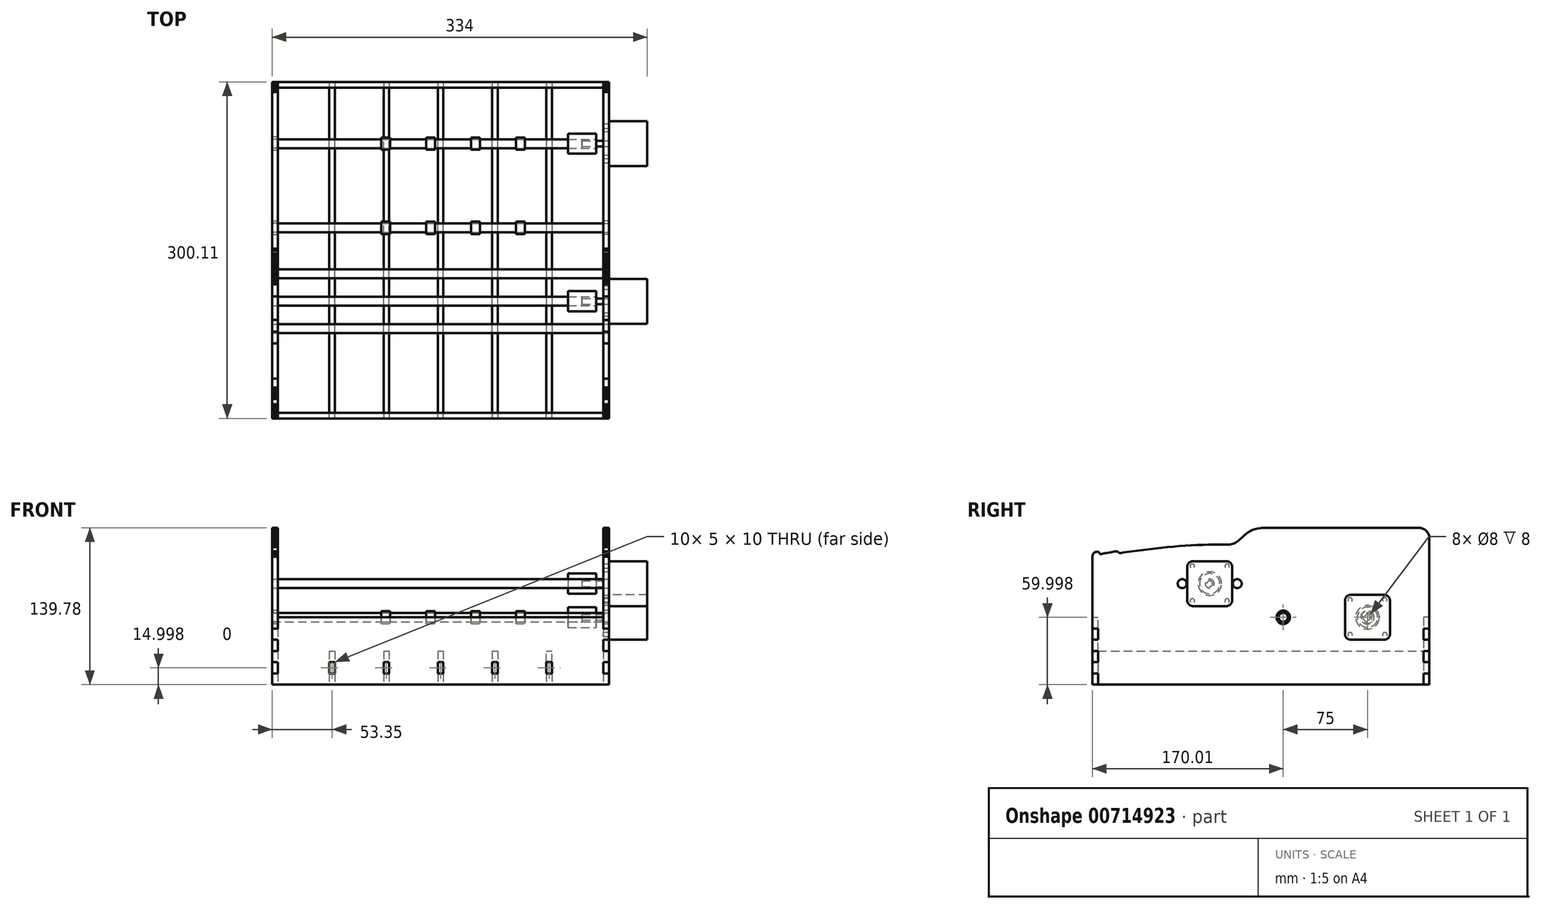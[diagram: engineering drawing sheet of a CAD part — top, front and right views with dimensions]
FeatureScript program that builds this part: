
annotation { "Feature Type Name" : "Feature", "Feature Type Description" : "" }
export const myFeature = defineFeature(function(context is Context, id is Id, definition is map)
    precondition{}
    {
        {
            assignVariable(context, id + "F0", {"name" : "panel_thickness", "anyValue" : 5});
        }
        {
            var Q0;
            Q0=qCreatedBy(makeId("Right.planeOp"),FACE);
            var sketch = newSketch(context, id + "F1", { "sketchPlane" : qUnion([Q0])});
            skLineSegment(sketch, "E0", {"start": v(-150.05, 30.1) * mm, "end": v(-150.05, 40.34) * mm});
            skLineSegment(sketch, "E1", {"start": v(-150.05, 40.34) * mm, "end": v(-150.05, 42.88) * mm});
            skLineSegment(sketch, "E2", {"start": v(-150.05, 42.88) * mm, "end": v(-150.05, 42.97) * mm});
            skLineSegment(sketch, "E3", {"start": v(-150.05, 42.97) * mm, "end": v(-150.05, 43.01) * mm});
            skLineSegment(sketch, "E4", {"start": v(-150.05, 43.01) * mm, "end": v(-150.05, 43.05) * mm});
            skLineSegment(sketch, "E5", {"start": v(-150.05, 43.05) * mm, "end": v(-150.05, 43.14) * mm});
            skLineSegment(sketch, "E6", {"start": v(-150.05, 43.14) * mm, "end": v(-150.05, 43.3) * mm});
            skLineSegment(sketch, "E7", {"start": v(-150.05, 43.3) * mm, "end": v(-150.05, 44.03) * mm});
            skLineSegment(sketch, "E8", {"start": v(-150.05, 44.03) * mm, "end": v(-150, 44.7) * mm});
            skLineSegment(sketch, "E9", {"start": v(-150, 44.7) * mm, "end": v(-149.88, 45.34) * mm});
            skLineSegment(sketch, "E10", {"start": v(-149.88, 45.34) * mm, "end": v(-149.71, 45.97) * mm});
            skLineSegment(sketch, "E11", {"start": v(-149.71, 45.97) * mm, "end": v(-149.46, 46.52) * mm});
            skLineSegment(sketch, "E12", {"start": v(-149.46, 46.52) * mm, "end": v(-149.08, 47.07) * mm});
            skLineSegment(sketch, "E13", {"start": v(-149.08, 47.07) * mm, "end": v(-148.61, 47.5) * mm});
            skLineSegment(sketch, "E14", {"start": v(-148.61, 47.5) * mm, "end": v(-148.06, 47.88) * mm});
            skLineSegment(sketch, "E15", {"start": v(-148.06, 47.88) * mm, "end": v(-147.43, 48.18) * mm});
            skLineSegment(sketch, "E16", {"start": v(-147.43, 48.18) * mm, "end": v(-146.75, 48.39) * mm});
            skLineSegment(sketch, "E17", {"start": v(-146.75, 48.39) * mm, "end": v(-146.03, 48.51) * mm});
            skLineSegment(sketch, "E18", {"start": v(-146.03, 48.51) * mm, "end": v(-145.35, 48.51) * mm});
            skLineSegment(sketch, "E19", {"start": v(-145.35, 48.51) * mm, "end": v(-145.01, 48.47) * mm});
            skLineSegment(sketch, "E20", {"start": v(-145.01, 48.47) * mm, "end": v(-144.67, 48.39) * mm});
            skLineSegment(sketch, "E21", {"start": v(-144.67, 48.39) * mm, "end": v(-144.42, 48.22) * mm});
            skLineSegment(sketch, "E22", {"start": v(-144.42, 48.22) * mm, "end": v(-144.17, 47.96) * mm});
            skLineSegment(sketch, "E23", {"start": v(-144.17, 47.96) * mm, "end": v(-143.83, 47.37) * mm});
            skLineSegment(sketch, "E24", {"start": v(-143.83, 47.37) * mm, "end": v(-143.45, 46.82) * mm});
            skLineSegment(sketch, "E25", {"start": v(-143.45, 46.82) * mm, "end": v(-143.23, 46.6) * mm});
            skLineSegment(sketch, "E26", {"start": v(-143.23, 46.6) * mm, "end": v(-142.98, 46.48) * mm});
            skLineSegment(sketch, "E27", {"start": v(-142.98, 46.48) * mm, "end": v(-142.64, 46.48) * mm});
            skLineSegment(sketch, "E28", {"start": v(-142.64, 46.48) * mm, "end": v(-142.3, 46.48) * mm});
            skLineSegment(sketch, "E29", {"start": v(-142.3, 46.48) * mm, "end": v(-141.58, 46.65) * mm});
            skLineSegment(sketch, "E30", {"start": v(-141.58, 46.65) * mm, "end": v(-140.19, 46.9) * mm});
            skLineSegment(sketch, "E31", {"start": v(-140.19, 46.9) * mm, "end": v(-138.87, 47.16) * mm});
            skLineSegment(sketch, "E32", {"start": v(-138.87, 47.16) * mm, "end": v(-137.56, 47.37) * mm});
            skLineSegment(sketch, "E33", {"start": v(-137.56, 47.37) * mm, "end": v(-135.06, 47.84) * mm});
            skLineSegment(sketch, "E34", {"start": v(-135.06, 47.84) * mm, "end": v(-132.57, 48.3) * mm});
            skLineSegment(sketch, "E35", {"start": v(-132.57, 48.3) * mm, "end": v(-131.3, 48.56) * mm});
            skLineSegment(sketch, "E36", {"start": v(-131.3, 48.56) * mm, "end": v(-129.94, 48.81) * mm});
            skLineSegment(sketch, "E37", {"start": v(-129.94, 48.81) * mm, "end": v(-129.22, 48.9) * mm});
            skLineSegment(sketch, "E38", {"start": v(-129.22, 48.9) * mm, "end": v(-128.59, 48.94) * mm});
            skLineSegment(sketch, "E39", {"start": v(-128.59, 48.94) * mm, "end": v(-128.25, 48.94) * mm});
            skLineSegment(sketch, "E40", {"start": v(-128.25, 48.94) * mm, "end": v(-127.95, 48.85) * mm});
            skLineSegment(sketch, "E41", {"start": v(-127.95, 48.85) * mm, "end": v(-127.66, 48.73) * mm});
            skLineSegment(sketch, "E42", {"start": v(-127.66, 48.73) * mm, "end": v(-127.36, 48.56) * mm});
            skLineSegment(sketch, "E43", {"start": v(-127.36, 48.56) * mm, "end": v(-126.3, 47.75) * mm});
            skLineSegment(sketch, "E44", {"start": v(-126.3, 47.75) * mm, "end": v(-126, 47.58) * mm});
            skLineSegment(sketch, "E45", {"start": v(-126, 47.58) * mm, "end": v(-125.7, 47.46) * mm});
            skLineSegment(sketch, "E46", {"start": v(-125.7, 47.46) * mm, "end": v(-125.41, 47.41) * mm});
            skLineSegment(sketch, "E47", {"start": v(-125.41, 47.41) * mm, "end": v(-125.07, 47.41) * mm});
            skLineSegment(sketch, "E48", {"start": v(-125.07, 47.41) * mm, "end": v(-123.72, 47.62) * mm});
            skLineSegment(sketch, "E49", {"start": v(-123.72, 47.62) * mm, "end": v(-122.36, 47.8) * mm});
            skLineSegment(sketch, "E50", {"start": v(-122.36, 47.8) * mm, "end": v(-119.74, 48.18) * mm});
            skLineSegment(sketch, "E51", {"start": v(-119.74, 48.18) * mm, "end": v(-114.66, 48.9) * mm});
            skLineSegment(sketch, "E52", {"start": v(-114.66, 48.9) * mm, "end": v(-109.5, 49.57) * mm});
            skLineSegment(sketch, "E53", {"start": v(-109.5, 49.57) * mm, "end": v(-104.29, 50.25) * mm});
            skLineSegment(sketch, "E54", {"start": v(-104.29, 50.25) * mm, "end": v(-93.83, 51.52) * mm});
            skLineSegment(sketch, "E55", {"start": v(-93.83, 51.52) * mm, "end": v(-88.54, 52.11) * mm});
            skLineSegment(sketch, "E56", {"start": v(-88.54, 52.11) * mm, "end": v(-83.25, 52.66) * mm});
            skLineSegment(sketch, "E57", {"start": v(-83.25, 52.66) * mm, "end": v(-77.96, 53.13) * mm});
            skLineSegment(sketch, "E58", {"start": v(-77.96, 53.13) * mm, "end": v(-72.67, 53.6) * mm});
            skLineSegment(sketch, "E59", {"start": v(-72.67, 53.6) * mm, "end": v(-67.42, 53.93) * mm});
            skLineSegment(sketch, "E60", {"start": v(-67.42, 53.93) * mm, "end": v(-62.2, 54.27) * mm});
            skLineSegment(sketch, "E61", {"start": v(-62.2, 54.27) * mm, "end": v(-56.96, 54.48) * mm});
            skLineSegment(sketch, "E62", {"start": v(-56.96, 54.48) * mm, "end": v(-51.75, 54.65) * mm});
            skLineSegment(sketch, "E63", {"start": v(-51.75, 54.65) * mm, "end": v(-46.5, 54.78) * mm});
            skLineSegment(sketch, "E64", {"start": v(-46.5, 54.78) * mm, "end": v(-41.21, 54.86) * mm});
            skLineSegment(sketch, "E65", {"start": v(-41.21, 54.86) * mm, "end": v(-35.88, 54.86) * mm});
            skLineSegment(sketch, "E66", {"start": v(-35.88, 54.86) * mm, "end": v(-30.46, 54.9) * mm});
            skLineSegment(sketch, "E67", {"start": v(-30.46, 54.9) * mm, "end": v(-29.1, 54.95) * mm});
            skLineSegment(sketch, "E68", {"start": v(-29.1, 54.95) * mm, "end": v(-27.8, 55.08) * mm});
            skLineSegment(sketch, "E69", {"start": v(-27.8, 55.08) * mm, "end": v(-26.52, 55.29) * mm});
            skLineSegment(sketch, "E70", {"start": v(-26.52, 55.29) * mm, "end": v(-25.25, 55.58) * mm});
            skLineSegment(sketch, "E71", {"start": v(-25.25, 55.58) * mm, "end": v(-24.07, 56) * mm});
            skLineSegment(sketch, "E72", {"start": v(-24.07, 56) * mm, "end": v(-22.88, 56.56) * mm});
            skLineSegment(sketch, "E73", {"start": v(-22.88, 56.56) * mm, "end": v(-21.78, 57.2) * mm});
            skLineSegment(sketch, "E74", {"start": v(-21.78, 57.2) * mm, "end": v(-20.72, 57.91) * mm});
            skLineSegment(sketch, "E75", {"start": v(-20.72, 57.91) * mm, "end": v(-19.66, 58.72) * mm});
            skLineSegment(sketch, "E76", {"start": v(-19.66, 58.72) * mm, "end": v(-18.65, 59.6) * mm});
            skLineSegment(sketch, "E77", {"start": v(-18.65, 59.6) * mm, "end": v(-16.62, 61.43) * mm});
            skLineSegment(sketch, "E78", {"start": v(-16.62, 61.43) * mm, "end": v(-14.63, 63.25) * mm});
            skLineSegment(sketch, "E79", {"start": v(-14.63, 63.25) * mm, "end": v(-13.61, 64.13) * mm});
            skLineSegment(sketch, "E80", {"start": v(-13.61, 64.13) * mm, "end": v(-12.55, 64.98) * mm});
            skLineSegment(sketch, "E81", {"start": v(-12.55, 64.98) * mm, "end": v(-11.5, 65.74) * mm});
            skLineSegment(sketch, "E82", {"start": v(-11.5, 65.74) * mm, "end": v(-10.4, 66.46) * mm});
            skLineSegment(sketch, "E83", {"start": v(-10.4, 66.46) * mm, "end": v(-9.25, 67.1) * mm});
            skLineSegment(sketch, "E84", {"start": v(-9.25, 67.1) * mm, "end": v(-8.1, 67.7) * mm});
            skLineSegment(sketch, "E85", {"start": v(-8.1, 67.7) * mm, "end": v(-6.88, 68.16) * mm});
            skLineSegment(sketch, "E86", {"start": v(-6.88, 68.16) * mm, "end": v(-5.65, 68.54) * mm});
            skLineSegment(sketch, "E87", {"start": v(-5.65, 68.54) * mm, "end": v(-4.38, 68.88) * mm});
            skLineSegment(sketch, "E88", {"start": v(-4.38, 68.88) * mm, "end": v(-3.07, 69.17) * mm});
            skLineSegment(sketch, "E89", {"start": v(-3.07, 69.17) * mm, "end": v(-0.44, 69.64) * mm});
            skLineSegment(sketch, "E90", {"start": v(-0.44, 69.64) * mm, "end": v(0.91, 69.85) * mm});
            skLineSegment(sketch, "E91", {"start": v(0.91, 69.85) * mm, "end": v(1.2, 69.9) * mm});
            skLineSegment(sketch, "E92", {"start": v(1.2, 69.9) * mm, "end": v(1.25, 69.9) * mm});
            skLineSegment(sketch, "E93", {"start": v(1.25, 69.9) * mm, "end": v(1.3, 69.9) * mm});
            skLineSegment(sketch, "E94", {"start": v(1.3, 69.9) * mm, "end": v(1.38, 69.9) * mm});
            skLineSegment(sketch, "E95", {"start": v(1.38, 69.9) * mm, "end": v(1.59, 69.9) * mm});
            skLineSegment(sketch, "E96", {"start": v(1.59, 69.9) * mm, "end": v(2.05, 69.9) * mm});
            skLineSegment(sketch, "E97", {"start": v(2.05, 69.9) * mm, "end": v(3.75, 69.9) * mm});
            skLineSegment(sketch, "E98", {"start": v(3.75, 69.9) * mm, "end": v(7.22, 69.9) * mm});
            skLineSegment(sketch, "E99", {"start": v(7.22, 69.9) * mm, "end": v(14.12, 69.9) * mm});
            skLineSegment(sketch, "E100", {"start": v(14.12, 69.9) * mm, "end": v(27.96, 69.9) * mm});
            skLineSegment(sketch, "E101", {"start": v(27.96, 69.9) * mm, "end": v(83.25, 69.9) * mm});
            skLineSegment(sketch, "E102", {"start": v(83.25, 69.9) * mm, "end": v(138.58, 69.9) * mm});
            skLineSegment(sketch, "E103", {"start": v(138.58, 69.9) * mm, "end": v(140.27, 69.9) * mm});
            skLineSegment(sketch, "E104", {"start": v(140.27, 69.9) * mm, "end": v(140.4, 69.9) * mm});
            skLineSegment(sketch, "E105", {"start": v(140.4, 69.9) * mm, "end": v(140.61, 69.9) * mm});
            skLineSegment(sketch, "E106", {"start": v(140.61, 69.9) * mm, "end": v(141.08, 69.9) * mm});
            skLineSegment(sketch, "E107", {"start": v(141.08, 69.9) * mm, "end": v(142, 69.8) * mm});
            skLineSegment(sketch, "E108", {"start": v(142, 69.8) * mm, "end": v(142.94, 69.6) * mm});
            skLineSegment(sketch, "E109", {"start": v(142.94, 69.6) * mm, "end": v(143.87, 69.3) * mm});
            skLineSegment(sketch, "E110", {"start": v(143.87, 69.3) * mm, "end": v(144.76, 68.96) * mm});
            skLineSegment(sketch, "E111", {"start": v(144.76, 68.96) * mm, "end": v(145.56, 68.5) * mm});
            skLineSegment(sketch, "E112", {"start": v(145.56, 68.5) * mm, "end": v(146.37, 67.94) * mm});
            skLineSegment(sketch, "E113", {"start": v(146.37, 67.94) * mm, "end": v(147.09, 67.3) * mm});
            skLineSegment(sketch, "E114", {"start": v(147.09, 67.3) * mm, "end": v(147.72, 66.67) * mm});
            skLineSegment(sketch, "E115", {"start": v(147.72, 66.67) * mm, "end": v(148.27, 65.96) * mm});
            skLineSegment(sketch, "E116", {"start": v(148.27, 65.96) * mm, "end": v(148.78, 65.15) * mm});
            skLineSegment(sketch, "E117", {"start": v(148.78, 65.15) * mm, "end": v(149.2, 64.3) * mm});
            skLineSegment(sketch, "E118", {"start": v(149.2, 64.3) * mm, "end": v(149.58, 63.42) * mm});
            skLineSegment(sketch, "E119", {"start": v(149.58, 63.42) * mm, "end": v(149.84, 62.48) * mm});
            skLineSegment(sketch, "E120", {"start": v(149.84, 62.48) * mm, "end": v(150, 61.55) * mm});
            skLineSegment(sketch, "E121", {"start": v(150, 61.55) * mm, "end": v(150.05, 60.62) * mm});
            skLineSegment(sketch, "E122", {"start": v(150.05, 60.62) * mm, "end": v(150, 59.69) * mm});
            skLineSegment(sketch, "E123", {"start": v(150, 59.69) * mm, "end": v(149.97, 59.22) * mm});
            skLineSegment(sketch, "E124", {"start": v(149.97, 59.22) * mm, "end": v(149.97, 58.97) * mm});
            skLineSegment(sketch, "E125", {"start": v(149.97, 58.97) * mm, "end": v(149.92, 58.89) * mm});
            skLineSegment(sketch, "E126", {"start": v(149.92, 58.89) * mm, "end": v(149.92, 58.8) * mm});
            skLineSegment(sketch, "E127", {"start": v(149.92, 58.8) * mm, "end": v(149.92, 58.63) * mm});
            skLineSegment(sketch, "E128", {"start": v(149.92, 58.63) * mm, "end": v(149.92, 52.96) * mm});
            skLineSegment(sketch, "E129", {"start": v(149.92, 52.96) * mm, "end": v(149.92, 30.1) * mm});
            skLineSegment(sketch, "E130", {"start": v(144.93, -59.9) * mm, "end": v(144.93, -69.9) * mm});
            skLineSegment(sketch, "E131", {"start": v(144.93, -69.9) * mm, "end": v(-145.06, -69.9) * mm});
            skLineSegment(sketch, "E132", {"start": v(-145.06, -59.9) * mm, "end": v(-145.06, -69.9) * mm});
            skLineSegment(sketch, "E133", {"start": v(149.92, -59.9) * mm, "end": v(144.93, -59.9) * mm});
            skLineSegment(sketch, "E134", {"start": v(-150.05, -59.9) * mm, "end": v(-145.06, -59.9) * mm});
            skLineSegment(sketch, "E135", {"start": v(149.92, -49.91) * mm, "end": v(149.92, -59.9) * mm});
            skLineSegment(sketch, "E136", {"start": v(-150.05, -59.9) * mm, "end": v(-150.05, -49.91) * mm});
            skLineSegment(sketch, "E137", {"start": v(144.93, -49.91) * mm, "end": v(149.92, -49.91) * mm});
            skLineSegment(sketch, "E138", {"start": v(-145.06, -49.91) * mm, "end": v(-150.05, -49.91) * mm});
            skLineSegment(sketch, "E139", {"start": v(144.93, -39.88) * mm, "end": v(144.93, -49.91) * mm});
            skLineSegment(sketch, "E140", {"start": v(-145.06, -39.88) * mm, "end": v(-145.06, -49.91) * mm});
            skLineSegment(sketch, "E141", {"start": v(149.92, -39.88) * mm, "end": v(144.93, -39.88) * mm});
            skLineSegment(sketch, "E142", {"start": v(-150.05, -39.88) * mm, "end": v(-145.06, -39.88) * mm});
            skLineSegment(sketch, "E143", {"start": v(149.92, -29.89) * mm, "end": v(149.92, -39.88) * mm});
            skLineSegment(sketch, "E144", {"start": v(-150.05, -39.88) * mm, "end": v(-150.05, -29.89) * mm});
            skLineSegment(sketch, "E145", {"start": v(144.93, -29.89) * mm, "end": v(149.92, -29.89) * mm});
            skLineSegment(sketch, "E146", {"start": v(-145.06, -29.89) * mm, "end": v(-150.05, -29.89) * mm});
            skLineSegment(sketch, "E147", {"start": v(144.93, -19.9) * mm, "end": v(144.93, -29.89) * mm});
            skLineSegment(sketch, "E148", {"start": v(-145.06, -19.9) * mm, "end": v(-145.06, -29.89) * mm});
            skLineSegment(sketch, "E149", {"start": v(149.92, -19.9) * mm, "end": v(144.93, -19.9) * mm});
            skLineSegment(sketch, "E150", {"start": v(-150.05, -19.9) * mm, "end": v(-145.06, -19.9) * mm});
            skLineSegment(sketch, "E151", {"start": v(149.92, 30.1) * mm, "end": v(149.92, -19.9) * mm});
            skLineSegment(sketch, "E152", {"start": v(-150.05, -19.9) * mm, "end": v(-150.05, 30.1) * mm});
            skCircle(sketch, "E153", {"center": v(-45.55, 20.1) * mm, "radius": 10.5 * mm});
            skLineSegment(sketch, "E154", {"start": v(-70.05, 20.1) * mm, "end": v(-45.55, 20.1) * mm, "construction": true});
            skCircle(sketch, "E155", {"center": v(-70.05, 20.1) * mm, "radius": 4 * mm});
            skLineSegment(sketch, "E156", {"start": v(-45.55, 20.1) * mm, "end": v(-21.05, 20.1) * mm, "construction": true});
            skCircle(sketch, "E157", {"center": v(-21.05, 20.1) * mm, "radius": 4 * mm});
            skLineSegment(sketch, "E158", {"start": v(-45.55, 20.1) * mm, "end": v(-30.06, 35.6) * mm, "construction": true});
            skCircle(sketch, "E159", {"center": v(-30.06, 35.6) * mm, "radius": 2 * mm});
            skLineSegment(sketch, "E160", {"start": v(-45.55, 20.1) * mm, "end": v(-30.06, 4.62) * mm, "construction": true});
            skLineSegment(sketch, "E161", {"start": v(-45.55, 20.1) * mm, "end": v(-61.04, 4.62) * mm, "construction": true});
            skLineSegment(sketch, "E162", {"start": v(-45.55, 20.1) * mm, "end": v(-61.04, 35.6) * mm, "construction": true});
            skCircle(sketch, "E163", {"center": v(-61.04, 35.6) * mm, "radius": 2 * mm});
            skCircle(sketch, "E164", {"center": v(-61.04, 4.62) * mm, "radius": 2 * mm});
            skCircle(sketch, "E165", {"center": v(-30.06, 4.62) * mm, "radius": 2 * mm});
            skLineSegment(sketch, "E166", {"start": v(-45.55, 20.1) * mm, "end": v(-45.55, -69.9) * mm, "construction": true});
            skLineSegment(sketch, "E167", {"start": v(19.95, -9.9) * mm, "end": v(19.95, -69.9) * mm, "construction": true});
            skCircle(sketch, "E168", {"center": v(19.95, -9.9) * mm, "radius": 6 * mm});
            skLineSegment(sketch, "E169", {"start": v(94.95, -9.9) * mm, "end": v(94.95, -69.9) * mm, "construction": true});
            skCircle(sketch, "E170", {"center": v(94.95, -9.9) * mm, "radius": 10.5 * mm});
            skLineSegment(sketch, "E171", {"start": v(94.95, -9.9) * mm, "end": v(110.44, 5.6) * mm, "construction": true});
            skLineSegment(sketch, "E172", {"start": v(94.95, -9.9) * mm, "end": v(110.44, -25.38) * mm, "construction": true});
            skLineSegment(sketch, "E173", {"start": v(94.95, -9.9) * mm, "end": v(79.46, -25.38) * mm, "construction": true});
            skLineSegment(sketch, "E174", {"start": v(94.95, -9.9) * mm, "end": v(79.46, 5.6) * mm, "construction": true});
            skCircle(sketch, "E175", {"center": v(110.44, 5.6) * mm, "radius": 2 * mm});
            skCircle(sketch, "E176", {"center": v(110.44, -25.38) * mm, "radius": 2 * mm});
            skCircle(sketch, "E177", {"center": v(79.46, -25.38) * mm, "radius": 2 * mm});
            skCircle(sketch, "E178", {"center": v(79.46, 5.6) * mm, "radius": 2 * mm});
            skSolve(sketch);
        }
        {
            var Q0;
            Q0=makeQuery(id+"F1.imprint","IMPRINT",FACE,{"disambiguationData":[TD([[makeQuery(id+"F1.imprint","IMPRINT",EDGE,{"derivedFrom":sQuery(id+"F1.wireOp",EDGE,"E0")}),-1.0]])]});
            extrude(context, id + "F2", {"entities" : qUnion([Q0]), "depth" : (getVariable(context, 'panel_thickness')) * mm, "offsetDistance" : 25 * mm});
        }
        {
            var Q0;
            Q0=makeQuery(id+"F2.opExtrude","SWEPT_FACE",FACE,{"disambiguationData":[OSD([sQuery(id+"F1.wireOp",EDGE,"E148")])]});
            var sketch = newSketch(context, id + "F3", { "sketchPlane" : qUnion([Q0])});
            skPoint(sketch, "E179.0", {"position": v(0, -69.9) * mm});
            skPoint(sketch, "E179.1", {"position": v(5, -69.9) * mm});
            skPoint(sketch, "E179.2", {"position": v(5, -59.9) * mm});
            skPoint(sketch, "E179.3", {"position": v(0, -59.9) * mm});
            skPoint(sketch, "E179.4", {"position": v(0, -49.91) * mm});
            skPoint(sketch, "E179.5", {"position": v(5, -49.91) * mm});
            skPoint(sketch, "E179.6", {"position": v(0, -29.89) * mm});
            skPoint(sketch, "E179.7", {"position": v(5, -29.89) * mm});
            skPoint(sketch, "E179.8", {"position": v(0, -39.88) * mm});
            skPoint(sketch, "E179.9", {"position": v(5, -39.88) * mm});
            skPoint(sketch, "E179.10", {"position": v(0, -19.9) * mm});
            skPoint(sketch, "E179.11", {"position": v(5, -19.9) * mm});
            skLineSegment(sketch, "E180", {"start": v(0, -69.9) * mm, "end": v(5, -69.9) * mm});
            skLineSegment(sketch, "E181", {"start": v(5, -69.9) * mm, "end": v(5, -59.9) * mm});
            skLineSegment(sketch, "E182", {"start": v(5, -59.9) * mm, "end": v(0, -59.9) * mm});
            skLineSegment(sketch, "E183", {"start": v(0, -59.9) * mm, "end": v(0, -49.91) * mm});
            skLineSegment(sketch, "E184", {"start": v(0, -49.91) * mm, "end": v(5, -49.91) * mm});
            skLineSegment(sketch, "E185", {"start": v(5, -49.91) * mm, "end": v(5, -39.88) * mm});
            skLineSegment(sketch, "E186", {"start": v(5, -39.88) * mm, "end": v(0, -39.88) * mm});
            skLineSegment(sketch, "E187", {"start": v(0, -39.88) * mm, "end": v(0, -29.89) * mm});
            skLineSegment(sketch, "E188", {"start": v(0, -29.89) * mm, "end": v(5, -29.89) * mm});
            skLineSegment(sketch, "E189", {"start": v(5, -29.89) * mm, "end": v(5, -19.9) * mm});
            skLineSegment(sketch, "E190", {"start": v(5, -19.9) * mm, "end": v(0, -19.9) * mm});
            skLineSegment(sketch, "E191", {"start": v(0, -19.9) * mm, "end": v(0, -9.9) * mm});
            skLineSegment(sketch, "E192", {"start": v(0, -9.9) * mm, "end": v(-290, -9.9) * mm});
            skLineSegment(sketch, "E193", {"start": v(-145, -9.9) * mm, "end": v(-145, -69.9) * mm, "construction": true});
            skLineSegment(sketch, "E194", {"start": v(0, -69.9) * mm, "end": v(-145, -69.9) * mm});
            skLineSegment(sketch, "E195", {"start": v(-145, -59.9) * mm, "end": v(-142.5, -59.9) * mm});
            skLineSegment(sketch, "E196", {"start": v(-142.5, -59.9) * mm, "end": v(-142.5, -49.9) * mm});
            skLineSegment(sketch, "E197", {"start": v(-142.5, -49.9) * mm, "end": v(-145, -49.9) * mm});
            skLineSegment(sketch, "E198.bottom", {"start": v(-99.17, -49.9) * mm, "end": v(-94.17, -49.9) * mm});
            skLineSegment(sketch, "E198.top", {"start": v(-99.17, -59.9) * mm, "end": v(-94.17, -59.9) * mm});
            skLineSegment(sketch, "E198.left", {"start": v(-99.17, -49.9) * mm, "end": v(-99.17, -59.9) * mm});
            skLineSegment(sketch, "E198.right", {"start": v(-94.17, -49.9) * mm, "end": v(-94.17, -59.9) * mm});
            skLineSegment(sketch, "E199.bottom", {"start": v(-50.85, -49.9) * mm, "end": v(-45.85, -49.9) * mm});
            skLineSegment(sketch, "E199.top", {"start": v(-50.85, -59.9) * mm, "end": v(-45.85, -59.9) * mm});
            skLineSegment(sketch, "E199.left", {"start": v(-50.85, -49.9) * mm, "end": v(-50.85, -59.9) * mm});
            skLineSegment(sketch, "E199.right", {"start": v(-45.85, -49.9) * mm, "end": v(-45.85, -59.9) * mm});
            skLineSegment(sketch, "E200", {"start": v(-142.5, -59.9) * mm, "end": v(-99.17, -59.9) * mm, "construction": true});
            skLineSegment(sketch, "E201", {"start": v(-94.17, -59.9) * mm, "end": v(-50.85, -59.9) * mm, "construction": true});
            skLineSegment(sketch, "E202", {"start": v(-45.85, -59.9) * mm, "end": v(0, -59.9) * mm, "construction": true});
            skLineSegment(sketch, "E203.MirrorCS", {"start": v(-290, -19.9) * mm, "end": v(-290, -9.9) * mm});
            skLineSegment(sketch, "E204.MirrorCS", {"start": v(-295, -19.9) * mm, "end": v(-290, -19.9) * mm});
            skLineSegment(sketch, "E205.MirrorCS", {"start": v(-295, -29.89) * mm, "end": v(-295, -19.9) * mm});
            skLineSegment(sketch, "E206.MirrorCS", {"start": v(-290, -29.89) * mm, "end": v(-295, -29.89) * mm});
            skLineSegment(sketch, "E207.MirrorCS", {"start": v(-290, -39.88) * mm, "end": v(-290, -29.89) * mm});
            skLineSegment(sketch, "E208.MirrorCS", {"start": v(-295, -39.88) * mm, "end": v(-290, -39.88) * mm});
            skLineSegment(sketch, "E209.MirrorCS", {"start": v(-295, -49.91) * mm, "end": v(-295, -39.88) * mm});
            skLineSegment(sketch, "E210.MirrorCS", {"start": v(-290, -49.91) * mm, "end": v(-295, -49.91) * mm});
            skLineSegment(sketch, "E211.MirrorCS", {"start": v(-290, -59.9) * mm, "end": v(-290, -49.91) * mm});
            skLineSegment(sketch, "E212.MirrorCS", {"start": v(-295, -59.9) * mm, "end": v(-290, -59.9) * mm});
            skLineSegment(sketch, "E213.MirrorCS", {"start": v(-295, -69.9) * mm, "end": v(-295, -59.9) * mm});
            skLineSegment(sketch, "E214.MirrorCS", {"start": v(-290, -69.9) * mm, "end": v(-295, -69.9) * mm});
            skLineSegment(sketch, "E215.MirrorCS", {"start": v(-290, -69.9) * mm, "end": v(-145, -69.9) * mm});
            skLineSegment(sketch, "E216.MirrorCS", {"start": v(-244.15, -49.9) * mm, "end": v(-244.15, -59.9) * mm});
            skLineSegment(sketch, "E217.MirrorCS", {"start": v(-239.15, -49.9) * mm, "end": v(-244.15, -49.9) * mm});
            skLineSegment(sketch, "E218.MirrorCS", {"start": v(-239.15, -49.9) * mm, "end": v(-239.15, -59.9) * mm});
            skLineSegment(sketch, "E219.MirrorCS", {"start": v(-239.15, -59.9) * mm, "end": v(-244.15, -59.9) * mm});
            skLineSegment(sketch, "E220.MirrorCS", {"start": v(-195.82, -49.9) * mm, "end": v(-195.82, -59.9) * mm});
            skLineSegment(sketch, "E221.MirrorCS", {"start": v(-190.82, -49.9) * mm, "end": v(-195.82, -49.9) * mm});
            skLineSegment(sketch, "E222.MirrorCS", {"start": v(-190.82, -49.9) * mm, "end": v(-190.82, -59.9) * mm});
            skLineSegment(sketch, "E223.MirrorCS", {"start": v(-190.82, -59.9) * mm, "end": v(-195.82, -59.9) * mm});
            skLineSegment(sketch, "E224.MirrorCS", {"start": v(-145, -59.9) * mm, "end": v(-147.5, -59.9) * mm});
            skLineSegment(sketch, "E225.MirrorCS", {"start": v(-147.5, -59.9) * mm, "end": v(-147.5, -49.9) * mm});
            skLineSegment(sketch, "E226.MirrorCS", {"start": v(-147.5, -49.9) * mm, "end": v(-145, -49.9) * mm});
            skSolve(sketch);
        }
        {
            var Q0;
            Q0=makeQuery(id+"F3.imprint","IMPRINT",FACE,{"disambiguationData":[TD([[makeQuery(id+"F3.imprint","IMPRINT",EDGE,{"derivedFrom":sQuery(id+"F3.wireOp",EDGE,"E180")}),1.0]])]});
            var Q1;
            Q1=makeQuery(id+"F3.imprint","IMPRINT",FACE,{"disambiguationData":[TD([[makeQuery(id+"F3.imprint","IMPRINT",EDGE,{"derivedFrom":sQuery(id+"F3.wireOp",EDGE,"E188")}),-1.0]])]});
            extrude(context, id + "F4", {"entities" : qUnion([Q0, Q1]), "depth" : (getVariable(context, 'panel_thickness')) * mm, "offsetDistance" : 25 * mm});
        }
        {
            var Q0;
            Q0=makeQuery(id+"F2.opExtrude","SWEPT_FACE",FACE,{"disambiguationData":[OSD([sQuery(id+"F1.wireOp",EDGE,"E147")])]});
            var sketch = newSketch(context, id + "F5", { "sketchPlane" : qUnion([Q0])});
            skLineSegment(sketch, "E227.0.0", {"start": v(0, -29.89) * mm, "end": v(0, -39.88) * mm});
            skLineSegment(sketch, "E227.0.1", {"start": v(0, -39.88) * mm, "end": v(-5, -39.88) * mm});
            skLineSegment(sketch, "E227.0.2", {"start": v(-5, -39.88) * mm, "end": v(-5, -49.91) * mm});
            skLineSegment(sketch, "E227.0.3", {"start": v(-5, -49.91) * mm, "end": v(0, -49.91) * mm});
            skLineSegment(sketch, "E227.0.4", {"start": v(0, -49.91) * mm, "end": v(0, -59.9) * mm});
            skLineSegment(sketch, "E227.0.5", {"start": v(0, -59.9) * mm, "end": v(-5, -59.9) * mm});
            skLineSegment(sketch, "E227.0.6", {"start": v(-5, -59.9) * mm, "end": v(-5, -69.9) * mm});
            skLineSegment(sketch, "E227.0.7", {"start": v(-5, -69.9) * mm, "end": v(295, -69.9) * mm});
            skLineSegment(sketch, "E227.0.8", {"start": v(295, -69.9) * mm, "end": v(295, -59.9) * mm});
            skLineSegment(sketch, "E227.0.9", {"start": v(295, -59.9) * mm, "end": v(290, -59.9) * mm});
            skLineSegment(sketch, "E227.0.10", {"start": v(290, -59.9) * mm, "end": v(290, -49.91) * mm});
            skLineSegment(sketch, "E227.0.11", {"start": v(290, -49.91) * mm, "end": v(295, -49.91) * mm});
            skLineSegment(sketch, "E227.0.12", {"start": v(295, -49.91) * mm, "end": v(295, -39.88) * mm});
            skLineSegment(sketch, "E227.0.13", {"start": v(295, -39.88) * mm, "end": v(290, -39.88) * mm});
            skLineSegment(sketch, "E227.0.14", {"start": v(290, -39.88) * mm, "end": v(290, -29.89) * mm});
            skLineSegment(sketch, "E227.0.15", {"start": v(290, -29.89) * mm, "end": v(295, -29.89) * mm});
            skLineSegment(sketch, "E227.0.16", {"start": v(295, -29.89) * mm, "end": v(295, -19.9) * mm});
            skLineSegment(sketch, "E227.0.17", {"start": v(295, -19.9) * mm, "end": v(290, -19.9) * mm});
            skLineSegment(sketch, "E227.0.18", {"start": v(290, -19.9) * mm, "end": v(290, -9.9) * mm});
            skLineSegment(sketch, "E227.0.19", {"start": v(290, -9.9) * mm, "end": v(0, -9.9) * mm});
            skLineSegment(sketch, "E227.0.20", {"start": v(0, -9.9) * mm, "end": v(0, -19.9) * mm});
            skLineSegment(sketch, "E227.0.21", {"start": v(0, -19.9) * mm, "end": v(-5, -19.9) * mm});
            skLineSegment(sketch, "E227.0.22", {"start": v(-5, -19.9) * mm, "end": v(-5, -29.89) * mm});
            skLineSegment(sketch, "E227.0.23", {"start": v(-5, -29.89) * mm, "end": v(0, -29.89) * mm});
            skLineSegment(sketch, "E228.0", {"start": v(45.85, -49.9) * mm, "end": v(45.85, -59.9) * mm});
            skLineSegment(sketch, "E228.1", {"start": v(50.85, -49.9) * mm, "end": v(45.85, -49.9) * mm});
            skLineSegment(sketch, "E228.2", {"start": v(50.85, -49.9) * mm, "end": v(50.85, -59.9) * mm});
            skLineSegment(sketch, "E228.3", {"start": v(50.85, -59.9) * mm, "end": v(45.85, -59.9) * mm});
            skLineSegment(sketch, "E228.4", {"start": v(99.17, -59.9) * mm, "end": v(94.17, -59.9) * mm});
            skLineSegment(sketch, "E228.5", {"start": v(94.17, -49.9) * mm, "end": v(94.17, -59.9) * mm});
            skLineSegment(sketch, "E228.6", {"start": v(99.17, -49.9) * mm, "end": v(94.17, -49.9) * mm});
            skLineSegment(sketch, "E228.7", {"start": v(99.17, -49.9) * mm, "end": v(99.17, -59.9) * mm});
            skLineSegment(sketch, "E228.8", {"start": v(147.5, -59.9) * mm, "end": v(142.5, -59.9) * mm});
            skLineSegment(sketch, "E228.9", {"start": v(142.5, -59.9) * mm, "end": v(142.5, -49.9) * mm});
            skLineSegment(sketch, "E228.10", {"start": v(147.5, -49.9) * mm, "end": v(142.5, -49.9) * mm});
            skLineSegment(sketch, "E228.11", {"start": v(147.5, -59.9) * mm, "end": v(147.5, -49.9) * mm});
            skLineSegment(sketch, "E228.12", {"start": v(190.82, -49.9) * mm, "end": v(195.82, -49.9) * mm});
            skLineSegment(sketch, "E228.13", {"start": v(190.82, -49.9) * mm, "end": v(190.82, -59.9) * mm});
            skLineSegment(sketch, "E228.14", {"start": v(195.82, -49.9) * mm, "end": v(195.82, -59.9) * mm});
            skLineSegment(sketch, "E228.15", {"start": v(190.82, -59.9) * mm, "end": v(195.82, -59.9) * mm});
            skLineSegment(sketch, "E228.16", {"start": v(239.15, -49.9) * mm, "end": v(244.15, -49.9) * mm});
            skLineSegment(sketch, "E228.17", {"start": v(244.15, -49.9) * mm, "end": v(244.15, -59.9) * mm});
            skLineSegment(sketch, "E228.18", {"start": v(239.15, -49.9) * mm, "end": v(239.15, -59.9) * mm});
            skLineSegment(sketch, "E228.19", {"start": v(239.15, -59.9) * mm, "end": v(244.15, -59.9) * mm});
            skSolve(sketch);
        }
        {
            var Q0;
            Q0=makeQuery(id+"F5.imprint","IMPRINT",FACE,{"disambiguationData":[TD([[makeQuery(id+"F5.imprint","IMPRINT",EDGE,{"derivedFrom":sQuery(id+"F5.wireOp",EDGE,"E227.0.0")}),1.0]])]});
            var Q1;
            Q1=makeQuery(id+"F5.imprint","IMPRINT",FACE,{"disambiguationData":[TD([[makeQuery(id+"F5.imprint","IMPRINT",EDGE,{"derivedFrom":sQuery(id+"F5.wireOp",EDGE,"E227.0.21")}),-1.0]])]});
            extrude(context, id + "F6", {"entities" : qUnion([Q0, Q1]), "depth" : (getVariable(context, 'panel_thickness')) * mm, "offsetDistance" : 25 * mm});
        }
        {
            var Q0;
            Q0=makeQuery(id+"F6.opExtrude","SWEPT_FACE",FACE,{"disambiguationData":[OSD([sQuery(id+"F5.wireOp",EDGE,"E227.0.18")])]});
            var sketch = newSketch(context, id + "F7", { "sketchPlane" : qUnion([Q0])});
            skLineSegment(sketch, "E229.0.0", {"start": v(145.06, -59.9) * mm, "end": v(150.05, -59.9) * mm});
            skLineSegment(sketch, "E229.0.1", {"start": v(150.05, -59.9) * mm, "end": v(150.05, -49.91) * mm});
            skLineSegment(sketch, "E229.0.2", {"start": v(150.05, -49.91) * mm, "end": v(145.06, -49.91) * mm});
            skLineSegment(sketch, "E229.0.3", {"start": v(145.06, -49.91) * mm, "end": v(145.06, -39.88) * mm});
            skLineSegment(sketch, "E229.0.4", {"start": v(145.06, -39.88) * mm, "end": v(150.05, -39.88) * mm});
            skLineSegment(sketch, "E229.0.5", {"start": v(150.05, -39.88) * mm, "end": v(150.05, -29.89) * mm});
            skLineSegment(sketch, "E229.0.6", {"start": v(150.05, -29.89) * mm, "end": v(145.06, -29.89) * mm});
            skLineSegment(sketch, "E229.0.7", {"start": v(145.06, -29.89) * mm, "end": v(145.06, -19.9) * mm});
            skLineSegment(sketch, "E229.0.8", {"start": v(145.06, -19.9) * mm, "end": v(150.05, -19.9) * mm});
            skLineSegment(sketch, "E229.0.9", {"start": v(150.05, -19.9) * mm, "end": v(150.05, 44.03) * mm});
            skLineSegment(sketch, "E229.0.10", {"start": v(150.05, 44.03) * mm, "end": v(150, 44.7) * mm});
            skLineSegment(sketch, "E229.0.11", {"start": v(150, 44.7) * mm, "end": v(149.88, 45.34) * mm});
            skLineSegment(sketch, "E229.0.12", {"start": v(149.88, 45.34) * mm, "end": v(149.71, 45.97) * mm});
            skLineSegment(sketch, "E229.0.13", {"start": v(149.71, 45.97) * mm, "end": v(149.46, 46.52) * mm});
            skLineSegment(sketch, "E229.0.14", {"start": v(149.46, 46.52) * mm, "end": v(149.08, 47.07) * mm});
            skLineSegment(sketch, "E229.0.15", {"start": v(149.08, 47.07) * mm, "end": v(148.61, 47.5) * mm});
            skLineSegment(sketch, "E229.0.16", {"start": v(148.61, 47.5) * mm, "end": v(148.06, 47.88) * mm});
            skLineSegment(sketch, "E229.0.17", {"start": v(148.06, 47.88) * mm, "end": v(147.43, 48.18) * mm});
            skLineSegment(sketch, "E229.0.18", {"start": v(147.43, 48.18) * mm, "end": v(146.75, 48.39) * mm});
            skLineSegment(sketch, "E229.0.19", {"start": v(146.75, 48.39) * mm, "end": v(146.03, 48.51) * mm});
            skLineSegment(sketch, "E229.0.20", {"start": v(146.03, 48.51) * mm, "end": v(145.35, 48.51) * mm});
            skLineSegment(sketch, "E229.0.21", {"start": v(145.35, 48.51) * mm, "end": v(145.01, 48.47) * mm});
            skLineSegment(sketch, "E229.0.22", {"start": v(145.01, 48.47) * mm, "end": v(144.67, 48.39) * mm});
            skLineSegment(sketch, "E229.0.23", {"start": v(144.67, 48.39) * mm, "end": v(144.42, 48.22) * mm});
            skLineSegment(sketch, "E229.0.24", {"start": v(144.42, 48.22) * mm, "end": v(144.17, 47.96) * mm});
            skLineSegment(sketch, "E229.0.25", {"start": v(144.17, 47.96) * mm, "end": v(143.83, 47.37) * mm});
            skLineSegment(sketch, "E229.0.26", {"start": v(143.83, 47.37) * mm, "end": v(143.45, 46.82) * mm});
            skLineSegment(sketch, "E229.0.27", {"start": v(143.45, 46.82) * mm, "end": v(143.23, 46.6) * mm});
            skLineSegment(sketch, "E229.0.28", {"start": v(143.23, 46.6) * mm, "end": v(142.98, 46.48) * mm});
            skLineSegment(sketch, "E229.0.29", {"start": v(142.98, 46.48) * mm, "end": v(142.3, 46.48) * mm});
            skLineSegment(sketch, "E229.0.30", {"start": v(142.3, 46.48) * mm, "end": v(141.58, 46.65) * mm});
            skLineSegment(sketch, "E229.0.31", {"start": v(141.58, 46.65) * mm, "end": v(140.19, 46.9) * mm});
            skLineSegment(sketch, "E229.0.32", {"start": v(140.19, 46.9) * mm, "end": v(138.87, 47.16) * mm});
            skLineSegment(sketch, "E229.0.33", {"start": v(138.87, 47.16) * mm, "end": v(137.56, 47.37) * mm});
            skLineSegment(sketch, "E229.0.34", {"start": v(137.56, 47.37) * mm, "end": v(132.57, 48.3) * mm});
            skLineSegment(sketch, "E229.0.35", {"start": v(132.57, 48.3) * mm, "end": v(131.3, 48.56) * mm});
            skLineSegment(sketch, "E229.0.36", {"start": v(131.3, 48.56) * mm, "end": v(129.94, 48.81) * mm});
            skLineSegment(sketch, "E229.0.37", {"start": v(129.94, 48.81) * mm, "end": v(129.22, 48.9) * mm});
            skLineSegment(sketch, "E229.0.38", {"start": v(129.22, 48.9) * mm, "end": v(128.59, 48.94) * mm});
            skLineSegment(sketch, "E229.0.39", {"start": v(128.59, 48.94) * mm, "end": v(128.25, 48.94) * mm});
            skLineSegment(sketch, "E229.0.40", {"start": v(128.25, 48.94) * mm, "end": v(127.95, 48.85) * mm});
            skLineSegment(sketch, "E229.0.41", {"start": v(127.95, 48.85) * mm, "end": v(127.66, 48.73) * mm});
            skLineSegment(sketch, "E229.0.42", {"start": v(127.66, 48.73) * mm, "end": v(127.36, 48.56) * mm});
            skLineSegment(sketch, "E229.0.43", {"start": v(127.36, 48.56) * mm, "end": v(126.3, 47.75) * mm});
            skLineSegment(sketch, "E229.0.44", {"start": v(126.3, 47.75) * mm, "end": v(126, 47.58) * mm});
            skLineSegment(sketch, "E229.0.45", {"start": v(126, 47.58) * mm, "end": v(125.7, 47.46) * mm});
            skLineSegment(sketch, "E229.0.46", {"start": v(125.7, 47.46) * mm, "end": v(125.41, 47.41) * mm});
            skLineSegment(sketch, "E229.0.47", {"start": v(125.41, 47.41) * mm, "end": v(125.07, 47.41) * mm});
            skLineSegment(sketch, "E229.0.48", {"start": v(125.07, 47.41) * mm, "end": v(123.72, 47.62) * mm});
            skLineSegment(sketch, "E229.0.49", {"start": v(123.72, 47.62) * mm, "end": v(122.36, 47.8) * mm});
            skLineSegment(sketch, "E229.0.50", {"start": v(122.36, 47.8) * mm, "end": v(119.74, 48.18) * mm});
            skLineSegment(sketch, "E229.0.51", {"start": v(119.74, 48.18) * mm, "end": v(114.66, 48.9) * mm});
            skLineSegment(sketch, "E229.0.52", {"start": v(114.66, 48.9) * mm, "end": v(109.5, 49.57) * mm});
            skLineSegment(sketch, "E229.0.53", {"start": v(109.5, 49.57) * mm, "end": v(104.29, 50.25) * mm});
            skLineSegment(sketch, "E229.0.54", {"start": v(104.29, 50.25) * mm, "end": v(93.83, 51.52) * mm});
            skLineSegment(sketch, "E229.0.55", {"start": v(93.83, 51.52) * mm, "end": v(88.54, 52.11) * mm});
            skLineSegment(sketch, "E229.0.56", {"start": v(88.54, 52.11) * mm, "end": v(83.25, 52.66) * mm});
            skLineSegment(sketch, "E229.0.57", {"start": v(83.25, 52.66) * mm, "end": v(77.96, 53.13) * mm});
            skLineSegment(sketch, "E229.0.58", {"start": v(77.96, 53.13) * mm, "end": v(72.67, 53.6) * mm});
            skLineSegment(sketch, "E229.0.59", {"start": v(72.67, 53.6) * mm, "end": v(67.42, 53.93) * mm});
            skLineSegment(sketch, "E229.0.60", {"start": v(67.42, 53.93) * mm, "end": v(62.2, 54.27) * mm});
            skLineSegment(sketch, "E229.0.61", {"start": v(62.2, 54.27) * mm, "end": v(56.96, 54.48) * mm});
            skLineSegment(sketch, "E229.0.62", {"start": v(56.96, 54.48) * mm, "end": v(51.75, 54.65) * mm});
            skLineSegment(sketch, "E229.0.63", {"start": v(51.75, 54.65) * mm, "end": v(46.5, 54.78) * mm});
            skLineSegment(sketch, "E229.0.64", {"start": v(46.5, 54.78) * mm, "end": v(41.21, 54.86) * mm});
            skLineSegment(sketch, "E229.0.65", {"start": v(41.21, 54.86) * mm, "end": v(35.88, 54.86) * mm});
            skLineSegment(sketch, "E229.0.66", {"start": v(35.88, 54.86) * mm, "end": v(30.46, 54.9) * mm});
            skLineSegment(sketch, "E229.0.67", {"start": v(30.46, 54.9) * mm, "end": v(29.1, 54.95) * mm});
            skLineSegment(sketch, "E229.0.68", {"start": v(29.1, 54.95) * mm, "end": v(27.8, 55.08) * mm});
            skLineSegment(sketch, "E229.0.69", {"start": v(27.8, 55.08) * mm, "end": v(26.52, 55.29) * mm});
            skLineSegment(sketch, "E229.0.70", {"start": v(26.52, 55.29) * mm, "end": v(25.25, 55.58) * mm});
            skLineSegment(sketch, "E229.0.71", {"start": v(25.25, 55.58) * mm, "end": v(24.07, 56) * mm});
            skLineSegment(sketch, "E229.0.72", {"start": v(24.07, 56) * mm, "end": v(22.88, 56.56) * mm});
            skLineSegment(sketch, "E229.0.73", {"start": v(22.88, 56.56) * mm, "end": v(21.78, 57.2) * mm});
            skLineSegment(sketch, "E229.0.74", {"start": v(21.78, 57.2) * mm, "end": v(20.72, 57.91) * mm});
            skLineSegment(sketch, "E229.0.75", {"start": v(20.72, 57.91) * mm, "end": v(19.66, 58.72) * mm});
            skLineSegment(sketch, "E229.0.76", {"start": v(19.66, 58.72) * mm, "end": v(18.65, 59.6) * mm});
            skLineSegment(sketch, "E229.0.77", {"start": v(18.65, 59.6) * mm, "end": v(16.62, 61.43) * mm});
            skLineSegment(sketch, "E229.0.78", {"start": v(16.62, 61.43) * mm, "end": v(14.63, 63.25) * mm});
            skLineSegment(sketch, "E229.0.79", {"start": v(14.63, 63.25) * mm, "end": v(13.61, 64.13) * mm});
            skLineSegment(sketch, "E229.0.80", {"start": v(13.61, 64.13) * mm, "end": v(12.55, 64.98) * mm});
            skLineSegment(sketch, "E229.0.81", {"start": v(12.55, 64.98) * mm, "end": v(11.5, 65.74) * mm});
            skLineSegment(sketch, "E229.0.82", {"start": v(11.5, 65.74) * mm, "end": v(10.4, 66.46) * mm});
            skLineSegment(sketch, "E229.0.83", {"start": v(10.4, 66.46) * mm, "end": v(9.25, 67.1) * mm});
            skLineSegment(sketch, "E229.0.84", {"start": v(9.25, 67.1) * mm, "end": v(8.1, 67.7) * mm});
            skLineSegment(sketch, "E229.0.85", {"start": v(8.1, 67.7) * mm, "end": v(6.88, 68.16) * mm});
            skLineSegment(sketch, "E229.0.86", {"start": v(6.88, 68.16) * mm, "end": v(5.65, 68.54) * mm});
            skLineSegment(sketch, "E229.0.87", {"start": v(5.65, 68.54) * mm, "end": v(4.38, 68.88) * mm});
            skLineSegment(sketch, "E229.0.88", {"start": v(4.38, 68.88) * mm, "end": v(3.07, 69.17) * mm});
            skLineSegment(sketch, "E229.0.89", {"start": v(3.07, 69.17) * mm, "end": v(0.44, 69.64) * mm});
            skLineSegment(sketch, "E229.0.90", {"start": v(0.44, 69.64) * mm, "end": v(-0.91, 69.85) * mm});
            skLineSegment(sketch, "E229.0.91", {"start": v(-0.91, 69.85) * mm, "end": v(-1.2, 69.9) * mm});
            skLineSegment(sketch, "E229.0.92", {"start": v(-1.2, 69.9) * mm, "end": v(-141.08, 69.9) * mm});
            skLineSegment(sketch, "E229.0.93", {"start": v(-141.08, 69.9) * mm, "end": v(-142, 69.8) * mm});
            skLineSegment(sketch, "E229.0.94", {"start": v(-142, 69.8) * mm, "end": v(-142.94, 69.6) * mm});
            skLineSegment(sketch, "E229.0.95", {"start": v(-142.94, 69.6) * mm, "end": v(-143.87, 69.3) * mm});
            skLineSegment(sketch, "E229.0.96", {"start": v(-143.87, 69.3) * mm, "end": v(-144.76, 68.96) * mm});
            skLineSegment(sketch, "E229.0.97", {"start": v(-144.76, 68.96) * mm, "end": v(-145.56, 68.5) * mm});
            skLineSegment(sketch, "E229.0.98", {"start": v(-145.56, 68.5) * mm, "end": v(-146.37, 67.94) * mm});
            skLineSegment(sketch, "E229.0.99", {"start": v(-146.37, 67.94) * mm, "end": v(-147.09, 67.3) * mm});
            skLineSegment(sketch, "E229.0.100", {"start": v(-147.09, 67.3) * mm, "end": v(-147.72, 66.67) * mm});
            skLineSegment(sketch, "E229.0.101", {"start": v(-147.72, 66.67) * mm, "end": v(-148.27, 65.96) * mm});
            skLineSegment(sketch, "E229.0.102", {"start": v(-148.27, 65.96) * mm, "end": v(-148.78, 65.15) * mm});
            skLineSegment(sketch, "E229.0.103", {"start": v(-148.78, 65.15) * mm, "end": v(-149.2, 64.3) * mm});
            skLineSegment(sketch, "E229.0.104", {"start": v(-149.2, 64.3) * mm, "end": v(-149.58, 63.42) * mm});
            skLineSegment(sketch, "E229.0.105", {"start": v(-149.58, 63.42) * mm, "end": v(-149.84, 62.48) * mm});
            skLineSegment(sketch, "E229.0.106", {"start": v(-149.84, 62.48) * mm, "end": v(-150, 61.55) * mm});
            skLineSegment(sketch, "E229.0.107", {"start": v(-150, 61.55) * mm, "end": v(-150.05, 60.62) * mm});
            skLineSegment(sketch, "E229.0.108", {"start": v(-150.05, 60.62) * mm, "end": v(-150, 59.69) * mm});
            skLineSegment(sketch, "E229.0.109", {"start": v(-150, 59.69) * mm, "end": v(-149.97, 59.22) * mm});
            skLineSegment(sketch, "E229.0.110", {"start": v(-149.97, 59.22) * mm, "end": v(-149.97, 58.97) * mm});
            skLineSegment(sketch, "E229.0.111", {"start": v(-149.97, 58.97) * mm, "end": v(-149.92, 58.89) * mm});
            skLineSegment(sketch, "E229.0.112", {"start": v(-149.92, 58.89) * mm, "end": v(-149.92, -19.9) * mm});
            skLineSegment(sketch, "E229.0.113", {"start": v(-149.92, -19.9) * mm, "end": v(-144.93, -19.9) * mm});
            skLineSegment(sketch, "E229.0.114", {"start": v(-144.93, -19.9) * mm, "end": v(-144.93, -29.89) * mm});
            skLineSegment(sketch, "E229.0.115", {"start": v(-144.93, -29.89) * mm, "end": v(-149.92, -29.89) * mm});
            skLineSegment(sketch, "E229.0.116", {"start": v(-149.92, -29.89) * mm, "end": v(-149.92, -39.88) * mm});
            skLineSegment(sketch, "E229.0.117", {"start": v(-149.92, -39.88) * mm, "end": v(-144.93, -39.88) * mm});
            skLineSegment(sketch, "E229.0.118", {"start": v(-144.93, -39.88) * mm, "end": v(-144.93, -49.91) * mm});
            skLineSegment(sketch, "E229.0.119", {"start": v(-144.93, -49.91) * mm, "end": v(-149.92, -49.91) * mm});
            skLineSegment(sketch, "E229.0.120", {"start": v(-149.92, -49.91) * mm, "end": v(-149.92, -59.9) * mm});
            skLineSegment(sketch, "E229.0.121", {"start": v(-149.92, -59.9) * mm, "end": v(-144.93, -59.9) * mm});
            skLineSegment(sketch, "E229.0.122", {"start": v(-144.93, -59.9) * mm, "end": v(-144.93, -69.9) * mm});
            skLineSegment(sketch, "E229.0.123", {"start": v(-144.93, -69.9) * mm, "end": v(145.06, -69.9) * mm});
            skLineSegment(sketch, "E229.0.124", {"start": v(145.06, -69.9) * mm, "end": v(145.06, -59.9) * mm});
            skCircle(sketch, "E230.0", {"center": v(70.05, 20.1) * mm, "radius": 4 * mm});
            skCircle(sketch, "E230.1", {"center": v(45.55, 20.1) * mm, "radius": 10.5 * mm, "construction": true});
            skCircle(sketch, "E230.2", {"center": v(21.05, 20.1) * mm, "radius": 4 * mm});
            skCircle(sketch, "E230.3", {"center": v(-19.95, -9.9) * mm, "radius": 6 * mm});
            skCircle(sketch, "E230.4", {"center": v(-94.95, -9.9) * mm, "radius": 10.5 * mm, "construction": true});
            skCircle(sketch, "E231", {"center": v(-94.95, -9.9) * mm, "radius": 6 * mm});
            skCircle(sketch, "E232", {"center": v(45.55, 20.1) * mm, "radius": 4 * mm});
            skSolve(sketch);
        }
        {
            var Q0;
            {var subQ0=sQuery(id+"F7.wireOp",EDGE,"E229.0.113");Q0=makeQuery(id+"F7.imprint","IMPRINT",FACE,{"disambiguationData":[TD([[makeQuery(id+"F7.imprint","IMPRINT",EDGE,{"derivedFrom":subQ0}),1.0]])]});}
            var Q1;
            Q1=makeQuery(id+"F7.imprint","IMPRINT",FACE,{"disambiguationData":[TD([[makeQuery(id+"F7.imprint","IMPRINT",EDGE,{"derivedFrom":sQuery(id+"F7.wireOp",EDGE,"E229.0.0")}),1.0]])]});
            extrude(context, id + "F8", {"entities" : qUnion([Q0, Q1]), "depth" : (getVariable(context, 'panel_thickness')) * mm, "offsetDistance" : 25 * mm});
        }
        {
            var Q0;
            Q0=makeQuery(id+"F6.opExtrude","SWEPT_FACE",FACE,{"disambiguationData":[OSD([sQuery(id+"F5.wireOp",EDGE,"E228.0")])]});
            var sketch = newSketch(context, id + "F9", { "sketchPlane" : qUnion([Q0])});
            skLineSegment(sketch, "E233.0", {"start": v(-149.93, -59.9) * mm, "end": v(-144.93, -59.9) * mm});
            skLineSegment(sketch, "E233.1", {"start": v(-149.93, -49.9) * mm, "end": v(-144.93, -49.9) * mm});
            skLineSegment(sketch, "E233.2", {"start": v(-149.93, -49.9) * mm, "end": v(-149.93, -59.9) * mm});
            skLineSegment(sketch, "E234.0", {"start": v(150.06, -49.9) * mm, "end": v(145.06, -49.9) * mm});
            skLineSegment(sketch, "E234.1", {"start": v(150.06, -49.9) * mm, "end": v(150.06, -59.9) * mm});
            skLineSegment(sketch, "E234.2", {"start": v(150.06, -59.9) * mm, "end": v(145.06, -59.9) * mm});
            skPoint(sketch, "E235.0", {"position": v(145.06, -69.9) * mm});
            skPoint(sketch, "E236.0", {"position": v(-144.93, -69.9) * mm});
            skLineSegment(sketch, "E237", {"start": v(-144.93, -59.9) * mm, "end": v(-144.93, -69.9) * mm});
            skLineSegment(sketch, "E238", {"start": v(-144.93, -49.9) * mm, "end": v(-144.93, -39.9) * mm});
            skLineSegment(sketch, "E239", {"start": v(-144.93, -39.9) * mm, "end": v(145.06, -39.9) * mm});
            skLineSegment(sketch, "E240", {"start": v(145.06, -39.9) * mm, "end": v(145.06, -49.9) * mm});
            skLineSegment(sketch, "E241", {"start": v(145.06, -59.9) * mm, "end": v(145.06, -69.9) * mm});
            skLineSegment(sketch, "E242", {"start": v(145.06, -69.9) * mm, "end": v(-144.93, -69.9) * mm});
            skSolve(sketch);
        }
        {
            var Q0;
            Q0=makeQuery(id+"F9.imprint","IMPRINT",FACE,{"disambiguationData":[TD([[makeQuery(id+"F9.imprint","IMPRINT",EDGE,{"derivedFrom":sQuery(id+"F9.wireOp",EDGE,"E234.0")}),1.0]])]});
            var Q1;
            Q1=makeQuery(id+"F9.imprint","IMPRINT",FACE,{"disambiguationData":[TD([[makeQuery(id+"F9.imprint","IMPRINT",EDGE,{"derivedFrom":sQuery(id+"F9.wireOp",EDGE,"E233.0")}),1.0]])]});
            extrude(context, id + "F10", {"entities" : qUnion([Q0, Q1]), "depth" : (getVariable(context, 'panel_thickness')) * mm, "offsetDistance" : 25 * mm});
        }
        {
            var Q0;
            Q0=makeQuery(id+"F6.opExtrude","SWEPT_FACE",FACE,{"disambiguationData":[OSD([sQuery(id+"F5.wireOp",EDGE,"E228.5")])]});
            var sketch = newSketch(context, id + "F11", { "sketchPlane" : qUnion([Q0])});
            skLineSegment(sketch, "E243.0.0", {"start": v(-144.93, -39.9) * mm, "end": v(-144.93, -49.9) * mm});
            skLineSegment(sketch, "E243.0.1", {"start": v(-144.93, -49.9) * mm, "end": v(-149.93, -49.9) * mm});
            skLineSegment(sketch, "E243.0.2", {"start": v(-149.93, -49.9) * mm, "end": v(-149.93, -59.9) * mm});
            skLineSegment(sketch, "E243.0.3", {"start": v(-149.93, -59.9) * mm, "end": v(-144.93, -59.9) * mm});
            skLineSegment(sketch, "E243.0.4", {"start": v(-144.93, -59.9) * mm, "end": v(-144.93, -69.9) * mm});
            skLineSegment(sketch, "E243.0.5", {"start": v(-144.93, -69.9) * mm, "end": v(145.06, -69.9) * mm});
            skLineSegment(sketch, "E243.0.6", {"start": v(145.06, -69.9) * mm, "end": v(145.06, -59.9) * mm});
            skLineSegment(sketch, "E243.0.7", {"start": v(145.06, -59.9) * mm, "end": v(150.06, -59.9) * mm});
            skLineSegment(sketch, "E243.0.8", {"start": v(150.06, -59.9) * mm, "end": v(150.06, -49.9) * mm});
            skLineSegment(sketch, "E243.0.9", {"start": v(150.06, -49.9) * mm, "end": v(145.06, -49.9) * mm});
            skLineSegment(sketch, "E243.0.10", {"start": v(145.06, -49.9) * mm, "end": v(145.06, -39.9) * mm});
            skLineSegment(sketch, "E243.0.11", {"start": v(145.06, -39.9) * mm, "end": v(-144.93, -39.9) * mm});
            skSolve(sketch);
        }
        {
            var Q0;
            Q0=makeQuery(id+"F11.imprint","IMPRINT",FACE,{"disambiguationData":[TD([[makeQuery(id+"F11.imprint","IMPRINT",EDGE,{"derivedFrom":sQuery(id+"F11.wireOp",EDGE,"E243.0.0")}),1.0]])]});
            var Q1;
            Q1=makeQuery(id+"F11.imprint","IMPRINT",FACE,{"disambiguationData":[TD([[makeQuery(id+"F11.imprint","IMPRINT",EDGE,{"derivedFrom":sQuery(id+"F11.wireOp",EDGE,"E243.0.1")}),-1.0]])]});
            extrude(context, id + "F12", {"entities" : qUnion([Q0, Q1]), "depth" : (getVariable(context, 'panel_thickness')) * mm, "offsetDistance" : 25 * mm});
        }
        {
            var Q0;
            Q0=makeQuery(id+"F6.opExtrude","SWEPT_FACE",FACE,{"disambiguationData":[OSD([sQuery(id+"F5.wireOp",EDGE,"E228.9")])]});
            var sketch = newSketch(context, id + "F13", { "sketchPlane" : qUnion([Q0])});
            skLineSegment(sketch, "E244.0.0", {"start": v(-144.93, -39.9) * mm, "end": v(-144.93, -49.9) * mm});
            skLineSegment(sketch, "E244.0.1", {"start": v(-144.93, -49.9) * mm, "end": v(-149.93, -49.9) * mm});
            skLineSegment(sketch, "E244.0.2", {"start": v(-149.93, -49.9) * mm, "end": v(-149.93, -59.9) * mm});
            skLineSegment(sketch, "E244.0.3", {"start": v(-149.93, -59.9) * mm, "end": v(-144.93, -59.9) * mm});
            skLineSegment(sketch, "E244.0.4", {"start": v(-144.93, -59.9) * mm, "end": v(-144.93, -69.9) * mm});
            skLineSegment(sketch, "E244.0.5", {"start": v(-144.93, -69.9) * mm, "end": v(145.06, -69.9) * mm});
            skLineSegment(sketch, "E244.0.6", {"start": v(145.06, -69.9) * mm, "end": v(145.06, -59.9) * mm});
            skLineSegment(sketch, "E244.0.7", {"start": v(145.06, -59.9) * mm, "end": v(150.06, -59.9) * mm});
            skLineSegment(sketch, "E244.0.8", {"start": v(150.06, -59.9) * mm, "end": v(150.06, -49.9) * mm});
            skLineSegment(sketch, "E244.0.9", {"start": v(150.06, -49.9) * mm, "end": v(145.06, -49.9) * mm});
            skLineSegment(sketch, "E244.0.10", {"start": v(145.06, -49.9) * mm, "end": v(145.06, -39.9) * mm});
            skLineSegment(sketch, "E244.0.11", {"start": v(145.06, -39.9) * mm, "end": v(-144.93, -39.9) * mm});
            skSolve(sketch);
        }
        {
            var Q0;
            Q0=makeQuery(id+"F13.imprint","IMPRINT",FACE,{"disambiguationData":[TD([[makeQuery(id+"F13.imprint","IMPRINT",EDGE,{"derivedFrom":sQuery(id+"F13.wireOp",EDGE,"E244.0.0")}),1.0]])]});
            var Q1;
            Q1=makeQuery(id+"F13.imprint","IMPRINT",FACE,{"disambiguationData":[TD([[makeQuery(id+"F13.imprint","IMPRINT",EDGE,{"derivedFrom":sQuery(id+"F13.wireOp",EDGE,"E244.0.1")}),-1.0]])]});
            extrude(context, id + "F14", {"entities" : qUnion([Q0, Q1]), "depth" : (getVariable(context, 'panel_thickness')) * mm, "offsetDistance" : 25 * mm});
        }
        {
            var Q0;
            Q0=makeQuery(id+"F6.opExtrude","SWEPT_FACE",FACE,{"disambiguationData":[OSD([sQuery(id+"F5.wireOp",EDGE,"E228.13")])]});
            var sketch = newSketch(context, id + "F15", { "sketchPlane" : qUnion([Q0])});
            skLineSegment(sketch, "E245.0.0", {"start": v(-144.93, -39.9) * mm, "end": v(-144.93, -49.9) * mm});
            skLineSegment(sketch, "E245.0.1", {"start": v(-144.93, -49.9) * mm, "end": v(-149.93, -49.9) * mm});
            skLineSegment(sketch, "E245.0.2", {"start": v(-149.93, -49.9) * mm, "end": v(-149.93, -59.9) * mm});
            skLineSegment(sketch, "E245.0.3", {"start": v(-149.93, -59.9) * mm, "end": v(-144.93, -59.9) * mm});
            skLineSegment(sketch, "E245.0.4", {"start": v(-144.93, -59.9) * mm, "end": v(-144.93, -69.9) * mm});
            skLineSegment(sketch, "E245.0.5", {"start": v(-144.93, -69.9) * mm, "end": v(145.06, -69.9) * mm});
            skLineSegment(sketch, "E245.0.6", {"start": v(145.06, -69.9) * mm, "end": v(145.06, -59.9) * mm});
            skLineSegment(sketch, "E245.0.7", {"start": v(145.06, -59.9) * mm, "end": v(150.06, -59.9) * mm});
            skLineSegment(sketch, "E245.0.8", {"start": v(150.06, -59.9) * mm, "end": v(150.06, -49.9) * mm});
            skLineSegment(sketch, "E245.0.9", {"start": v(150.06, -49.9) * mm, "end": v(145.06, -49.9) * mm});
            skLineSegment(sketch, "E245.0.10", {"start": v(145.06, -49.9) * mm, "end": v(145.06, -39.9) * mm});
            skLineSegment(sketch, "E245.0.11", {"start": v(145.06, -39.9) * mm, "end": v(-144.93, -39.9) * mm});
            skSolve(sketch);
        }
        {
            var Q0;
            Q0=makeQuery(id+"F15.imprint","IMPRINT",FACE,{"disambiguationData":[TD([[makeQuery(id+"F15.imprint","IMPRINT",EDGE,{"derivedFrom":sQuery(id+"F15.wireOp",EDGE,"E245.0.0")}),1.0]])]});
            var Q1;
            Q1=makeQuery(id+"F15.imprint","IMPRINT",FACE,{"disambiguationData":[TD([[makeQuery(id+"F15.imprint","IMPRINT",EDGE,{"derivedFrom":sQuery(id+"F15.wireOp",EDGE,"E245.0.1")}),-1.0]])]});
            extrude(context, id + "F16", {"entities" : qUnion([Q0, Q1]), "depth" : (getVariable(context, 'panel_thickness')) * mm, "offsetDistance" : 25 * mm});
        }
        {
            var Q0;
            Q0=makeQuery(id+"F6.opExtrude","SWEPT_FACE",FACE,{"disambiguationData":[OSD([sQuery(id+"F5.wireOp",EDGE,"E228.18")])]});
            var sketch = newSketch(context, id + "F17", { "sketchPlane" : qUnion([Q0])});
            skLineSegment(sketch, "E246.0.0", {"start": v(-144.93, -39.9) * mm, "end": v(-144.93, -49.9) * mm});
            skLineSegment(sketch, "E246.0.1", {"start": v(-144.93, -49.9) * mm, "end": v(-149.93, -49.9) * mm});
            skLineSegment(sketch, "E246.0.2", {"start": v(-149.93, -49.9) * mm, "end": v(-149.93, -59.9) * mm});
            skLineSegment(sketch, "E246.0.3", {"start": v(-149.93, -59.9) * mm, "end": v(-144.93, -59.9) * mm});
            skLineSegment(sketch, "E246.0.4", {"start": v(-144.93, -59.9) * mm, "end": v(-144.93, -69.9) * mm});
            skLineSegment(sketch, "E246.0.5", {"start": v(-144.93, -69.9) * mm, "end": v(145.06, -69.9) * mm});
            skLineSegment(sketch, "E246.0.6", {"start": v(145.06, -69.9) * mm, "end": v(145.06, -59.9) * mm});
            skLineSegment(sketch, "E246.0.7", {"start": v(145.06, -59.9) * mm, "end": v(150.06, -59.9) * mm});
            skLineSegment(sketch, "E246.0.8", {"start": v(150.06, -59.9) * mm, "end": v(150.06, -49.9) * mm});
            skLineSegment(sketch, "E246.0.9", {"start": v(150.06, -49.9) * mm, "end": v(145.06, -49.9) * mm});
            skLineSegment(sketch, "E246.0.10", {"start": v(145.06, -49.9) * mm, "end": v(145.06, -39.9) * mm});
            skLineSegment(sketch, "E246.0.11", {"start": v(145.06, -39.9) * mm, "end": v(-144.93, -39.9) * mm});
            skSolve(sketch);
        }
        {
            var Q0;
            Q0=makeQuery(id+"F17.imprint","IMPRINT",FACE,{"disambiguationData":[TD([[makeQuery(id+"F17.imprint","IMPRINT",EDGE,{"derivedFrom":sQuery(id+"F17.wireOp",EDGE,"E246.0.0")}),1.0]])]});
            var Q1;
            Q1=makeQuery(id+"F17.imprint","IMPRINT",FACE,{"disambiguationData":[TD([[makeQuery(id+"F17.imprint","IMPRINT",EDGE,{"derivedFrom":sQuery(id+"F17.wireOp",EDGE,"E246.0.1")}),-1.0]])]});
            extrude(context, id + "F18", {"entities" : qUnion([Q0, Q1]), "depth" : (getVariable(context, 'panel_thickness')) * mm, "offsetDistance" : 25 * mm});
        }
        {
            var Q0;
            Q0=makeQuery(id+"F2.opExtrude","CAP_FACE",FACE,{"disambiguationData":[OSD([sQuery(id+"F1.wireOp",EDGE,"E0"),sQuery(id+"F1.wireOp",EDGE,"E1"),sQuery(id+"F1.wireOp",EDGE,"E2"),sQuery(id+"F1.wireOp",EDGE,"E3"),sQuery(id+"F1.wireOp",EDGE,"E4"),sQuery(id+"F1.wireOp",EDGE,"E5"),sQuery(id+"F1.wireOp",EDGE,"E6"),sQuery(id+"F1.wireOp",EDGE,"E7"),sQuery(id+"F1.wireOp",EDGE,"E8"),sQuery(id+"F1.wireOp",EDGE,"E9"),sQuery(id+"F1.wireOp",EDGE,"E10"),sQuery(id+"F1.wireOp",EDGE,"E11"),sQuery(id+"F1.wireOp",EDGE,"E12"),sQuery(id+"F1.wireOp",EDGE,"E13"),sQuery(id+"F1.wireOp",EDGE,"E14"),sQuery(id+"F1.wireOp",EDGE,"E15"),sQuery(id+"F1.wireOp",EDGE,"E16"),sQuery(id+"F1.wireOp",EDGE,"E17"),sQuery(id+"F1.wireOp",EDGE,"E18"),sQuery(id+"F1.wireOp",EDGE,"E19"),sQuery(id+"F1.wireOp",EDGE,"E20"),sQuery(id+"F1.wireOp",EDGE,"E21"),sQuery(id+"F1.wireOp",EDGE,"E22"),sQuery(id+"F1.wireOp",EDGE,"E23"),sQuery(id+"F1.wireOp",EDGE,"E24"),sQuery(id+"F1.wireOp",EDGE,"E25"),sQuery(id+"F1.wireOp",EDGE,"E26"),sQuery(id+"F1.wireOp",EDGE,"E27"),sQuery(id+"F1.wireOp",EDGE,"E28"),sQuery(id+"F1.wireOp",EDGE,"E29"),sQuery(id+"F1.wireOp",EDGE,"E30"),sQuery(id+"F1.wireOp",EDGE,"E31"),sQuery(id+"F1.wireOp",EDGE,"E32"),sQuery(id+"F1.wireOp",EDGE,"E33"),sQuery(id+"F1.wireOp",EDGE,"E34"),sQuery(id+"F1.wireOp",EDGE,"E35"),sQuery(id+"F1.wireOp",EDGE,"E36"),sQuery(id+"F1.wireOp",EDGE,"E37"),sQuery(id+"F1.wireOp",EDGE,"E38"),sQuery(id+"F1.wireOp",EDGE,"E39"),sQuery(id+"F1.wireOp",EDGE,"E40"),sQuery(id+"F1.wireOp",EDGE,"E41"),sQuery(id+"F1.wireOp",EDGE,"E42"),sQuery(id+"F1.wireOp",EDGE,"E43"),sQuery(id+"F1.wireOp",EDGE,"E44"),sQuery(id+"F1.wireOp",EDGE,"E45"),sQuery(id+"F1.wireOp",EDGE,"E46"),sQuery(id+"F1.wireOp",EDGE,"E47"),sQuery(id+"F1.wireOp",EDGE,"E48"),sQuery(id+"F1.wireOp",EDGE,"E49"),sQuery(id+"F1.wireOp",EDGE,"E50"),sQuery(id+"F1.wireOp",EDGE,"E51"),sQuery(id+"F1.wireOp",EDGE,"E52"),sQuery(id+"F1.wireOp",EDGE,"E53"),sQuery(id+"F1.wireOp",EDGE,"E54"),sQuery(id+"F1.wireOp",EDGE,"E55"),sQuery(id+"F1.wireOp",EDGE,"E56"),sQuery(id+"F1.wireOp",EDGE,"E57"),sQuery(id+"F1.wireOp",EDGE,"E58"),sQuery(id+"F1.wireOp",EDGE,"E59"),sQuery(id+"F1.wireOp",EDGE,"E60"),sQuery(id+"F1.wireOp",EDGE,"E61"),sQuery(id+"F1.wireOp",EDGE,"E62"),sQuery(id+"F1.wireOp",EDGE,"E63"),sQuery(id+"F1.wireOp",EDGE,"E64"),sQuery(id+"F1.wireOp",EDGE,"E65"),sQuery(id+"F1.wireOp",EDGE,"E66"),sQuery(id+"F1.wireOp",EDGE,"E67"),sQuery(id+"F1.wireOp",EDGE,"E68"),sQuery(id+"F1.wireOp",EDGE,"E69"),sQuery(id+"F1.wireOp",EDGE,"E70"),sQuery(id+"F1.wireOp",EDGE,"E71"),sQuery(id+"F1.wireOp",EDGE,"E72"),sQuery(id+"F1.wireOp",EDGE,"E73"),sQuery(id+"F1.wireOp",EDGE,"E74"),sQuery(id+"F1.wireOp",EDGE,"E75"),sQuery(id+"F1.wireOp",EDGE,"E76"),sQuery(id+"F1.wireOp",EDGE,"E77"),sQuery(id+"F1.wireOp",EDGE,"E78"),sQuery(id+"F1.wireOp",EDGE,"E79"),sQuery(id+"F1.wireOp",EDGE,"E80"),sQuery(id+"F1.wireOp",EDGE,"E81"),sQuery(id+"F1.wireOp",EDGE,"E82"),sQuery(id+"F1.wireOp",EDGE,"E83"),sQuery(id+"F1.wireOp",EDGE,"E84"),sQuery(id+"F1.wireOp",EDGE,"E85"),sQuery(id+"F1.wireOp",EDGE,"E86"),sQuery(id+"F1.wireOp",EDGE,"E87"),sQuery(id+"F1.wireOp",EDGE,"E88"),sQuery(id+"F1.wireOp",EDGE,"E89"),sQuery(id+"F1.wireOp",EDGE,"E90"),sQuery(id+"F1.wireOp",EDGE,"E91"),sQuery(id+"F1.wireOp",EDGE,"E92"),sQuery(id+"F1.wireOp",EDGE,"E93"),sQuery(id+"F1.wireOp",EDGE,"E94"),sQuery(id+"F1.wireOp",EDGE,"E95"),sQuery(id+"F1.wireOp",EDGE,"E96"),sQuery(id+"F1.wireOp",EDGE,"E97"),sQuery(id+"F1.wireOp",EDGE,"E98"),sQuery(id+"F1.wireOp",EDGE,"E99"),sQuery(id+"F1.wireOp",EDGE,"E100"),sQuery(id+"F1.wireOp",EDGE,"E101"),sQuery(id+"F1.wireOp",EDGE,"E102"),sQuery(id+"F1.wireOp",EDGE,"E103"),sQuery(id+"F1.wireOp",EDGE,"E104"),sQuery(id+"F1.wireOp",EDGE,"E105"),sQuery(id+"F1.wireOp",EDGE,"E106"),sQuery(id+"F1.wireOp",EDGE,"E107"),sQuery(id+"F1.wireOp",EDGE,"E108"),sQuery(id+"F1.wireOp",EDGE,"E109"),sQuery(id+"F1.wireOp",EDGE,"E110"),sQuery(id+"F1.wireOp",EDGE,"E111"),sQuery(id+"F1.wireOp",EDGE,"E112"),sQuery(id+"F1.wireOp",EDGE,"E113"),sQuery(id+"F1.wireOp",EDGE,"E114"),sQuery(id+"F1.wireOp",EDGE,"E115"),sQuery(id+"F1.wireOp",EDGE,"E116"),sQuery(id+"F1.wireOp",EDGE,"E117"),sQuery(id+"F1.wireOp",EDGE,"E118"),sQuery(id+"F1.wireOp",EDGE,"E119"),sQuery(id+"F1.wireOp",EDGE,"E120"),sQuery(id+"F1.wireOp",EDGE,"E121"),sQuery(id+"F1.wireOp",EDGE,"E122"),sQuery(id+"F1.wireOp",EDGE,"E123"),sQuery(id+"F1.wireOp",EDGE,"E124"),sQuery(id+"F1.wireOp",EDGE,"E125"),sQuery(id+"F1.wireOp",EDGE,"E126"),sQuery(id+"F1.wireOp",EDGE,"E127"),sQuery(id+"F1.wireOp",EDGE,"E128"),sQuery(id+"F1.wireOp",EDGE,"E129"),sQuery(id+"F1.wireOp",EDGE,"E130"),sQuery(id+"F1.wireOp",EDGE,"E131"),sQuery(id+"F1.wireOp",EDGE,"E132"),sQuery(id+"F1.wireOp",EDGE,"E133"),sQuery(id+"F1.wireOp",EDGE,"E134"),sQuery(id+"F1.wireOp",EDGE,"E135"),sQuery(id+"F1.wireOp",EDGE,"E136"),sQuery(id+"F1.wireOp",EDGE,"E137"),sQuery(id+"F1.wireOp",EDGE,"E138"),sQuery(id+"F1.wireOp",EDGE,"E139"),sQuery(id+"F1.wireOp",EDGE,"E140"),sQuery(id+"F1.wireOp",EDGE,"E141"),sQuery(id+"F1.wireOp",EDGE,"E142"),sQuery(id+"F1.wireOp",EDGE,"E143"),sQuery(id+"F1.wireOp",EDGE,"E144"),sQuery(id+"F1.wireOp",EDGE,"E145"),sQuery(id+"F1.wireOp",EDGE,"E146"),sQuery(id+"F1.wireOp",EDGE,"E147"),sQuery(id+"F1.wireOp",EDGE,"E148"),sQuery(id+"F1.wireOp",EDGE,"E149"),sQuery(id+"F1.wireOp",EDGE,"E150"),sQuery(id+"F1.wireOp",EDGE,"E151"),sQuery(id+"F1.wireOp",EDGE,"E152"),sQuery(id+"F1.wireOp",EDGE,"E153"),sQuery(id+"F1.wireOp",EDGE,"E155"),sQuery(id+"F1.wireOp",EDGE,"E157"),sQuery(id+"F1.wireOp",EDGE,"E159"),sQuery(id+"F1.wireOp",EDGE,"E163"),sQuery(id+"F1.wireOp",EDGE,"E164"),sQuery(id+"F1.wireOp",EDGE,"E165"),sQuery(id+"F1.wireOp",EDGE,"E168"),sQuery(id+"F1.wireOp",EDGE,"E170"),sQuery(id+"F1.wireOp",EDGE,"E175"),sQuery(id+"F1.wireOp",EDGE,"E176"),sQuery(id+"F1.wireOp",EDGE,"E177"),sQuery(id+"F1.wireOp",EDGE,"E178")])],"isStart":false});
            var sketch = newSketch(context, id + "F19", { "sketchPlane" : qUnion([Q0])});
            skLineSegment(sketch, "E247.bottom", {"start": v(-25.55, 40.1) * mm, "end": v(-65.55, 40.1) * mm});
            skLineSegment(sketch, "E247.top", {"start": v(-25.55, 0.1) * mm, "end": v(-65.55, 0.1) * mm});
            skLineSegment(sketch, "E247.left", {"start": v(-25.55, 40.1) * mm, "end": v(-25.55, 0.1) * mm});
            skLineSegment(sketch, "E247.right", {"start": v(-65.55, 40.1) * mm, "end": v(-65.55, 0.1) * mm});
            skPoint(sketch, "E247.middle", {"position": v(-45.55, 20.1) * mm});
            skLineSegment(sketch, "E248.bottom", {"start": v(114.95, 10.1) * mm, "end": v(74.95, 10.1) * mm});
            skLineSegment(sketch, "E248.top", {"start": v(114.95, -29.9) * mm, "end": v(74.95, -29.9) * mm});
            skLineSegment(sketch, "E248.left", {"start": v(114.95, 10.1) * mm, "end": v(114.95, -29.9) * mm});
            skLineSegment(sketch, "E248.right", {"start": v(74.95, 10.1) * mm, "end": v(74.95, -29.9) * mm});
            skPoint(sketch, "E248.middle", {"position": v(94.95, -9.9) * mm});
            skPoint(sketch, "E249.visualSharp", {"position": v(-65.55, 40.1) * mm});
            skPoint(sketch, "E250.visualSharp", {"position": v(-25.55, 40.1) * mm});
            skSolve(sketch);
        }
        {
            var Q0;
            Q0=makeQuery(id+"F19.imprint","IMPRINT",FACE,{"disambiguationData":[TD([[makeQuery(id+"F19.imprint","IMPRINT",EDGE,{"derivedFrom":sQuery(id+"F19.wireOp",EDGE,"E247.bottom")}),1.0]])]});
            var Q1;
            Q1=makeQuery(id+"F19.imprint","IMPRINT",FACE,{"disambiguationData":[TD([[makeQuery(id+"F19.imprint","IMPRINT",EDGE,{"derivedFrom":sQuery(id+"F19.wireOp",EDGE,"E248.bottom")}),1.0]])]});
            var Q2;
            Q2=makeQuery(id+"F19.imprint","IMPRINT",FACE,{"disambiguationData":[TD([[makeQuery(id+"F19.imprint","IMPRINT",EDGE,{"derivedFrom":makeQuery(id+"F2.opExtrude","CAP_EDGE",EDGE,{"disambiguationData":[OSD([sQuery(id+"F1.wireOp",EDGE,"E153")])],"isStart":false})}),1.0]])]});
            var Q3;
            Q3=makeQuery(id+"F19.imprint","IMPRINT",FACE,{"disambiguationData":[TD([[makeQuery(id+"F19.imprint","IMPRINT",EDGE,{"derivedFrom":makeQuery(id+"F2.opExtrude","CAP_EDGE",EDGE,{"disambiguationData":[OSD([sQuery(id+"F1.wireOp",EDGE,"E170")])],"isStart":false})}),1.0]])]});
            var Q4;
            Q4=makeQuery(id+"F19.imprint","IMPRINT",FACE,{"disambiguationData":[TD([[makeQuery(id+"F19.imprint","IMPRINT",EDGE,{"derivedFrom":makeQuery(id+"F2.opExtrude","CAP_EDGE",EDGE,{"disambiguationData":[OSD([sQuery(id+"F1.wireOp",EDGE,"E163")])],"isStart":false})}),1.0]])]});
            var Q5;
            Q5=makeQuery(id+"F19.imprint","IMPRINT",FACE,{"disambiguationData":[TD([[makeQuery(id+"F19.imprint","IMPRINT",EDGE,{"derivedFrom":makeQuery(id+"F2.opExtrude","CAP_EDGE",EDGE,{"disambiguationData":[OSD([sQuery(id+"F1.wireOp",EDGE,"E159")])],"isStart":false})}),1.0]])]});
            var Q6;
            Q6=makeQuery(id+"F19.imprint","IMPRINT",FACE,{"disambiguationData":[TD([[makeQuery(id+"F19.imprint","IMPRINT",EDGE,{"derivedFrom":makeQuery(id+"F2.opExtrude","CAP_EDGE",EDGE,{"disambiguationData":[OSD([sQuery(id+"F1.wireOp",EDGE,"E165")])],"isStart":false})}),1.0]])]});
            var Q7;
            Q7=makeQuery(id+"F19.imprint","IMPRINT",FACE,{"disambiguationData":[TD([[makeQuery(id+"F19.imprint","IMPRINT",EDGE,{"derivedFrom":makeQuery(id+"F2.opExtrude","CAP_EDGE",EDGE,{"disambiguationData":[OSD([sQuery(id+"F1.wireOp",EDGE,"E164")])],"isStart":false})}),1.0]])]});
            var Q8;
            Q8=makeQuery(id+"F19.imprint","IMPRINT",FACE,{"disambiguationData":[TD([[makeQuery(id+"F19.imprint","IMPRINT",EDGE,{"derivedFrom":makeQuery(id+"F2.opExtrude","CAP_EDGE",EDGE,{"disambiguationData":[OSD([sQuery(id+"F1.wireOp",EDGE,"E178")])],"isStart":false})}),1.0]])]});
            var Q9;
            Q9=makeQuery(id+"F19.imprint","IMPRINT",FACE,{"disambiguationData":[TD([[makeQuery(id+"F19.imprint","IMPRINT",EDGE,{"derivedFrom":makeQuery(id+"F2.opExtrude","CAP_EDGE",EDGE,{"disambiguationData":[OSD([sQuery(id+"F1.wireOp",EDGE,"E175")])],"isStart":false})}),1.0]])]});
            var Q10;
            Q10=makeQuery(id+"F19.imprint","IMPRINT",FACE,{"disambiguationData":[TD([[makeQuery(id+"F19.imprint","IMPRINT",EDGE,{"derivedFrom":makeQuery(id+"F2.opExtrude","CAP_EDGE",EDGE,{"disambiguationData":[OSD([sQuery(id+"F1.wireOp",EDGE,"E176")])],"isStart":false})}),1.0]])]});
            var Q11;
            Q11=makeQuery(id+"F19.imprint","IMPRINT",FACE,{"disambiguationData":[TD([[makeQuery(id+"F19.imprint","IMPRINT",EDGE,{"derivedFrom":makeQuery(id+"F2.opExtrude","CAP_EDGE",EDGE,{"disambiguationData":[OSD([sQuery(id+"F1.wireOp",EDGE,"E177")])],"isStart":false})}),1.0]])]});
            extrude(context, id + "F20", {"entities" : qUnion([Q0, Q1, Q2, Q3, Q4, Q5, Q6, Q7, Q8, Q9, Q10, Q11]), "depth" : 34 * mm, "offsetDistance" : 25 * mm});
        }
        {
            var Q0;
            Q0=makeQuery(id+"F20.opExtrude","SWEPT_EDGE",EDGE,{"disambiguationData":[OSD([sQuery(id+"F19.wireOp",EDGE,"E247.bottom"),sQuery(id+"F19.wireOp",EDGE,"E247.right")])]});
            var Q1;
            Q1=makeQuery(id+"F20.opExtrude","SWEPT_EDGE",EDGE,{"disambiguationData":[OSD([sQuery(id+"F19.wireOp",EDGE,"E247.top"),sQuery(id+"F19.wireOp",EDGE,"E247.right")])]});
            var Q2;
            Q2=makeQuery(id+"F20.opExtrude","SWEPT_EDGE",EDGE,{"disambiguationData":[OSD([sQuery(id+"F19.wireOp",EDGE,"E247.bottom"),sQuery(id+"F19.wireOp",EDGE,"E247.left")])]});
            var Q3;
            Q3=makeQuery(id+"F20.opExtrude","SWEPT_EDGE",EDGE,{"disambiguationData":[OSD([sQuery(id+"F19.wireOp",EDGE,"E247.top"),sQuery(id+"F19.wireOp",EDGE,"E247.left")])]});
            var Q4;
            Q4=makeQuery(id+"F20.opExtrude","SWEPT_EDGE",EDGE,{"disambiguationData":[OSD([sQuery(id+"F19.wireOp",EDGE,"E248.bottom"),sQuery(id+"F19.wireOp",EDGE,"E248.left")])]});
            var Q5;
            Q5=makeQuery(id+"F20.opExtrude","SWEPT_EDGE",EDGE,{"disambiguationData":[OSD([sQuery(id+"F19.wireOp",EDGE,"E248.top"),sQuery(id+"F19.wireOp",EDGE,"E248.left")])]});
            var Q6;
            Q6=makeQuery(id+"F20.opExtrude","SWEPT_EDGE",EDGE,{"disambiguationData":[OSD([sQuery(id+"F19.wireOp",EDGE,"E248.bottom"),sQuery(id+"F19.wireOp",EDGE,"E248.right")])]});
            var Q7;
            Q7=makeQuery(id+"F20.opExtrude","SWEPT_EDGE",EDGE,{"disambiguationData":[OSD([sQuery(id+"F19.wireOp",EDGE,"E248.top"),sQuery(id+"F19.wireOp",EDGE,"E248.right")])]});
            fillet(context, id + "F21", {"entities" : qUnion([Q0, Q1, Q2, Q3, Q4, Q5, Q6, Q7]), "radius" : 5 * mm, "tangentPropagation" : true, "allowEdgeOverflow" : false});
        }
        {
            var Q0;
            Q0=makeQuery(id+"F20.opExtrude","CAP_FACE",FACE,{"disambiguationData":[OSD([sQuery(id+"F19.wireOp",EDGE,"E248.bottom"),sQuery(id+"F19.wireOp",EDGE,"E248.top"),sQuery(id+"F19.wireOp",EDGE,"E248.left"),sQuery(id+"F19.wireOp",EDGE,"E248.right")])],"isStart":true});
            var sketch = newSketch(context, id + "F22", { "sketchPlane" : qUnion([Q0])});
            skCircle(sketch, "E251.0", {"center": v(-94.95, -9.9) * mm, "radius": 10.5 * mm, "construction": true});
            skCircle(sketch, "E251.1", {"center": v(45.55, 20.1) * mm, "radius": 10.5 * mm, "construction": true});
            skCircle(sketch, "E252", {"center": v(-94.95, -9.9) * mm, "radius": 2.5 * mm});
            skCircle(sketch, "E253", {"center": v(45.55, 20.1) * mm, "radius": 2.5 * mm});
            skSolve(sketch);
        }
        {
            var Q0;
            Q0=makeQuery(id+"F22.imprint","IMPRINT",FACE,{"disambiguationData":[TD([[makeQuery(id+"F22.imprint","IMPRINT",EDGE,{"derivedFrom":sQuery(id+"F22.wireOp",EDGE,"E252")}),1.0]])]});
            var Q1;
            Q1=makeQuery(id+"F22.imprint","IMPRINT",FACE,{"disambiguationData":[TD([[makeQuery(id+"F22.imprint","IMPRINT",EDGE,{"derivedFrom":sQuery(id+"F22.wireOp",EDGE,"E253")}),1.0]])]});
            extrude(context, id + "F23", {"entities" : qUnion([Q0, Q1]), "operationType" : NewBodyOperationType.ADD, "depth" : 24 * mm, "offsetDistance" : 25 * mm});
        }
        {
            var Q0;
            Q0=makeQuery(id+"F2.opExtrude","CAP_FACE",FACE,{"disambiguationData":[OSD([sQuery(id+"F1.wireOp",EDGE,"E0"),sQuery(id+"F1.wireOp",EDGE,"E1"),sQuery(id+"F1.wireOp",EDGE,"E2"),sQuery(id+"F1.wireOp",EDGE,"E3"),sQuery(id+"F1.wireOp",EDGE,"E4"),sQuery(id+"F1.wireOp",EDGE,"E5"),sQuery(id+"F1.wireOp",EDGE,"E6"),sQuery(id+"F1.wireOp",EDGE,"E7"),sQuery(id+"F1.wireOp",EDGE,"E8"),sQuery(id+"F1.wireOp",EDGE,"E9"),sQuery(id+"F1.wireOp",EDGE,"E10"),sQuery(id+"F1.wireOp",EDGE,"E11"),sQuery(id+"F1.wireOp",EDGE,"E12"),sQuery(id+"F1.wireOp",EDGE,"E13"),sQuery(id+"F1.wireOp",EDGE,"E14"),sQuery(id+"F1.wireOp",EDGE,"E15"),sQuery(id+"F1.wireOp",EDGE,"E16"),sQuery(id+"F1.wireOp",EDGE,"E17"),sQuery(id+"F1.wireOp",EDGE,"E18"),sQuery(id+"F1.wireOp",EDGE,"E19"),sQuery(id+"F1.wireOp",EDGE,"E20"),sQuery(id+"F1.wireOp",EDGE,"E21"),sQuery(id+"F1.wireOp",EDGE,"E22"),sQuery(id+"F1.wireOp",EDGE,"E23"),sQuery(id+"F1.wireOp",EDGE,"E24"),sQuery(id+"F1.wireOp",EDGE,"E25"),sQuery(id+"F1.wireOp",EDGE,"E26"),sQuery(id+"F1.wireOp",EDGE,"E27"),sQuery(id+"F1.wireOp",EDGE,"E28"),sQuery(id+"F1.wireOp",EDGE,"E29"),sQuery(id+"F1.wireOp",EDGE,"E30"),sQuery(id+"F1.wireOp",EDGE,"E31"),sQuery(id+"F1.wireOp",EDGE,"E32"),sQuery(id+"F1.wireOp",EDGE,"E33"),sQuery(id+"F1.wireOp",EDGE,"E34"),sQuery(id+"F1.wireOp",EDGE,"E35"),sQuery(id+"F1.wireOp",EDGE,"E36"),sQuery(id+"F1.wireOp",EDGE,"E37"),sQuery(id+"F1.wireOp",EDGE,"E38"),sQuery(id+"F1.wireOp",EDGE,"E39"),sQuery(id+"F1.wireOp",EDGE,"E40"),sQuery(id+"F1.wireOp",EDGE,"E41"),sQuery(id+"F1.wireOp",EDGE,"E42"),sQuery(id+"F1.wireOp",EDGE,"E43"),sQuery(id+"F1.wireOp",EDGE,"E44"),sQuery(id+"F1.wireOp",EDGE,"E45"),sQuery(id+"F1.wireOp",EDGE,"E46"),sQuery(id+"F1.wireOp",EDGE,"E47"),sQuery(id+"F1.wireOp",EDGE,"E48"),sQuery(id+"F1.wireOp",EDGE,"E49"),sQuery(id+"F1.wireOp",EDGE,"E50"),sQuery(id+"F1.wireOp",EDGE,"E51"),sQuery(id+"F1.wireOp",EDGE,"E52"),sQuery(id+"F1.wireOp",EDGE,"E53"),sQuery(id+"F1.wireOp",EDGE,"E54"),sQuery(id+"F1.wireOp",EDGE,"E55"),sQuery(id+"F1.wireOp",EDGE,"E56"),sQuery(id+"F1.wireOp",EDGE,"E57"),sQuery(id+"F1.wireOp",EDGE,"E58"),sQuery(id+"F1.wireOp",EDGE,"E59"),sQuery(id+"F1.wireOp",EDGE,"E60"),sQuery(id+"F1.wireOp",EDGE,"E61"),sQuery(id+"F1.wireOp",EDGE,"E62"),sQuery(id+"F1.wireOp",EDGE,"E63"),sQuery(id+"F1.wireOp",EDGE,"E64"),sQuery(id+"F1.wireOp",EDGE,"E65"),sQuery(id+"F1.wireOp",EDGE,"E66"),sQuery(id+"F1.wireOp",EDGE,"E67"),sQuery(id+"F1.wireOp",EDGE,"E68"),sQuery(id+"F1.wireOp",EDGE,"E69"),sQuery(id+"F1.wireOp",EDGE,"E70"),sQuery(id+"F1.wireOp",EDGE,"E71"),sQuery(id+"F1.wireOp",EDGE,"E72"),sQuery(id+"F1.wireOp",EDGE,"E73"),sQuery(id+"F1.wireOp",EDGE,"E74"),sQuery(id+"F1.wireOp",EDGE,"E75"),sQuery(id+"F1.wireOp",EDGE,"E76"),sQuery(id+"F1.wireOp",EDGE,"E77"),sQuery(id+"F1.wireOp",EDGE,"E78"),sQuery(id+"F1.wireOp",EDGE,"E79"),sQuery(id+"F1.wireOp",EDGE,"E80"),sQuery(id+"F1.wireOp",EDGE,"E81"),sQuery(id+"F1.wireOp",EDGE,"E82"),sQuery(id+"F1.wireOp",EDGE,"E83"),sQuery(id+"F1.wireOp",EDGE,"E84"),sQuery(id+"F1.wireOp",EDGE,"E85"),sQuery(id+"F1.wireOp",EDGE,"E86"),sQuery(id+"F1.wireOp",EDGE,"E87"),sQuery(id+"F1.wireOp",EDGE,"E88"),sQuery(id+"F1.wireOp",EDGE,"E89"),sQuery(id+"F1.wireOp",EDGE,"E90"),sQuery(id+"F1.wireOp",EDGE,"E91"),sQuery(id+"F1.wireOp",EDGE,"E92"),sQuery(id+"F1.wireOp",EDGE,"E93"),sQuery(id+"F1.wireOp",EDGE,"E94"),sQuery(id+"F1.wireOp",EDGE,"E95"),sQuery(id+"F1.wireOp",EDGE,"E96"),sQuery(id+"F1.wireOp",EDGE,"E97"),sQuery(id+"F1.wireOp",EDGE,"E98"),sQuery(id+"F1.wireOp",EDGE,"E99"),sQuery(id+"F1.wireOp",EDGE,"E100"),sQuery(id+"F1.wireOp",EDGE,"E101"),sQuery(id+"F1.wireOp",EDGE,"E102"),sQuery(id+"F1.wireOp",EDGE,"E103"),sQuery(id+"F1.wireOp",EDGE,"E104"),sQuery(id+"F1.wireOp",EDGE,"E105"),sQuery(id+"F1.wireOp",EDGE,"E106"),sQuery(id+"F1.wireOp",EDGE,"E107"),sQuery(id+"F1.wireOp",EDGE,"E108"),sQuery(id+"F1.wireOp",EDGE,"E109"),sQuery(id+"F1.wireOp",EDGE,"E110"),sQuery(id+"F1.wireOp",EDGE,"E111"),sQuery(id+"F1.wireOp",EDGE,"E112"),sQuery(id+"F1.wireOp",EDGE,"E113"),sQuery(id+"F1.wireOp",EDGE,"E114"),sQuery(id+"F1.wireOp",EDGE,"E115"),sQuery(id+"F1.wireOp",EDGE,"E116"),sQuery(id+"F1.wireOp",EDGE,"E117"),sQuery(id+"F1.wireOp",EDGE,"E118"),sQuery(id+"F1.wireOp",EDGE,"E119"),sQuery(id+"F1.wireOp",EDGE,"E120"),sQuery(id+"F1.wireOp",EDGE,"E121"),sQuery(id+"F1.wireOp",EDGE,"E122"),sQuery(id+"F1.wireOp",EDGE,"E123"),sQuery(id+"F1.wireOp",EDGE,"E124"),sQuery(id+"F1.wireOp",EDGE,"E125"),sQuery(id+"F1.wireOp",EDGE,"E126"),sQuery(id+"F1.wireOp",EDGE,"E127"),sQuery(id+"F1.wireOp",EDGE,"E128"),sQuery(id+"F1.wireOp",EDGE,"E129"),sQuery(id+"F1.wireOp",EDGE,"E130"),sQuery(id+"F1.wireOp",EDGE,"E131"),sQuery(id+"F1.wireOp",EDGE,"E132"),sQuery(id+"F1.wireOp",EDGE,"E133"),sQuery(id+"F1.wireOp",EDGE,"E134"),sQuery(id+"F1.wireOp",EDGE,"E135"),sQuery(id+"F1.wireOp",EDGE,"E136"),sQuery(id+"F1.wireOp",EDGE,"E137"),sQuery(id+"F1.wireOp",EDGE,"E138"),sQuery(id+"F1.wireOp",EDGE,"E139"),sQuery(id+"F1.wireOp",EDGE,"E140"),sQuery(id+"F1.wireOp",EDGE,"E141"),sQuery(id+"F1.wireOp",EDGE,"E142"),sQuery(id+"F1.wireOp",EDGE,"E143"),sQuery(id+"F1.wireOp",EDGE,"E144"),sQuery(id+"F1.wireOp",EDGE,"E145"),sQuery(id+"F1.wireOp",EDGE,"E146"),sQuery(id+"F1.wireOp",EDGE,"E147"),sQuery(id+"F1.wireOp",EDGE,"E148"),sQuery(id+"F1.wireOp",EDGE,"E149"),sQuery(id+"F1.wireOp",EDGE,"E150"),sQuery(id+"F1.wireOp",EDGE,"E151"),sQuery(id+"F1.wireOp",EDGE,"E152"),sQuery(id+"F1.wireOp",EDGE,"E153"),sQuery(id+"F1.wireOp",EDGE,"E155"),sQuery(id+"F1.wireOp",EDGE,"E157"),sQuery(id+"F1.wireOp",EDGE,"E159"),sQuery(id+"F1.wireOp",EDGE,"E163"),sQuery(id+"F1.wireOp",EDGE,"E164"),sQuery(id+"F1.wireOp",EDGE,"E165"),sQuery(id+"F1.wireOp",EDGE,"E168"),sQuery(id+"F1.wireOp",EDGE,"E170"),sQuery(id+"F1.wireOp",EDGE,"E175"),sQuery(id+"F1.wireOp",EDGE,"E176"),sQuery(id+"F1.wireOp",EDGE,"E177"),sQuery(id+"F1.wireOp",EDGE,"E178")])],"isStart":false});
            var sketch = newSketch(context, id + "F24", { "sketchPlane" : qUnion([Q0])});
            skCircle(sketch, "E254", {"center": v(19.95, -9.9) * mm, "radius": 4 * mm});
            skSolve(sketch);
        }
        {
            var Q0;
            Q0=makeQuery(id+"F24.imprint","IMPRINT",FACE,{"disambiguationData":[TD([[makeQuery(id+"F24.imprint","IMPRINT",EDGE,{"derivedFrom":sQuery(id+"F24.wireOp",EDGE,"E254")}),-1.0]])]});
            var Q1;
            Q1=makeQuery(id+"F2.opExtrude","CAP_FACE",FACE,{"disambiguationData":[OSD([sQuery(id+"F1.wireOp",EDGE,"E0"),sQuery(id+"F1.wireOp",EDGE,"E1"),sQuery(id+"F1.wireOp",EDGE,"E2"),sQuery(id+"F1.wireOp",EDGE,"E3"),sQuery(id+"F1.wireOp",EDGE,"E4"),sQuery(id+"F1.wireOp",EDGE,"E5"),sQuery(id+"F1.wireOp",EDGE,"E6"),sQuery(id+"F1.wireOp",EDGE,"E7"),sQuery(id+"F1.wireOp",EDGE,"E8"),sQuery(id+"F1.wireOp",EDGE,"E9"),sQuery(id+"F1.wireOp",EDGE,"E10"),sQuery(id+"F1.wireOp",EDGE,"E11"),sQuery(id+"F1.wireOp",EDGE,"E12"),sQuery(id+"F1.wireOp",EDGE,"E13"),sQuery(id+"F1.wireOp",EDGE,"E14"),sQuery(id+"F1.wireOp",EDGE,"E15"),sQuery(id+"F1.wireOp",EDGE,"E16"),sQuery(id+"F1.wireOp",EDGE,"E17"),sQuery(id+"F1.wireOp",EDGE,"E18"),sQuery(id+"F1.wireOp",EDGE,"E19"),sQuery(id+"F1.wireOp",EDGE,"E20"),sQuery(id+"F1.wireOp",EDGE,"E21"),sQuery(id+"F1.wireOp",EDGE,"E22"),sQuery(id+"F1.wireOp",EDGE,"E23"),sQuery(id+"F1.wireOp",EDGE,"E24"),sQuery(id+"F1.wireOp",EDGE,"E25"),sQuery(id+"F1.wireOp",EDGE,"E26"),sQuery(id+"F1.wireOp",EDGE,"E27"),sQuery(id+"F1.wireOp",EDGE,"E28"),sQuery(id+"F1.wireOp",EDGE,"E29"),sQuery(id+"F1.wireOp",EDGE,"E30"),sQuery(id+"F1.wireOp",EDGE,"E31"),sQuery(id+"F1.wireOp",EDGE,"E32"),sQuery(id+"F1.wireOp",EDGE,"E33"),sQuery(id+"F1.wireOp",EDGE,"E34"),sQuery(id+"F1.wireOp",EDGE,"E35"),sQuery(id+"F1.wireOp",EDGE,"E36"),sQuery(id+"F1.wireOp",EDGE,"E37"),sQuery(id+"F1.wireOp",EDGE,"E38"),sQuery(id+"F1.wireOp",EDGE,"E39"),sQuery(id+"F1.wireOp",EDGE,"E40"),sQuery(id+"F1.wireOp",EDGE,"E41"),sQuery(id+"F1.wireOp",EDGE,"E42"),sQuery(id+"F1.wireOp",EDGE,"E43"),sQuery(id+"F1.wireOp",EDGE,"E44"),sQuery(id+"F1.wireOp",EDGE,"E45"),sQuery(id+"F1.wireOp",EDGE,"E46"),sQuery(id+"F1.wireOp",EDGE,"E47"),sQuery(id+"F1.wireOp",EDGE,"E48"),sQuery(id+"F1.wireOp",EDGE,"E49"),sQuery(id+"F1.wireOp",EDGE,"E50"),sQuery(id+"F1.wireOp",EDGE,"E51"),sQuery(id+"F1.wireOp",EDGE,"E52"),sQuery(id+"F1.wireOp",EDGE,"E53"),sQuery(id+"F1.wireOp",EDGE,"E54"),sQuery(id+"F1.wireOp",EDGE,"E55"),sQuery(id+"F1.wireOp",EDGE,"E56"),sQuery(id+"F1.wireOp",EDGE,"E57"),sQuery(id+"F1.wireOp",EDGE,"E58"),sQuery(id+"F1.wireOp",EDGE,"E59"),sQuery(id+"F1.wireOp",EDGE,"E60"),sQuery(id+"F1.wireOp",EDGE,"E61"),sQuery(id+"F1.wireOp",EDGE,"E62"),sQuery(id+"F1.wireOp",EDGE,"E63"),sQuery(id+"F1.wireOp",EDGE,"E64"),sQuery(id+"F1.wireOp",EDGE,"E65"),sQuery(id+"F1.wireOp",EDGE,"E66"),sQuery(id+"F1.wireOp",EDGE,"E67"),sQuery(id+"F1.wireOp",EDGE,"E68"),sQuery(id+"F1.wireOp",EDGE,"E69"),sQuery(id+"F1.wireOp",EDGE,"E70"),sQuery(id+"F1.wireOp",EDGE,"E71"),sQuery(id+"F1.wireOp",EDGE,"E72"),sQuery(id+"F1.wireOp",EDGE,"E73"),sQuery(id+"F1.wireOp",EDGE,"E74"),sQuery(id+"F1.wireOp",EDGE,"E75"),sQuery(id+"F1.wireOp",EDGE,"E76"),sQuery(id+"F1.wireOp",EDGE,"E77"),sQuery(id+"F1.wireOp",EDGE,"E78"),sQuery(id+"F1.wireOp",EDGE,"E79"),sQuery(id+"F1.wireOp",EDGE,"E80"),sQuery(id+"F1.wireOp",EDGE,"E81"),sQuery(id+"F1.wireOp",EDGE,"E82"),sQuery(id+"F1.wireOp",EDGE,"E83"),sQuery(id+"F1.wireOp",EDGE,"E84"),sQuery(id+"F1.wireOp",EDGE,"E85"),sQuery(id+"F1.wireOp",EDGE,"E86"),sQuery(id+"F1.wireOp",EDGE,"E87"),sQuery(id+"F1.wireOp",EDGE,"E88"),sQuery(id+"F1.wireOp",EDGE,"E89"),sQuery(id+"F1.wireOp",EDGE,"E90"),sQuery(id+"F1.wireOp",EDGE,"E91"),sQuery(id+"F1.wireOp",EDGE,"E92"),sQuery(id+"F1.wireOp",EDGE,"E93"),sQuery(id+"F1.wireOp",EDGE,"E94"),sQuery(id+"F1.wireOp",EDGE,"E95"),sQuery(id+"F1.wireOp",EDGE,"E96"),sQuery(id+"F1.wireOp",EDGE,"E97"),sQuery(id+"F1.wireOp",EDGE,"E98"),sQuery(id+"F1.wireOp",EDGE,"E99"),sQuery(id+"F1.wireOp",EDGE,"E100"),sQuery(id+"F1.wireOp",EDGE,"E101"),sQuery(id+"F1.wireOp",EDGE,"E102"),sQuery(id+"F1.wireOp",EDGE,"E103"),sQuery(id+"F1.wireOp",EDGE,"E104"),sQuery(id+"F1.wireOp",EDGE,"E105"),sQuery(id+"F1.wireOp",EDGE,"E106"),sQuery(id+"F1.wireOp",EDGE,"E107"),sQuery(id+"F1.wireOp",EDGE,"E108"),sQuery(id+"F1.wireOp",EDGE,"E109"),sQuery(id+"F1.wireOp",EDGE,"E110"),sQuery(id+"F1.wireOp",EDGE,"E111"),sQuery(id+"F1.wireOp",EDGE,"E112"),sQuery(id+"F1.wireOp",EDGE,"E113"),sQuery(id+"F1.wireOp",EDGE,"E114"),sQuery(id+"F1.wireOp",EDGE,"E115"),sQuery(id+"F1.wireOp",EDGE,"E116"),sQuery(id+"F1.wireOp",EDGE,"E117"),sQuery(id+"F1.wireOp",EDGE,"E118"),sQuery(id+"F1.wireOp",EDGE,"E119"),sQuery(id+"F1.wireOp",EDGE,"E120"),sQuery(id+"F1.wireOp",EDGE,"E121"),sQuery(id+"F1.wireOp",EDGE,"E122"),sQuery(id+"F1.wireOp",EDGE,"E123"),sQuery(id+"F1.wireOp",EDGE,"E124"),sQuery(id+"F1.wireOp",EDGE,"E125"),sQuery(id+"F1.wireOp",EDGE,"E126"),sQuery(id+"F1.wireOp",EDGE,"E127"),sQuery(id+"F1.wireOp",EDGE,"E128"),sQuery(id+"F1.wireOp",EDGE,"E129"),sQuery(id+"F1.wireOp",EDGE,"E130"),sQuery(id+"F1.wireOp",EDGE,"E131"),sQuery(id+"F1.wireOp",EDGE,"E132"),sQuery(id+"F1.wireOp",EDGE,"E133"),sQuery(id+"F1.wireOp",EDGE,"E134"),sQuery(id+"F1.wireOp",EDGE,"E135"),sQuery(id+"F1.wireOp",EDGE,"E136"),sQuery(id+"F1.wireOp",EDGE,"E137"),sQuery(id+"F1.wireOp",EDGE,"E138"),sQuery(id+"F1.wireOp",EDGE,"E139"),sQuery(id+"F1.wireOp",EDGE,"E140"),sQuery(id+"F1.wireOp",EDGE,"E141"),sQuery(id+"F1.wireOp",EDGE,"E142"),sQuery(id+"F1.wireOp",EDGE,"E143"),sQuery(id+"F1.wireOp",EDGE,"E144"),sQuery(id+"F1.wireOp",EDGE,"E145"),sQuery(id+"F1.wireOp",EDGE,"E146"),sQuery(id+"F1.wireOp",EDGE,"E147"),sQuery(id+"F1.wireOp",EDGE,"E148"),sQuery(id+"F1.wireOp",EDGE,"E149"),sQuery(id+"F1.wireOp",EDGE,"E150"),sQuery(id+"F1.wireOp",EDGE,"E151"),sQuery(id+"F1.wireOp",EDGE,"E152"),sQuery(id+"F1.wireOp",EDGE,"E153"),sQuery(id+"F1.wireOp",EDGE,"E155"),sQuery(id+"F1.wireOp",EDGE,"E157"),sQuery(id+"F1.wireOp",EDGE,"E159"),sQuery(id+"F1.wireOp",EDGE,"E163"),sQuery(id+"F1.wireOp",EDGE,"E164"),sQuery(id+"F1.wireOp",EDGE,"E165"),sQuery(id+"F1.wireOp",EDGE,"E168"),sQuery(id+"F1.wireOp",EDGE,"E170"),sQuery(id+"F1.wireOp",EDGE,"E175"),sQuery(id+"F1.wireOp",EDGE,"E176"),sQuery(id+"F1.wireOp",EDGE,"E177"),sQuery(id+"F1.wireOp",EDGE,"E178")])],"isStart":true});
            extrude(context, id + "F25", {"entities" : qUnion([Q0]), "endBound" : BoundingType.UP_TO_SURFACE, "oppositeDirection" : true, "depth" : 25 * mm, "endBoundEntityFace" : qUnion([Q1]), "offsetDistance" : 25 * mm});
        }
        {
            var Q0;
            Q0=makeQuery(id+"F8.opExtrude","CAP_FACE",FACE,{"disambiguationData":[OSD([sQuery(id+"F7.wireOp",EDGE,"E229.0.0"),sQuery(id+"F7.wireOp",EDGE,"E229.0.1"),sQuery(id+"F7.wireOp",EDGE,"E229.0.2"),sQuery(id+"F7.wireOp",EDGE,"E229.0.3"),sQuery(id+"F7.wireOp",EDGE,"E229.0.4"),sQuery(id+"F7.wireOp",EDGE,"E229.0.5"),sQuery(id+"F7.wireOp",EDGE,"E229.0.6"),sQuery(id+"F7.wireOp",EDGE,"E229.0.7"),sQuery(id+"F7.wireOp",EDGE,"E229.0.8"),sQuery(id+"F7.wireOp",EDGE,"E229.0.9"),sQuery(id+"F7.wireOp",EDGE,"E229.0.10"),sQuery(id+"F7.wireOp",EDGE,"E229.0.11"),sQuery(id+"F7.wireOp",EDGE,"E229.0.12"),sQuery(id+"F7.wireOp",EDGE,"E229.0.13"),sQuery(id+"F7.wireOp",EDGE,"E229.0.14"),sQuery(id+"F7.wireOp",EDGE,"E229.0.15"),sQuery(id+"F7.wireOp",EDGE,"E229.0.16"),sQuery(id+"F7.wireOp",EDGE,"E229.0.17"),sQuery(id+"F7.wireOp",EDGE,"E229.0.18"),sQuery(id+"F7.wireOp",EDGE,"E229.0.19"),sQuery(id+"F7.wireOp",EDGE,"E229.0.20"),sQuery(id+"F7.wireOp",EDGE,"E229.0.21"),sQuery(id+"F7.wireOp",EDGE,"E229.0.22"),sQuery(id+"F7.wireOp",EDGE,"E229.0.23"),sQuery(id+"F7.wireOp",EDGE,"E229.0.24"),sQuery(id+"F7.wireOp",EDGE,"E229.0.25"),sQuery(id+"F7.wireOp",EDGE,"E229.0.26"),sQuery(id+"F7.wireOp",EDGE,"E229.0.27"),sQuery(id+"F7.wireOp",EDGE,"E229.0.28"),sQuery(id+"F7.wireOp",EDGE,"E229.0.29"),sQuery(id+"F7.wireOp",EDGE,"E229.0.30"),sQuery(id+"F7.wireOp",EDGE,"E229.0.31"),sQuery(id+"F7.wireOp",EDGE,"E229.0.32"),sQuery(id+"F7.wireOp",EDGE,"E229.0.33"),sQuery(id+"F7.wireOp",EDGE,"E229.0.34"),sQuery(id+"F7.wireOp",EDGE,"E229.0.35"),sQuery(id+"F7.wireOp",EDGE,"E229.0.36"),sQuery(id+"F7.wireOp",EDGE,"E229.0.37"),sQuery(id+"F7.wireOp",EDGE,"E229.0.38"),sQuery(id+"F7.wireOp",EDGE,"E229.0.39"),sQuery(id+"F7.wireOp",EDGE,"E229.0.40"),sQuery(id+"F7.wireOp",EDGE,"E229.0.41"),sQuery(id+"F7.wireOp",EDGE,"E229.0.42"),sQuery(id+"F7.wireOp",EDGE,"E229.0.43"),sQuery(id+"F7.wireOp",EDGE,"E229.0.44"),sQuery(id+"F7.wireOp",EDGE,"E229.0.45"),sQuery(id+"F7.wireOp",EDGE,"E229.0.46"),sQuery(id+"F7.wireOp",EDGE,"E229.0.47"),sQuery(id+"F7.wireOp",EDGE,"E229.0.48"),sQuery(id+"F7.wireOp",EDGE,"E229.0.49"),sQuery(id+"F7.wireOp",EDGE,"E229.0.50"),sQuery(id+"F7.wireOp",EDGE,"E229.0.51"),sQuery(id+"F7.wireOp",EDGE,"E229.0.52"),sQuery(id+"F7.wireOp",EDGE,"E229.0.53"),sQuery(id+"F7.wireOp",EDGE,"E229.0.54"),sQuery(id+"F7.wireOp",EDGE,"E229.0.55"),sQuery(id+"F7.wireOp",EDGE,"E229.0.56"),sQuery(id+"F7.wireOp",EDGE,"E229.0.57"),sQuery(id+"F7.wireOp",EDGE,"E229.0.58"),sQuery(id+"F7.wireOp",EDGE,"E229.0.59"),sQuery(id+"F7.wireOp",EDGE,"E229.0.60"),sQuery(id+"F7.wireOp",EDGE,"E229.0.61"),sQuery(id+"F7.wireOp",EDGE,"E229.0.62"),sQuery(id+"F7.wireOp",EDGE,"E229.0.63"),sQuery(id+"F7.wireOp",EDGE,"E229.0.64"),sQuery(id+"F7.wireOp",EDGE,"E229.0.65"),sQuery(id+"F7.wireOp",EDGE,"E229.0.66"),sQuery(id+"F7.wireOp",EDGE,"E229.0.67"),sQuery(id+"F7.wireOp",EDGE,"E229.0.68"),sQuery(id+"F7.wireOp",EDGE,"E229.0.69"),sQuery(id+"F7.wireOp",EDGE,"E229.0.70"),sQuery(id+"F7.wireOp",EDGE,"E229.0.71"),sQuery(id+"F7.wireOp",EDGE,"E229.0.72"),sQuery(id+"F7.wireOp",EDGE,"E229.0.73"),sQuery(id+"F7.wireOp",EDGE,"E229.0.74"),sQuery(id+"F7.wireOp",EDGE,"E229.0.75"),sQuery(id+"F7.wireOp",EDGE,"E229.0.76"),sQuery(id+"F7.wireOp",EDGE,"E229.0.77"),sQuery(id+"F7.wireOp",EDGE,"E229.0.78"),sQuery(id+"F7.wireOp",EDGE,"E229.0.79"),sQuery(id+"F7.wireOp",EDGE,"E229.0.80"),sQuery(id+"F7.wireOp",EDGE,"E229.0.81"),sQuery(id+"F7.wireOp",EDGE,"E229.0.82"),sQuery(id+"F7.wireOp",EDGE,"E229.0.83"),sQuery(id+"F7.wireOp",EDGE,"E229.0.84"),sQuery(id+"F7.wireOp",EDGE,"E229.0.85"),sQuery(id+"F7.wireOp",EDGE,"E229.0.86"),sQuery(id+"F7.wireOp",EDGE,"E229.0.87"),sQuery(id+"F7.wireOp",EDGE,"E229.0.88"),sQuery(id+"F7.wireOp",EDGE,"E229.0.89"),sQuery(id+"F7.wireOp",EDGE,"E229.0.90"),sQuery(id+"F7.wireOp",EDGE,"E229.0.91"),sQuery(id+"F7.wireOp",EDGE,"E229.0.92"),sQuery(id+"F7.wireOp",EDGE,"E229.0.93"),sQuery(id+"F7.wireOp",EDGE,"E229.0.94"),sQuery(id+"F7.wireOp",EDGE,"E229.0.95"),sQuery(id+"F7.wireOp",EDGE,"E229.0.96"),sQuery(id+"F7.wireOp",EDGE,"E229.0.97"),sQuery(id+"F7.wireOp",EDGE,"E229.0.98"),sQuery(id+"F7.wireOp",EDGE,"E229.0.99"),sQuery(id+"F7.wireOp",EDGE,"E229.0.100"),sQuery(id+"F7.wireOp",EDGE,"E229.0.101"),sQuery(id+"F7.wireOp",EDGE,"E229.0.102"),sQuery(id+"F7.wireOp",EDGE,"E229.0.103"),sQuery(id+"F7.wireOp",EDGE,"E229.0.104"),sQuery(id+"F7.wireOp",EDGE,"E229.0.105"),sQuery(id+"F7.wireOp",EDGE,"E229.0.106"),sQuery(id+"F7.wireOp",EDGE,"E229.0.107"),sQuery(id+"F7.wireOp",EDGE,"E229.0.108"),sQuery(id+"F7.wireOp",EDGE,"E229.0.109"),sQuery(id+"F7.wireOp",EDGE,"E229.0.110"),sQuery(id+"F7.wireOp",EDGE,"E229.0.111"),sQuery(id+"F7.wireOp",EDGE,"E229.0.112"),sQuery(id+"F7.wireOp",EDGE,"E229.0.113"),sQuery(id+"F7.wireOp",EDGE,"E229.0.114"),sQuery(id+"F7.wireOp",EDGE,"E229.0.115"),sQuery(id+"F7.wireOp",EDGE,"E229.0.116"),sQuery(id+"F7.wireOp",EDGE,"E229.0.117"),sQuery(id+"F7.wireOp",EDGE,"E229.0.118"),sQuery(id+"F7.wireOp",EDGE,"E229.0.119"),sQuery(id+"F7.wireOp",EDGE,"E229.0.120"),sQuery(id+"F7.wireOp",EDGE,"E229.0.121"),sQuery(id+"F7.wireOp",EDGE,"E229.0.122"),sQuery(id+"F7.wireOp",EDGE,"E229.0.123"),sQuery(id+"F7.wireOp",EDGE,"E229.0.124"),sQuery(id+"F7.wireOp",EDGE,"E230.0"),sQuery(id+"F7.wireOp",EDGE,"E230.2"),sQuery(id+"F7.wireOp",EDGE,"E230.3"),sQuery(id+"F7.wireOp",EDGE,"E231"),sQuery(id+"F7.wireOp",EDGE,"E232")])],"isStart":false});
            var sketch = newSketch(context, id + "F26", { "sketchPlane" : qUnion([Q0])});
            skCircle(sketch, "E255", {"center": v(-94.95, -9.9) * mm, "radius": 4 * mm});
            skCircle(sketch, "E256", {"center": v(-19.95, -9.9) * mm, "radius": 4 * mm});
            skSolve(sketch);
        }
        {
            var Q0;
            Q0=makeQuery(id+"F26.imprint","IMPRINT",FACE,{"disambiguationData":[TD([[makeQuery(id+"F26.imprint","IMPRINT",EDGE,{"derivedFrom":sQuery(id+"F26.wireOp",EDGE,"E255")}),-1.0]])]});
            var Q1;
            Q1=makeQuery(id+"F26.imprint","IMPRINT",FACE,{"disambiguationData":[TD([[makeQuery(id+"F26.imprint","IMPRINT",EDGE,{"derivedFrom":sQuery(id+"F26.wireOp",EDGE,"E256")}),-1.0]])]});
            var Q2;
            Q2=makeQuery(id+"F8.opExtrude","CAP_FACE",FACE,{"disambiguationData":[OSD([sQuery(id+"F7.wireOp",EDGE,"E229.0.0"),sQuery(id+"F7.wireOp",EDGE,"E229.0.1"),sQuery(id+"F7.wireOp",EDGE,"E229.0.2"),sQuery(id+"F7.wireOp",EDGE,"E229.0.3"),sQuery(id+"F7.wireOp",EDGE,"E229.0.4"),sQuery(id+"F7.wireOp",EDGE,"E229.0.5"),sQuery(id+"F7.wireOp",EDGE,"E229.0.6"),sQuery(id+"F7.wireOp",EDGE,"E229.0.7"),sQuery(id+"F7.wireOp",EDGE,"E229.0.8"),sQuery(id+"F7.wireOp",EDGE,"E229.0.9"),sQuery(id+"F7.wireOp",EDGE,"E229.0.10"),sQuery(id+"F7.wireOp",EDGE,"E229.0.11"),sQuery(id+"F7.wireOp",EDGE,"E229.0.12"),sQuery(id+"F7.wireOp",EDGE,"E229.0.13"),sQuery(id+"F7.wireOp",EDGE,"E229.0.14"),sQuery(id+"F7.wireOp",EDGE,"E229.0.15"),sQuery(id+"F7.wireOp",EDGE,"E229.0.16"),sQuery(id+"F7.wireOp",EDGE,"E229.0.17"),sQuery(id+"F7.wireOp",EDGE,"E229.0.18"),sQuery(id+"F7.wireOp",EDGE,"E229.0.19"),sQuery(id+"F7.wireOp",EDGE,"E229.0.20"),sQuery(id+"F7.wireOp",EDGE,"E229.0.21"),sQuery(id+"F7.wireOp",EDGE,"E229.0.22"),sQuery(id+"F7.wireOp",EDGE,"E229.0.23"),sQuery(id+"F7.wireOp",EDGE,"E229.0.24"),sQuery(id+"F7.wireOp",EDGE,"E229.0.25"),sQuery(id+"F7.wireOp",EDGE,"E229.0.26"),sQuery(id+"F7.wireOp",EDGE,"E229.0.27"),sQuery(id+"F7.wireOp",EDGE,"E229.0.28"),sQuery(id+"F7.wireOp",EDGE,"E229.0.29"),sQuery(id+"F7.wireOp",EDGE,"E229.0.30"),sQuery(id+"F7.wireOp",EDGE,"E229.0.31"),sQuery(id+"F7.wireOp",EDGE,"E229.0.32"),sQuery(id+"F7.wireOp",EDGE,"E229.0.33"),sQuery(id+"F7.wireOp",EDGE,"E229.0.34"),sQuery(id+"F7.wireOp",EDGE,"E229.0.35"),sQuery(id+"F7.wireOp",EDGE,"E229.0.36"),sQuery(id+"F7.wireOp",EDGE,"E229.0.37"),sQuery(id+"F7.wireOp",EDGE,"E229.0.38"),sQuery(id+"F7.wireOp",EDGE,"E229.0.39"),sQuery(id+"F7.wireOp",EDGE,"E229.0.40"),sQuery(id+"F7.wireOp",EDGE,"E229.0.41"),sQuery(id+"F7.wireOp",EDGE,"E229.0.42"),sQuery(id+"F7.wireOp",EDGE,"E229.0.43"),sQuery(id+"F7.wireOp",EDGE,"E229.0.44"),sQuery(id+"F7.wireOp",EDGE,"E229.0.45"),sQuery(id+"F7.wireOp",EDGE,"E229.0.46"),sQuery(id+"F7.wireOp",EDGE,"E229.0.47"),sQuery(id+"F7.wireOp",EDGE,"E229.0.48"),sQuery(id+"F7.wireOp",EDGE,"E229.0.49"),sQuery(id+"F7.wireOp",EDGE,"E229.0.50"),sQuery(id+"F7.wireOp",EDGE,"E229.0.51"),sQuery(id+"F7.wireOp",EDGE,"E229.0.52"),sQuery(id+"F7.wireOp",EDGE,"E229.0.53"),sQuery(id+"F7.wireOp",EDGE,"E229.0.54"),sQuery(id+"F7.wireOp",EDGE,"E229.0.55"),sQuery(id+"F7.wireOp",EDGE,"E229.0.56"),sQuery(id+"F7.wireOp",EDGE,"E229.0.57"),sQuery(id+"F7.wireOp",EDGE,"E229.0.58"),sQuery(id+"F7.wireOp",EDGE,"E229.0.59"),sQuery(id+"F7.wireOp",EDGE,"E229.0.60"),sQuery(id+"F7.wireOp",EDGE,"E229.0.61"),sQuery(id+"F7.wireOp",EDGE,"E229.0.62"),sQuery(id+"F7.wireOp",EDGE,"E229.0.63"),sQuery(id+"F7.wireOp",EDGE,"E229.0.64"),sQuery(id+"F7.wireOp",EDGE,"E229.0.65"),sQuery(id+"F7.wireOp",EDGE,"E229.0.66"),sQuery(id+"F7.wireOp",EDGE,"E229.0.67"),sQuery(id+"F7.wireOp",EDGE,"E229.0.68"),sQuery(id+"F7.wireOp",EDGE,"E229.0.69"),sQuery(id+"F7.wireOp",EDGE,"E229.0.70"),sQuery(id+"F7.wireOp",EDGE,"E229.0.71"),sQuery(id+"F7.wireOp",EDGE,"E229.0.72"),sQuery(id+"F7.wireOp",EDGE,"E229.0.73"),sQuery(id+"F7.wireOp",EDGE,"E229.0.74"),sQuery(id+"F7.wireOp",EDGE,"E229.0.75"),sQuery(id+"F7.wireOp",EDGE,"E229.0.76"),sQuery(id+"F7.wireOp",EDGE,"E229.0.77"),sQuery(id+"F7.wireOp",EDGE,"E229.0.78"),sQuery(id+"F7.wireOp",EDGE,"E229.0.79"),sQuery(id+"F7.wireOp",EDGE,"E229.0.80"),sQuery(id+"F7.wireOp",EDGE,"E229.0.81"),sQuery(id+"F7.wireOp",EDGE,"E229.0.82"),sQuery(id+"F7.wireOp",EDGE,"E229.0.83"),sQuery(id+"F7.wireOp",EDGE,"E229.0.84"),sQuery(id+"F7.wireOp",EDGE,"E229.0.85"),sQuery(id+"F7.wireOp",EDGE,"E229.0.86"),sQuery(id+"F7.wireOp",EDGE,"E229.0.87"),sQuery(id+"F7.wireOp",EDGE,"E229.0.88"),sQuery(id+"F7.wireOp",EDGE,"E229.0.89"),sQuery(id+"F7.wireOp",EDGE,"E229.0.90"),sQuery(id+"F7.wireOp",EDGE,"E229.0.91"),sQuery(id+"F7.wireOp",EDGE,"E229.0.92"),sQuery(id+"F7.wireOp",EDGE,"E229.0.93"),sQuery(id+"F7.wireOp",EDGE,"E229.0.94"),sQuery(id+"F7.wireOp",EDGE,"E229.0.95"),sQuery(id+"F7.wireOp",EDGE,"E229.0.96"),sQuery(id+"F7.wireOp",EDGE,"E229.0.97"),sQuery(id+"F7.wireOp",EDGE,"E229.0.98"),sQuery(id+"F7.wireOp",EDGE,"E229.0.99"),sQuery(id+"F7.wireOp",EDGE,"E229.0.100"),sQuery(id+"F7.wireOp",EDGE,"E229.0.101"),sQuery(id+"F7.wireOp",EDGE,"E229.0.102"),sQuery(id+"F7.wireOp",EDGE,"E229.0.103"),sQuery(id+"F7.wireOp",EDGE,"E229.0.104"),sQuery(id+"F7.wireOp",EDGE,"E229.0.105"),sQuery(id+"F7.wireOp",EDGE,"E229.0.106"),sQuery(id+"F7.wireOp",EDGE,"E229.0.107"),sQuery(id+"F7.wireOp",EDGE,"E229.0.108"),sQuery(id+"F7.wireOp",EDGE,"E229.0.109"),sQuery(id+"F7.wireOp",EDGE,"E229.0.110"),sQuery(id+"F7.wireOp",EDGE,"E229.0.111"),sQuery(id+"F7.wireOp",EDGE,"E229.0.112"),sQuery(id+"F7.wireOp",EDGE,"E229.0.113"),sQuery(id+"F7.wireOp",EDGE,"E229.0.114"),sQuery(id+"F7.wireOp",EDGE,"E229.0.115"),sQuery(id+"F7.wireOp",EDGE,"E229.0.116"),sQuery(id+"F7.wireOp",EDGE,"E229.0.117"),sQuery(id+"F7.wireOp",EDGE,"E229.0.118"),sQuery(id+"F7.wireOp",EDGE,"E229.0.119"),sQuery(id+"F7.wireOp",EDGE,"E229.0.120"),sQuery(id+"F7.wireOp",EDGE,"E229.0.121"),sQuery(id+"F7.wireOp",EDGE,"E229.0.122"),sQuery(id+"F7.wireOp",EDGE,"E229.0.123"),sQuery(id+"F7.wireOp",EDGE,"E229.0.124"),sQuery(id+"F7.wireOp",EDGE,"E230.0"),sQuery(id+"F7.wireOp",EDGE,"E230.2"),sQuery(id+"F7.wireOp",EDGE,"E230.3"),sQuery(id+"F7.wireOp",EDGE,"E231"),sQuery(id+"F7.wireOp",EDGE,"E232")])],"isStart":true});
            extrude(context, id + "F27", {"entities" : qUnion([Q0, Q1]), "endBound" : BoundingType.UP_TO_SURFACE, "oppositeDirection" : true, "depth" : 25 * mm, "endBoundEntityFace" : qUnion([Q2]), "offsetDistance" : 25 * mm});
        }
        {
            var Q0;
            Q0=makeQuery(id+"F23.opExtrude","CAP_FACE",FACE,{"disambiguationData":[OSD([sQuery(id+"F22.wireOp",EDGE,"E252")])],"isStart":false});
            var sketch = newSketch(context, id + "F28", { "sketchPlane" : qUnion([Q0])});
            skCircle(sketch, "E257", {"center": v(-94.95, -9.9) * mm, "radius": 4 * mm});
            skSolve(sketch);
        }
        {
            var Q0;
            Q0=makeQuery(id+"F25.opExtrude","CAP_FACE",FACE,{"disambiguationData":[OSD([sQuery(id+"F1.wireOp",EDGE,"E168"),sQuery(id+"F24.wireOp",EDGE,"E254")])],"isStart":true});
            var sketch = newSketch(context, id + "F29", { "sketchPlane" : qUnion([Q0])});
            skCircle(sketch, "E258", {"center": v(19.95, -9.9) * mm, "radius": 4 * mm});
            skSolve(sketch);
        }
        {
            var Q0;
            Q0=makeQuery(id+"F29.imprint","IMPRINT",FACE,{"disambiguationData":[TD([[makeQuery(id+"F29.imprint","IMPRINT",EDGE,{"derivedFrom":sQuery(id+"F29.wireOp",EDGE,"E258")}),1.0]])]});
            var Q1;
            Q1=makeQuery(id+"F28.imprint","IMPRINT",FACE,{"disambiguationData":[TD([[makeQuery(id+"F28.imprint","IMPRINT",EDGE,{"derivedFrom":makeQuery(id+"F23.opExtrude","CAP_EDGE",EDGE,{"disambiguationData":[OSD([sQuery(id+"F22.wireOp",EDGE,"E252")])],"isStart":false})}),1.0]])]});
            var Q2;
            Q2=makeQuery(id+"F28.imprint","IMPRINT",FACE,{"disambiguationData":[TD([[makeQuery(id+"F28.imprint","IMPRINT",EDGE,{"derivedFrom":sQuery(id+"F28.wireOp",EDGE,"E257")}),1.0]])]});
            var Q3;
            Q3=makeQuery(id+"F8.opExtrude","CAP_FACE",FACE,{"disambiguationData":[OSD([sQuery(id+"F7.wireOp",EDGE,"E229.0.0"),sQuery(id+"F7.wireOp",EDGE,"E229.0.1"),sQuery(id+"F7.wireOp",EDGE,"E229.0.2"),sQuery(id+"F7.wireOp",EDGE,"E229.0.3"),sQuery(id+"F7.wireOp",EDGE,"E229.0.4"),sQuery(id+"F7.wireOp",EDGE,"E229.0.5"),sQuery(id+"F7.wireOp",EDGE,"E229.0.6"),sQuery(id+"F7.wireOp",EDGE,"E229.0.7"),sQuery(id+"F7.wireOp",EDGE,"E229.0.8"),sQuery(id+"F7.wireOp",EDGE,"E229.0.9"),sQuery(id+"F7.wireOp",EDGE,"E229.0.10"),sQuery(id+"F7.wireOp",EDGE,"E229.0.11"),sQuery(id+"F7.wireOp",EDGE,"E229.0.12"),sQuery(id+"F7.wireOp",EDGE,"E229.0.13"),sQuery(id+"F7.wireOp",EDGE,"E229.0.14"),sQuery(id+"F7.wireOp",EDGE,"E229.0.15"),sQuery(id+"F7.wireOp",EDGE,"E229.0.16"),sQuery(id+"F7.wireOp",EDGE,"E229.0.17"),sQuery(id+"F7.wireOp",EDGE,"E229.0.18"),sQuery(id+"F7.wireOp",EDGE,"E229.0.19"),sQuery(id+"F7.wireOp",EDGE,"E229.0.20"),sQuery(id+"F7.wireOp",EDGE,"E229.0.21"),sQuery(id+"F7.wireOp",EDGE,"E229.0.22"),sQuery(id+"F7.wireOp",EDGE,"E229.0.23"),sQuery(id+"F7.wireOp",EDGE,"E229.0.24"),sQuery(id+"F7.wireOp",EDGE,"E229.0.25"),sQuery(id+"F7.wireOp",EDGE,"E229.0.26"),sQuery(id+"F7.wireOp",EDGE,"E229.0.27"),sQuery(id+"F7.wireOp",EDGE,"E229.0.28"),sQuery(id+"F7.wireOp",EDGE,"E229.0.29"),sQuery(id+"F7.wireOp",EDGE,"E229.0.30"),sQuery(id+"F7.wireOp",EDGE,"E229.0.31"),sQuery(id+"F7.wireOp",EDGE,"E229.0.32"),sQuery(id+"F7.wireOp",EDGE,"E229.0.33"),sQuery(id+"F7.wireOp",EDGE,"E229.0.34"),sQuery(id+"F7.wireOp",EDGE,"E229.0.35"),sQuery(id+"F7.wireOp",EDGE,"E229.0.36"),sQuery(id+"F7.wireOp",EDGE,"E229.0.37"),sQuery(id+"F7.wireOp",EDGE,"E229.0.38"),sQuery(id+"F7.wireOp",EDGE,"E229.0.39"),sQuery(id+"F7.wireOp",EDGE,"E229.0.40"),sQuery(id+"F7.wireOp",EDGE,"E229.0.41"),sQuery(id+"F7.wireOp",EDGE,"E229.0.42"),sQuery(id+"F7.wireOp",EDGE,"E229.0.43"),sQuery(id+"F7.wireOp",EDGE,"E229.0.44"),sQuery(id+"F7.wireOp",EDGE,"E229.0.45"),sQuery(id+"F7.wireOp",EDGE,"E229.0.46"),sQuery(id+"F7.wireOp",EDGE,"E229.0.47"),sQuery(id+"F7.wireOp",EDGE,"E229.0.48"),sQuery(id+"F7.wireOp",EDGE,"E229.0.49"),sQuery(id+"F7.wireOp",EDGE,"E229.0.50"),sQuery(id+"F7.wireOp",EDGE,"E229.0.51"),sQuery(id+"F7.wireOp",EDGE,"E229.0.52"),sQuery(id+"F7.wireOp",EDGE,"E229.0.53"),sQuery(id+"F7.wireOp",EDGE,"E229.0.54"),sQuery(id+"F7.wireOp",EDGE,"E229.0.55"),sQuery(id+"F7.wireOp",EDGE,"E229.0.56"),sQuery(id+"F7.wireOp",EDGE,"E229.0.57"),sQuery(id+"F7.wireOp",EDGE,"E229.0.58"),sQuery(id+"F7.wireOp",EDGE,"E229.0.59"),sQuery(id+"F7.wireOp",EDGE,"E229.0.60"),sQuery(id+"F7.wireOp",EDGE,"E229.0.61"),sQuery(id+"F7.wireOp",EDGE,"E229.0.62"),sQuery(id+"F7.wireOp",EDGE,"E229.0.63"),sQuery(id+"F7.wireOp",EDGE,"E229.0.64"),sQuery(id+"F7.wireOp",EDGE,"E229.0.65"),sQuery(id+"F7.wireOp",EDGE,"E229.0.66"),sQuery(id+"F7.wireOp",EDGE,"E229.0.67"),sQuery(id+"F7.wireOp",EDGE,"E229.0.68"),sQuery(id+"F7.wireOp",EDGE,"E229.0.69"),sQuery(id+"F7.wireOp",EDGE,"E229.0.70"),sQuery(id+"F7.wireOp",EDGE,"E229.0.71"),sQuery(id+"F7.wireOp",EDGE,"E229.0.72"),sQuery(id+"F7.wireOp",EDGE,"E229.0.73"),sQuery(id+"F7.wireOp",EDGE,"E229.0.74"),sQuery(id+"F7.wireOp",EDGE,"E229.0.75"),sQuery(id+"F7.wireOp",EDGE,"E229.0.76"),sQuery(id+"F7.wireOp",EDGE,"E229.0.77"),sQuery(id+"F7.wireOp",EDGE,"E229.0.78"),sQuery(id+"F7.wireOp",EDGE,"E229.0.79"),sQuery(id+"F7.wireOp",EDGE,"E229.0.80"),sQuery(id+"F7.wireOp",EDGE,"E229.0.81"),sQuery(id+"F7.wireOp",EDGE,"E229.0.82"),sQuery(id+"F7.wireOp",EDGE,"E229.0.83"),sQuery(id+"F7.wireOp",EDGE,"E229.0.84"),sQuery(id+"F7.wireOp",EDGE,"E229.0.85"),sQuery(id+"F7.wireOp",EDGE,"E229.0.86"),sQuery(id+"F7.wireOp",EDGE,"E229.0.87"),sQuery(id+"F7.wireOp",EDGE,"E229.0.88"),sQuery(id+"F7.wireOp",EDGE,"E229.0.89"),sQuery(id+"F7.wireOp",EDGE,"E229.0.90"),sQuery(id+"F7.wireOp",EDGE,"E229.0.91"),sQuery(id+"F7.wireOp",EDGE,"E229.0.92"),sQuery(id+"F7.wireOp",EDGE,"E229.0.93"),sQuery(id+"F7.wireOp",EDGE,"E229.0.94"),sQuery(id+"F7.wireOp",EDGE,"E229.0.95"),sQuery(id+"F7.wireOp",EDGE,"E229.0.96"),sQuery(id+"F7.wireOp",EDGE,"E229.0.97"),sQuery(id+"F7.wireOp",EDGE,"E229.0.98"),sQuery(id+"F7.wireOp",EDGE,"E229.0.99"),sQuery(id+"F7.wireOp",EDGE,"E229.0.100"),sQuery(id+"F7.wireOp",EDGE,"E229.0.101"),sQuery(id+"F7.wireOp",EDGE,"E229.0.102"),sQuery(id+"F7.wireOp",EDGE,"E229.0.103"),sQuery(id+"F7.wireOp",EDGE,"E229.0.104"),sQuery(id+"F7.wireOp",EDGE,"E229.0.105"),sQuery(id+"F7.wireOp",EDGE,"E229.0.106"),sQuery(id+"F7.wireOp",EDGE,"E229.0.107"),sQuery(id+"F7.wireOp",EDGE,"E229.0.108"),sQuery(id+"F7.wireOp",EDGE,"E229.0.109"),sQuery(id+"F7.wireOp",EDGE,"E229.0.110"),sQuery(id+"F7.wireOp",EDGE,"E229.0.111"),sQuery(id+"F7.wireOp",EDGE,"E229.0.112"),sQuery(id+"F7.wireOp",EDGE,"E229.0.113"),sQuery(id+"F7.wireOp",EDGE,"E229.0.114"),sQuery(id+"F7.wireOp",EDGE,"E229.0.115"),sQuery(id+"F7.wireOp",EDGE,"E229.0.116"),sQuery(id+"F7.wireOp",EDGE,"E229.0.117"),sQuery(id+"F7.wireOp",EDGE,"E229.0.118"),sQuery(id+"F7.wireOp",EDGE,"E229.0.119"),sQuery(id+"F7.wireOp",EDGE,"E229.0.120"),sQuery(id+"F7.wireOp",EDGE,"E229.0.121"),sQuery(id+"F7.wireOp",EDGE,"E229.0.122"),sQuery(id+"F7.wireOp",EDGE,"E229.0.123"),sQuery(id+"F7.wireOp",EDGE,"E229.0.124"),sQuery(id+"F7.wireOp",EDGE,"E230.0"),sQuery(id+"F7.wireOp",EDGE,"E230.2"),sQuery(id+"F7.wireOp",EDGE,"E230.3"),sQuery(id+"F7.wireOp",EDGE,"E231"),sQuery(id+"F7.wireOp",EDGE,"E232")])],"isStart":false});
            extrude(context, id + "F30", {"entities" : qUnion([Q0, Q1, Q2]), "endBound" : BoundingType.UP_TO_SURFACE, "oppositeDirection" : true, "depth" : 25 * mm, "endBoundEntityFace" : qUnion([Q3]), "offsetDistance" : 25 * mm});
        }
        {
            var Q0;
            Q0=makeQuery(id+"F23.opExtrude","CAP_FACE",FACE,{"disambiguationData":[OSD([sQuery(id+"F22.wireOp",EDGE,"E252")])],"isStart":false});
            var sketch = newSketch(context, id + "F31", { "sketchPlane" : qUnion([Q0])});
            skCircle(sketch, "E259", {"center": v(-94.95, -9.9) * mm, "radius": 9 * mm});
            skCircle(sketch, "E260.0", {"center": v(-94.95, -9.9) * mm, "radius": 4 * mm});
            skSolve(sketch);
        }
        {
            var Q0;
            Q0=makeQuery(id+"F31.imprint","IMPRINT",FACE,{"disambiguationData":[TD([[makeQuery(id+"F31.imprint","IMPRINT",EDGE,{"derivedFrom":sQuery(id+"F31.wireOp",EDGE,"E259")}),1.0]])]});
            extrude(context, id + "F32", {"entities" : qUnion([Q0]), "endBound" : BoundingType.SYMMETRIC, "depth" : 25 * mm, "offsetDistance" : 25 * mm});
        }
        {
            var Q0;
            Q0=makeQuery(id+"F23.opExtrude","CAP_FACE",FACE,{"disambiguationData":[OSD([sQuery(id+"F22.wireOp",EDGE,"E253")])],"isStart":false});
            var sketch = newSketch(context, id + "F33", { "sketchPlane" : qUnion([Q0])});
            skCircle(sketch, "E261", {"center": v(45.55, 20.1) * mm, "radius": 4 * mm});
            skSolve(sketch);
        }
        {
            var Q0;
            Q0=makeQuery(id+"F33.imprint","IMPRINT",FACE,{"disambiguationData":[TD([[makeQuery(id+"F33.imprint","IMPRINT",EDGE,{"derivedFrom":makeQuery(id+"F23.opExtrude","CAP_EDGE",EDGE,{"disambiguationData":[OSD([sQuery(id+"F22.wireOp",EDGE,"E253")])],"isStart":false})}),1.0]])]});
            var Q1;
            Q1=makeQuery(id+"F33.imprint","IMPRINT",FACE,{"disambiguationData":[TD([[makeQuery(id+"F33.imprint","IMPRINT",EDGE,{"derivedFrom":sQuery(id+"F33.wireOp",EDGE,"E261")}),1.0]])]});
            var Q2;
            Q2=makeQuery(id+"F8.opExtrude","CAP_FACE",FACE,{"disambiguationData":[OSD([sQuery(id+"F7.wireOp",EDGE,"E229.0.0"),sQuery(id+"F7.wireOp",EDGE,"E229.0.1"),sQuery(id+"F7.wireOp",EDGE,"E229.0.2"),sQuery(id+"F7.wireOp",EDGE,"E229.0.3"),sQuery(id+"F7.wireOp",EDGE,"E229.0.4"),sQuery(id+"F7.wireOp",EDGE,"E229.0.5"),sQuery(id+"F7.wireOp",EDGE,"E229.0.6"),sQuery(id+"F7.wireOp",EDGE,"E229.0.7"),sQuery(id+"F7.wireOp",EDGE,"E229.0.8"),sQuery(id+"F7.wireOp",EDGE,"E229.0.9"),sQuery(id+"F7.wireOp",EDGE,"E229.0.10"),sQuery(id+"F7.wireOp",EDGE,"E229.0.11"),sQuery(id+"F7.wireOp",EDGE,"E229.0.12"),sQuery(id+"F7.wireOp",EDGE,"E229.0.13"),sQuery(id+"F7.wireOp",EDGE,"E229.0.14"),sQuery(id+"F7.wireOp",EDGE,"E229.0.15"),sQuery(id+"F7.wireOp",EDGE,"E229.0.16"),sQuery(id+"F7.wireOp",EDGE,"E229.0.17"),sQuery(id+"F7.wireOp",EDGE,"E229.0.18"),sQuery(id+"F7.wireOp",EDGE,"E229.0.19"),sQuery(id+"F7.wireOp",EDGE,"E229.0.20"),sQuery(id+"F7.wireOp",EDGE,"E229.0.21"),sQuery(id+"F7.wireOp",EDGE,"E229.0.22"),sQuery(id+"F7.wireOp",EDGE,"E229.0.23"),sQuery(id+"F7.wireOp",EDGE,"E229.0.24"),sQuery(id+"F7.wireOp",EDGE,"E229.0.25"),sQuery(id+"F7.wireOp",EDGE,"E229.0.26"),sQuery(id+"F7.wireOp",EDGE,"E229.0.27"),sQuery(id+"F7.wireOp",EDGE,"E229.0.28"),sQuery(id+"F7.wireOp",EDGE,"E229.0.29"),sQuery(id+"F7.wireOp",EDGE,"E229.0.30"),sQuery(id+"F7.wireOp",EDGE,"E229.0.31"),sQuery(id+"F7.wireOp",EDGE,"E229.0.32"),sQuery(id+"F7.wireOp",EDGE,"E229.0.33"),sQuery(id+"F7.wireOp",EDGE,"E229.0.34"),sQuery(id+"F7.wireOp",EDGE,"E229.0.35"),sQuery(id+"F7.wireOp",EDGE,"E229.0.36"),sQuery(id+"F7.wireOp",EDGE,"E229.0.37"),sQuery(id+"F7.wireOp",EDGE,"E229.0.38"),sQuery(id+"F7.wireOp",EDGE,"E229.0.39"),sQuery(id+"F7.wireOp",EDGE,"E229.0.40"),sQuery(id+"F7.wireOp",EDGE,"E229.0.41"),sQuery(id+"F7.wireOp",EDGE,"E229.0.42"),sQuery(id+"F7.wireOp",EDGE,"E229.0.43"),sQuery(id+"F7.wireOp",EDGE,"E229.0.44"),sQuery(id+"F7.wireOp",EDGE,"E229.0.45"),sQuery(id+"F7.wireOp",EDGE,"E229.0.46"),sQuery(id+"F7.wireOp",EDGE,"E229.0.47"),sQuery(id+"F7.wireOp",EDGE,"E229.0.48"),sQuery(id+"F7.wireOp",EDGE,"E229.0.49"),sQuery(id+"F7.wireOp",EDGE,"E229.0.50"),sQuery(id+"F7.wireOp",EDGE,"E229.0.51"),sQuery(id+"F7.wireOp",EDGE,"E229.0.52"),sQuery(id+"F7.wireOp",EDGE,"E229.0.53"),sQuery(id+"F7.wireOp",EDGE,"E229.0.54"),sQuery(id+"F7.wireOp",EDGE,"E229.0.55"),sQuery(id+"F7.wireOp",EDGE,"E229.0.56"),sQuery(id+"F7.wireOp",EDGE,"E229.0.57"),sQuery(id+"F7.wireOp",EDGE,"E229.0.58"),sQuery(id+"F7.wireOp",EDGE,"E229.0.59"),sQuery(id+"F7.wireOp",EDGE,"E229.0.60"),sQuery(id+"F7.wireOp",EDGE,"E229.0.61"),sQuery(id+"F7.wireOp",EDGE,"E229.0.62"),sQuery(id+"F7.wireOp",EDGE,"E229.0.63"),sQuery(id+"F7.wireOp",EDGE,"E229.0.64"),sQuery(id+"F7.wireOp",EDGE,"E229.0.65"),sQuery(id+"F7.wireOp",EDGE,"E229.0.66"),sQuery(id+"F7.wireOp",EDGE,"E229.0.67"),sQuery(id+"F7.wireOp",EDGE,"E229.0.68"),sQuery(id+"F7.wireOp",EDGE,"E229.0.69"),sQuery(id+"F7.wireOp",EDGE,"E229.0.70"),sQuery(id+"F7.wireOp",EDGE,"E229.0.71"),sQuery(id+"F7.wireOp",EDGE,"E229.0.72"),sQuery(id+"F7.wireOp",EDGE,"E229.0.73"),sQuery(id+"F7.wireOp",EDGE,"E229.0.74"),sQuery(id+"F7.wireOp",EDGE,"E229.0.75"),sQuery(id+"F7.wireOp",EDGE,"E229.0.76"),sQuery(id+"F7.wireOp",EDGE,"E229.0.77"),sQuery(id+"F7.wireOp",EDGE,"E229.0.78"),sQuery(id+"F7.wireOp",EDGE,"E229.0.79"),sQuery(id+"F7.wireOp",EDGE,"E229.0.80"),sQuery(id+"F7.wireOp",EDGE,"E229.0.81"),sQuery(id+"F7.wireOp",EDGE,"E229.0.82"),sQuery(id+"F7.wireOp",EDGE,"E229.0.83"),sQuery(id+"F7.wireOp",EDGE,"E229.0.84"),sQuery(id+"F7.wireOp",EDGE,"E229.0.85"),sQuery(id+"F7.wireOp",EDGE,"E229.0.86"),sQuery(id+"F7.wireOp",EDGE,"E229.0.87"),sQuery(id+"F7.wireOp",EDGE,"E229.0.88"),sQuery(id+"F7.wireOp",EDGE,"E229.0.89"),sQuery(id+"F7.wireOp",EDGE,"E229.0.90"),sQuery(id+"F7.wireOp",EDGE,"E229.0.91"),sQuery(id+"F7.wireOp",EDGE,"E229.0.92"),sQuery(id+"F7.wireOp",EDGE,"E229.0.93"),sQuery(id+"F7.wireOp",EDGE,"E229.0.94"),sQuery(id+"F7.wireOp",EDGE,"E229.0.95"),sQuery(id+"F7.wireOp",EDGE,"E229.0.96"),sQuery(id+"F7.wireOp",EDGE,"E229.0.97"),sQuery(id+"F7.wireOp",EDGE,"E229.0.98"),sQuery(id+"F7.wireOp",EDGE,"E229.0.99"),sQuery(id+"F7.wireOp",EDGE,"E229.0.100"),sQuery(id+"F7.wireOp",EDGE,"E229.0.101"),sQuery(id+"F7.wireOp",EDGE,"E229.0.102"),sQuery(id+"F7.wireOp",EDGE,"E229.0.103"),sQuery(id+"F7.wireOp",EDGE,"E229.0.104"),sQuery(id+"F7.wireOp",EDGE,"E229.0.105"),sQuery(id+"F7.wireOp",EDGE,"E229.0.106"),sQuery(id+"F7.wireOp",EDGE,"E229.0.107"),sQuery(id+"F7.wireOp",EDGE,"E229.0.108"),sQuery(id+"F7.wireOp",EDGE,"E229.0.109"),sQuery(id+"F7.wireOp",EDGE,"E229.0.110"),sQuery(id+"F7.wireOp",EDGE,"E229.0.111"),sQuery(id+"F7.wireOp",EDGE,"E229.0.112"),sQuery(id+"F7.wireOp",EDGE,"E229.0.113"),sQuery(id+"F7.wireOp",EDGE,"E229.0.114"),sQuery(id+"F7.wireOp",EDGE,"E229.0.115"),sQuery(id+"F7.wireOp",EDGE,"E229.0.116"),sQuery(id+"F7.wireOp",EDGE,"E229.0.117"),sQuery(id+"F7.wireOp",EDGE,"E229.0.118"),sQuery(id+"F7.wireOp",EDGE,"E229.0.119"),sQuery(id+"F7.wireOp",EDGE,"E229.0.120"),sQuery(id+"F7.wireOp",EDGE,"E229.0.121"),sQuery(id+"F7.wireOp",EDGE,"E229.0.122"),sQuery(id+"F7.wireOp",EDGE,"E229.0.123"),sQuery(id+"F7.wireOp",EDGE,"E229.0.124"),sQuery(id+"F7.wireOp",EDGE,"E230.0"),sQuery(id+"F7.wireOp",EDGE,"E230.2"),sQuery(id+"F7.wireOp",EDGE,"E230.3"),sQuery(id+"F7.wireOp",EDGE,"E231"),sQuery(id+"F7.wireOp",EDGE,"E232")])],"isStart":false});
            extrude(context, id + "F34", {"entities" : qUnion([Q0, Q1]), "endBound" : BoundingType.UP_TO_SURFACE, "depth" : 25 * mm, "endBoundEntityFace" : qUnion([Q2]), "offsetDistance" : 25 * mm});
        }
        {
            var Q0;
            Q0=makeQuery(id+"F23.opExtrude","CAP_FACE",FACE,{"disambiguationData":[OSD([sQuery(id+"F22.wireOp",EDGE,"E253")])],"isStart":false});
            var sketch = newSketch(context, id + "F35", { "sketchPlane" : qUnion([Q0])});
            skCircle(sketch, "E262.0", {"center": v(45.55, 20.1) * mm, "radius": 4 * mm});
            skCircle(sketch, "E263", {"center": v(45.55, 20.1) * mm, "radius": 9 * mm});
            skSolve(sketch);
        }
        {
            var Q0;
            Q0=makeQuery(id+"F35.imprint","IMPRINT",FACE,{"disambiguationData":[TD([[makeQuery(id+"F35.imprint","IMPRINT",EDGE,{"derivedFrom":sQuery(id+"F35.wireOp",EDGE,"E262.0")}),-1.0]])]});
            extrude(context, id + "F36", {"entities" : qUnion([Q0]), "endBound" : BoundingType.SYMMETRIC, "depth" : 25 * mm, "offsetDistance" : 25 * mm});
        }
        {
            var Q0;
            Q0=makeQuery(id+"F2.opExtrude","CAP_FACE",FACE,{"disambiguationData":[OSD([sQuery(id+"F1.wireOp",EDGE,"E0"),sQuery(id+"F1.wireOp",EDGE,"E1"),sQuery(id+"F1.wireOp",EDGE,"E2"),sQuery(id+"F1.wireOp",EDGE,"E3"),sQuery(id+"F1.wireOp",EDGE,"E4"),sQuery(id+"F1.wireOp",EDGE,"E5"),sQuery(id+"F1.wireOp",EDGE,"E6"),sQuery(id+"F1.wireOp",EDGE,"E7"),sQuery(id+"F1.wireOp",EDGE,"E8"),sQuery(id+"F1.wireOp",EDGE,"E9"),sQuery(id+"F1.wireOp",EDGE,"E10"),sQuery(id+"F1.wireOp",EDGE,"E11"),sQuery(id+"F1.wireOp",EDGE,"E12"),sQuery(id+"F1.wireOp",EDGE,"E13"),sQuery(id+"F1.wireOp",EDGE,"E14"),sQuery(id+"F1.wireOp",EDGE,"E15"),sQuery(id+"F1.wireOp",EDGE,"E16"),sQuery(id+"F1.wireOp",EDGE,"E17"),sQuery(id+"F1.wireOp",EDGE,"E18"),sQuery(id+"F1.wireOp",EDGE,"E19"),sQuery(id+"F1.wireOp",EDGE,"E20"),sQuery(id+"F1.wireOp",EDGE,"E21"),sQuery(id+"F1.wireOp",EDGE,"E22"),sQuery(id+"F1.wireOp",EDGE,"E23"),sQuery(id+"F1.wireOp",EDGE,"E24"),sQuery(id+"F1.wireOp",EDGE,"E25"),sQuery(id+"F1.wireOp",EDGE,"E26"),sQuery(id+"F1.wireOp",EDGE,"E27"),sQuery(id+"F1.wireOp",EDGE,"E28"),sQuery(id+"F1.wireOp",EDGE,"E29"),sQuery(id+"F1.wireOp",EDGE,"E30"),sQuery(id+"F1.wireOp",EDGE,"E31"),sQuery(id+"F1.wireOp",EDGE,"E32"),sQuery(id+"F1.wireOp",EDGE,"E33"),sQuery(id+"F1.wireOp",EDGE,"E34"),sQuery(id+"F1.wireOp",EDGE,"E35"),sQuery(id+"F1.wireOp",EDGE,"E36"),sQuery(id+"F1.wireOp",EDGE,"E37"),sQuery(id+"F1.wireOp",EDGE,"E38"),sQuery(id+"F1.wireOp",EDGE,"E39"),sQuery(id+"F1.wireOp",EDGE,"E40"),sQuery(id+"F1.wireOp",EDGE,"E41"),sQuery(id+"F1.wireOp",EDGE,"E42"),sQuery(id+"F1.wireOp",EDGE,"E43"),sQuery(id+"F1.wireOp",EDGE,"E44"),sQuery(id+"F1.wireOp",EDGE,"E45"),sQuery(id+"F1.wireOp",EDGE,"E46"),sQuery(id+"F1.wireOp",EDGE,"E47"),sQuery(id+"F1.wireOp",EDGE,"E48"),sQuery(id+"F1.wireOp",EDGE,"E49"),sQuery(id+"F1.wireOp",EDGE,"E50"),sQuery(id+"F1.wireOp",EDGE,"E51"),sQuery(id+"F1.wireOp",EDGE,"E52"),sQuery(id+"F1.wireOp",EDGE,"E53"),sQuery(id+"F1.wireOp",EDGE,"E54"),sQuery(id+"F1.wireOp",EDGE,"E55"),sQuery(id+"F1.wireOp",EDGE,"E56"),sQuery(id+"F1.wireOp",EDGE,"E57"),sQuery(id+"F1.wireOp",EDGE,"E58"),sQuery(id+"F1.wireOp",EDGE,"E59"),sQuery(id+"F1.wireOp",EDGE,"E60"),sQuery(id+"F1.wireOp",EDGE,"E61"),sQuery(id+"F1.wireOp",EDGE,"E62"),sQuery(id+"F1.wireOp",EDGE,"E63"),sQuery(id+"F1.wireOp",EDGE,"E64"),sQuery(id+"F1.wireOp",EDGE,"E65"),sQuery(id+"F1.wireOp",EDGE,"E66"),sQuery(id+"F1.wireOp",EDGE,"E67"),sQuery(id+"F1.wireOp",EDGE,"E68"),sQuery(id+"F1.wireOp",EDGE,"E69"),sQuery(id+"F1.wireOp",EDGE,"E70"),sQuery(id+"F1.wireOp",EDGE,"E71"),sQuery(id+"F1.wireOp",EDGE,"E72"),sQuery(id+"F1.wireOp",EDGE,"E73"),sQuery(id+"F1.wireOp",EDGE,"E74"),sQuery(id+"F1.wireOp",EDGE,"E75"),sQuery(id+"F1.wireOp",EDGE,"E76"),sQuery(id+"F1.wireOp",EDGE,"E77"),sQuery(id+"F1.wireOp",EDGE,"E78"),sQuery(id+"F1.wireOp",EDGE,"E79"),sQuery(id+"F1.wireOp",EDGE,"E80"),sQuery(id+"F1.wireOp",EDGE,"E81"),sQuery(id+"F1.wireOp",EDGE,"E82"),sQuery(id+"F1.wireOp",EDGE,"E83"),sQuery(id+"F1.wireOp",EDGE,"E84"),sQuery(id+"F1.wireOp",EDGE,"E85"),sQuery(id+"F1.wireOp",EDGE,"E86"),sQuery(id+"F1.wireOp",EDGE,"E87"),sQuery(id+"F1.wireOp",EDGE,"E88"),sQuery(id+"F1.wireOp",EDGE,"E89"),sQuery(id+"F1.wireOp",EDGE,"E90"),sQuery(id+"F1.wireOp",EDGE,"E91"),sQuery(id+"F1.wireOp",EDGE,"E92"),sQuery(id+"F1.wireOp",EDGE,"E93"),sQuery(id+"F1.wireOp",EDGE,"E94"),sQuery(id+"F1.wireOp",EDGE,"E95"),sQuery(id+"F1.wireOp",EDGE,"E96"),sQuery(id+"F1.wireOp",EDGE,"E97"),sQuery(id+"F1.wireOp",EDGE,"E98"),sQuery(id+"F1.wireOp",EDGE,"E99"),sQuery(id+"F1.wireOp",EDGE,"E100"),sQuery(id+"F1.wireOp",EDGE,"E101"),sQuery(id+"F1.wireOp",EDGE,"E102"),sQuery(id+"F1.wireOp",EDGE,"E103"),sQuery(id+"F1.wireOp",EDGE,"E104"),sQuery(id+"F1.wireOp",EDGE,"E105"),sQuery(id+"F1.wireOp",EDGE,"E106"),sQuery(id+"F1.wireOp",EDGE,"E107"),sQuery(id+"F1.wireOp",EDGE,"E108"),sQuery(id+"F1.wireOp",EDGE,"E109"),sQuery(id+"F1.wireOp",EDGE,"E110"),sQuery(id+"F1.wireOp",EDGE,"E111"),sQuery(id+"F1.wireOp",EDGE,"E112"),sQuery(id+"F1.wireOp",EDGE,"E113"),sQuery(id+"F1.wireOp",EDGE,"E114"),sQuery(id+"F1.wireOp",EDGE,"E115"),sQuery(id+"F1.wireOp",EDGE,"E116"),sQuery(id+"F1.wireOp",EDGE,"E117"),sQuery(id+"F1.wireOp",EDGE,"E118"),sQuery(id+"F1.wireOp",EDGE,"E119"),sQuery(id+"F1.wireOp",EDGE,"E120"),sQuery(id+"F1.wireOp",EDGE,"E121"),sQuery(id+"F1.wireOp",EDGE,"E122"),sQuery(id+"F1.wireOp",EDGE,"E123"),sQuery(id+"F1.wireOp",EDGE,"E124"),sQuery(id+"F1.wireOp",EDGE,"E125"),sQuery(id+"F1.wireOp",EDGE,"E126"),sQuery(id+"F1.wireOp",EDGE,"E127"),sQuery(id+"F1.wireOp",EDGE,"E128"),sQuery(id+"F1.wireOp",EDGE,"E129"),sQuery(id+"F1.wireOp",EDGE,"E130"),sQuery(id+"F1.wireOp",EDGE,"E131"),sQuery(id+"F1.wireOp",EDGE,"E132"),sQuery(id+"F1.wireOp",EDGE,"E133"),sQuery(id+"F1.wireOp",EDGE,"E134"),sQuery(id+"F1.wireOp",EDGE,"E135"),sQuery(id+"F1.wireOp",EDGE,"E136"),sQuery(id+"F1.wireOp",EDGE,"E137"),sQuery(id+"F1.wireOp",EDGE,"E138"),sQuery(id+"F1.wireOp",EDGE,"E139"),sQuery(id+"F1.wireOp",EDGE,"E140"),sQuery(id+"F1.wireOp",EDGE,"E141"),sQuery(id+"F1.wireOp",EDGE,"E142"),sQuery(id+"F1.wireOp",EDGE,"E143"),sQuery(id+"F1.wireOp",EDGE,"E144"),sQuery(id+"F1.wireOp",EDGE,"E145"),sQuery(id+"F1.wireOp",EDGE,"E146"),sQuery(id+"F1.wireOp",EDGE,"E147"),sQuery(id+"F1.wireOp",EDGE,"E148"),sQuery(id+"F1.wireOp",EDGE,"E149"),sQuery(id+"F1.wireOp",EDGE,"E150"),sQuery(id+"F1.wireOp",EDGE,"E151"),sQuery(id+"F1.wireOp",EDGE,"E152"),sQuery(id+"F1.wireOp",EDGE,"E153"),sQuery(id+"F1.wireOp",EDGE,"E155"),sQuery(id+"F1.wireOp",EDGE,"E157"),sQuery(id+"F1.wireOp",EDGE,"E159"),sQuery(id+"F1.wireOp",EDGE,"E163"),sQuery(id+"F1.wireOp",EDGE,"E164"),sQuery(id+"F1.wireOp",EDGE,"E165"),sQuery(id+"F1.wireOp",EDGE,"E168"),sQuery(id+"F1.wireOp",EDGE,"E170"),sQuery(id+"F1.wireOp",EDGE,"E175"),sQuery(id+"F1.wireOp",EDGE,"E176"),sQuery(id+"F1.wireOp",EDGE,"E177"),sQuery(id+"F1.wireOp",EDGE,"E178")])],"isStart":false});
            var sketch = newSketch(context, id + "F37", { "sketchPlane" : qUnion([Q0])});
            skCircle(sketch, "E264", {"center": v(-21.05, 20.1) * mm, "radius": 4 * mm});
            skCircle(sketch, "E265", {"center": v(-70.05, 20.1) * mm, "radius": 4 * mm});
            skSolve(sketch);
        }
        {
            var Q0;
            Q0=makeQuery(id+"F37.imprint","IMPRINT",FACE,{"disambiguationData":[TD([[makeQuery(id+"F37.imprint","IMPRINT",EDGE,{"derivedFrom":sQuery(id+"F37.wireOp",EDGE,"E264")}),1.0]])]});
            var Q1;
            Q1=makeQuery(id+"F37.imprint","IMPRINT",FACE,{"disambiguationData":[TD([[makeQuery(id+"F37.imprint","IMPRINT",EDGE,{"derivedFrom":sQuery(id+"F37.wireOp",EDGE,"E265")}),1.0]])]});
            var Q2;
            Q2=makeQuery(id+"F8.opExtrude","CAP_FACE",FACE,{"disambiguationData":[OSD([sQuery(id+"F7.wireOp",EDGE,"E229.0.0"),sQuery(id+"F7.wireOp",EDGE,"E229.0.1"),sQuery(id+"F7.wireOp",EDGE,"E229.0.2"),sQuery(id+"F7.wireOp",EDGE,"E229.0.3"),sQuery(id+"F7.wireOp",EDGE,"E229.0.4"),sQuery(id+"F7.wireOp",EDGE,"E229.0.5"),sQuery(id+"F7.wireOp",EDGE,"E229.0.6"),sQuery(id+"F7.wireOp",EDGE,"E229.0.7"),sQuery(id+"F7.wireOp",EDGE,"E229.0.8"),sQuery(id+"F7.wireOp",EDGE,"E229.0.9"),sQuery(id+"F7.wireOp",EDGE,"E229.0.10"),sQuery(id+"F7.wireOp",EDGE,"E229.0.11"),sQuery(id+"F7.wireOp",EDGE,"E229.0.12"),sQuery(id+"F7.wireOp",EDGE,"E229.0.13"),sQuery(id+"F7.wireOp",EDGE,"E229.0.14"),sQuery(id+"F7.wireOp",EDGE,"E229.0.15"),sQuery(id+"F7.wireOp",EDGE,"E229.0.16"),sQuery(id+"F7.wireOp",EDGE,"E229.0.17"),sQuery(id+"F7.wireOp",EDGE,"E229.0.18"),sQuery(id+"F7.wireOp",EDGE,"E229.0.19"),sQuery(id+"F7.wireOp",EDGE,"E229.0.20"),sQuery(id+"F7.wireOp",EDGE,"E229.0.21"),sQuery(id+"F7.wireOp",EDGE,"E229.0.22"),sQuery(id+"F7.wireOp",EDGE,"E229.0.23"),sQuery(id+"F7.wireOp",EDGE,"E229.0.24"),sQuery(id+"F7.wireOp",EDGE,"E229.0.25"),sQuery(id+"F7.wireOp",EDGE,"E229.0.26"),sQuery(id+"F7.wireOp",EDGE,"E229.0.27"),sQuery(id+"F7.wireOp",EDGE,"E229.0.28"),sQuery(id+"F7.wireOp",EDGE,"E229.0.29"),sQuery(id+"F7.wireOp",EDGE,"E229.0.30"),sQuery(id+"F7.wireOp",EDGE,"E229.0.31"),sQuery(id+"F7.wireOp",EDGE,"E229.0.32"),sQuery(id+"F7.wireOp",EDGE,"E229.0.33"),sQuery(id+"F7.wireOp",EDGE,"E229.0.34"),sQuery(id+"F7.wireOp",EDGE,"E229.0.35"),sQuery(id+"F7.wireOp",EDGE,"E229.0.36"),sQuery(id+"F7.wireOp",EDGE,"E229.0.37"),sQuery(id+"F7.wireOp",EDGE,"E229.0.38"),sQuery(id+"F7.wireOp",EDGE,"E229.0.39"),sQuery(id+"F7.wireOp",EDGE,"E229.0.40"),sQuery(id+"F7.wireOp",EDGE,"E229.0.41"),sQuery(id+"F7.wireOp",EDGE,"E229.0.42"),sQuery(id+"F7.wireOp",EDGE,"E229.0.43"),sQuery(id+"F7.wireOp",EDGE,"E229.0.44"),sQuery(id+"F7.wireOp",EDGE,"E229.0.45"),sQuery(id+"F7.wireOp",EDGE,"E229.0.46"),sQuery(id+"F7.wireOp",EDGE,"E229.0.47"),sQuery(id+"F7.wireOp",EDGE,"E229.0.48"),sQuery(id+"F7.wireOp",EDGE,"E229.0.49"),sQuery(id+"F7.wireOp",EDGE,"E229.0.50"),sQuery(id+"F7.wireOp",EDGE,"E229.0.51"),sQuery(id+"F7.wireOp",EDGE,"E229.0.52"),sQuery(id+"F7.wireOp",EDGE,"E229.0.53"),sQuery(id+"F7.wireOp",EDGE,"E229.0.54"),sQuery(id+"F7.wireOp",EDGE,"E229.0.55"),sQuery(id+"F7.wireOp",EDGE,"E229.0.56"),sQuery(id+"F7.wireOp",EDGE,"E229.0.57"),sQuery(id+"F7.wireOp",EDGE,"E229.0.58"),sQuery(id+"F7.wireOp",EDGE,"E229.0.59"),sQuery(id+"F7.wireOp",EDGE,"E229.0.60"),sQuery(id+"F7.wireOp",EDGE,"E229.0.61"),sQuery(id+"F7.wireOp",EDGE,"E229.0.62"),sQuery(id+"F7.wireOp",EDGE,"E229.0.63"),sQuery(id+"F7.wireOp",EDGE,"E229.0.64"),sQuery(id+"F7.wireOp",EDGE,"E229.0.65"),sQuery(id+"F7.wireOp",EDGE,"E229.0.66"),sQuery(id+"F7.wireOp",EDGE,"E229.0.67"),sQuery(id+"F7.wireOp",EDGE,"E229.0.68"),sQuery(id+"F7.wireOp",EDGE,"E229.0.69"),sQuery(id+"F7.wireOp",EDGE,"E229.0.70"),sQuery(id+"F7.wireOp",EDGE,"E229.0.71"),sQuery(id+"F7.wireOp",EDGE,"E229.0.72"),sQuery(id+"F7.wireOp",EDGE,"E229.0.73"),sQuery(id+"F7.wireOp",EDGE,"E229.0.74"),sQuery(id+"F7.wireOp",EDGE,"E229.0.75"),sQuery(id+"F7.wireOp",EDGE,"E229.0.76"),sQuery(id+"F7.wireOp",EDGE,"E229.0.77"),sQuery(id+"F7.wireOp",EDGE,"E229.0.78"),sQuery(id+"F7.wireOp",EDGE,"E229.0.79"),sQuery(id+"F7.wireOp",EDGE,"E229.0.80"),sQuery(id+"F7.wireOp",EDGE,"E229.0.81"),sQuery(id+"F7.wireOp",EDGE,"E229.0.82"),sQuery(id+"F7.wireOp",EDGE,"E229.0.83"),sQuery(id+"F7.wireOp",EDGE,"E229.0.84"),sQuery(id+"F7.wireOp",EDGE,"E229.0.85"),sQuery(id+"F7.wireOp",EDGE,"E229.0.86"),sQuery(id+"F7.wireOp",EDGE,"E229.0.87"),sQuery(id+"F7.wireOp",EDGE,"E229.0.88"),sQuery(id+"F7.wireOp",EDGE,"E229.0.89"),sQuery(id+"F7.wireOp",EDGE,"E229.0.90"),sQuery(id+"F7.wireOp",EDGE,"E229.0.91"),sQuery(id+"F7.wireOp",EDGE,"E229.0.92"),sQuery(id+"F7.wireOp",EDGE,"E229.0.93"),sQuery(id+"F7.wireOp",EDGE,"E229.0.94"),sQuery(id+"F7.wireOp",EDGE,"E229.0.95"),sQuery(id+"F7.wireOp",EDGE,"E229.0.96"),sQuery(id+"F7.wireOp",EDGE,"E229.0.97"),sQuery(id+"F7.wireOp",EDGE,"E229.0.98"),sQuery(id+"F7.wireOp",EDGE,"E229.0.99"),sQuery(id+"F7.wireOp",EDGE,"E229.0.100"),sQuery(id+"F7.wireOp",EDGE,"E229.0.101"),sQuery(id+"F7.wireOp",EDGE,"E229.0.102"),sQuery(id+"F7.wireOp",EDGE,"E229.0.103"),sQuery(id+"F7.wireOp",EDGE,"E229.0.104"),sQuery(id+"F7.wireOp",EDGE,"E229.0.105"),sQuery(id+"F7.wireOp",EDGE,"E229.0.106"),sQuery(id+"F7.wireOp",EDGE,"E229.0.107"),sQuery(id+"F7.wireOp",EDGE,"E229.0.108"),sQuery(id+"F7.wireOp",EDGE,"E229.0.109"),sQuery(id+"F7.wireOp",EDGE,"E229.0.110"),sQuery(id+"F7.wireOp",EDGE,"E229.0.111"),sQuery(id+"F7.wireOp",EDGE,"E229.0.112"),sQuery(id+"F7.wireOp",EDGE,"E229.0.113"),sQuery(id+"F7.wireOp",EDGE,"E229.0.114"),sQuery(id+"F7.wireOp",EDGE,"E229.0.115"),sQuery(id+"F7.wireOp",EDGE,"E229.0.116"),sQuery(id+"F7.wireOp",EDGE,"E229.0.117"),sQuery(id+"F7.wireOp",EDGE,"E229.0.118"),sQuery(id+"F7.wireOp",EDGE,"E229.0.119"),sQuery(id+"F7.wireOp",EDGE,"E229.0.120"),sQuery(id+"F7.wireOp",EDGE,"E229.0.121"),sQuery(id+"F7.wireOp",EDGE,"E229.0.122"),sQuery(id+"F7.wireOp",EDGE,"E229.0.123"),sQuery(id+"F7.wireOp",EDGE,"E229.0.124"),sQuery(id+"F7.wireOp",EDGE,"E230.0"),sQuery(id+"F7.wireOp",EDGE,"E230.2"),sQuery(id+"F7.wireOp",EDGE,"E230.3"),sQuery(id+"F7.wireOp",EDGE,"E231"),sQuery(id+"F7.wireOp",EDGE,"E232")])],"isStart":false});
            extrude(context, id + "F38", {"entities" : qUnion([Q0, Q1]), "endBound" : BoundingType.UP_TO_SURFACE, "oppositeDirection" : true, "depth" : 25 * mm, "endBoundEntityFace" : qUnion([Q2]), "offsetDistance" : 25 * mm});
        }
        {
            var Q0;
            Q0=makeQuery(id+"F2.opExtrude","CAP_FACE",FACE,{"disambiguationData":[OSD([sQuery(id+"F1.wireOp",EDGE,"E0"),sQuery(id+"F1.wireOp",EDGE,"E1"),sQuery(id+"F1.wireOp",EDGE,"E2"),sQuery(id+"F1.wireOp",EDGE,"E3"),sQuery(id+"F1.wireOp",EDGE,"E4"),sQuery(id+"F1.wireOp",EDGE,"E5"),sQuery(id+"F1.wireOp",EDGE,"E6"),sQuery(id+"F1.wireOp",EDGE,"E7"),sQuery(id+"F1.wireOp",EDGE,"E8"),sQuery(id+"F1.wireOp",EDGE,"E9"),sQuery(id+"F1.wireOp",EDGE,"E10"),sQuery(id+"F1.wireOp",EDGE,"E11"),sQuery(id+"F1.wireOp",EDGE,"E12"),sQuery(id+"F1.wireOp",EDGE,"E13"),sQuery(id+"F1.wireOp",EDGE,"E14"),sQuery(id+"F1.wireOp",EDGE,"E15"),sQuery(id+"F1.wireOp",EDGE,"E16"),sQuery(id+"F1.wireOp",EDGE,"E17"),sQuery(id+"F1.wireOp",EDGE,"E18"),sQuery(id+"F1.wireOp",EDGE,"E19"),sQuery(id+"F1.wireOp",EDGE,"E20"),sQuery(id+"F1.wireOp",EDGE,"E21"),sQuery(id+"F1.wireOp",EDGE,"E22"),sQuery(id+"F1.wireOp",EDGE,"E23"),sQuery(id+"F1.wireOp",EDGE,"E24"),sQuery(id+"F1.wireOp",EDGE,"E25"),sQuery(id+"F1.wireOp",EDGE,"E26"),sQuery(id+"F1.wireOp",EDGE,"E27"),sQuery(id+"F1.wireOp",EDGE,"E28"),sQuery(id+"F1.wireOp",EDGE,"E29"),sQuery(id+"F1.wireOp",EDGE,"E30"),sQuery(id+"F1.wireOp",EDGE,"E31"),sQuery(id+"F1.wireOp",EDGE,"E32"),sQuery(id+"F1.wireOp",EDGE,"E33"),sQuery(id+"F1.wireOp",EDGE,"E34"),sQuery(id+"F1.wireOp",EDGE,"E35"),sQuery(id+"F1.wireOp",EDGE,"E36"),sQuery(id+"F1.wireOp",EDGE,"E37"),sQuery(id+"F1.wireOp",EDGE,"E38"),sQuery(id+"F1.wireOp",EDGE,"E39"),sQuery(id+"F1.wireOp",EDGE,"E40"),sQuery(id+"F1.wireOp",EDGE,"E41"),sQuery(id+"F1.wireOp",EDGE,"E42"),sQuery(id+"F1.wireOp",EDGE,"E43"),sQuery(id+"F1.wireOp",EDGE,"E44"),sQuery(id+"F1.wireOp",EDGE,"E45"),sQuery(id+"F1.wireOp",EDGE,"E46"),sQuery(id+"F1.wireOp",EDGE,"E47"),sQuery(id+"F1.wireOp",EDGE,"E48"),sQuery(id+"F1.wireOp",EDGE,"E49"),sQuery(id+"F1.wireOp",EDGE,"E50"),sQuery(id+"F1.wireOp",EDGE,"E51"),sQuery(id+"F1.wireOp",EDGE,"E52"),sQuery(id+"F1.wireOp",EDGE,"E53"),sQuery(id+"F1.wireOp",EDGE,"E54"),sQuery(id+"F1.wireOp",EDGE,"E55"),sQuery(id+"F1.wireOp",EDGE,"E56"),sQuery(id+"F1.wireOp",EDGE,"E57"),sQuery(id+"F1.wireOp",EDGE,"E58"),sQuery(id+"F1.wireOp",EDGE,"E59"),sQuery(id+"F1.wireOp",EDGE,"E60"),sQuery(id+"F1.wireOp",EDGE,"E61"),sQuery(id+"F1.wireOp",EDGE,"E62"),sQuery(id+"F1.wireOp",EDGE,"E63"),sQuery(id+"F1.wireOp",EDGE,"E64"),sQuery(id+"F1.wireOp",EDGE,"E65"),sQuery(id+"F1.wireOp",EDGE,"E66"),sQuery(id+"F1.wireOp",EDGE,"E67"),sQuery(id+"F1.wireOp",EDGE,"E68"),sQuery(id+"F1.wireOp",EDGE,"E69"),sQuery(id+"F1.wireOp",EDGE,"E70"),sQuery(id+"F1.wireOp",EDGE,"E71"),sQuery(id+"F1.wireOp",EDGE,"E72"),sQuery(id+"F1.wireOp",EDGE,"E73"),sQuery(id+"F1.wireOp",EDGE,"E74"),sQuery(id+"F1.wireOp",EDGE,"E75"),sQuery(id+"F1.wireOp",EDGE,"E76"),sQuery(id+"F1.wireOp",EDGE,"E77"),sQuery(id+"F1.wireOp",EDGE,"E78"),sQuery(id+"F1.wireOp",EDGE,"E79"),sQuery(id+"F1.wireOp",EDGE,"E80"),sQuery(id+"F1.wireOp",EDGE,"E81"),sQuery(id+"F1.wireOp",EDGE,"E82"),sQuery(id+"F1.wireOp",EDGE,"E83"),sQuery(id+"F1.wireOp",EDGE,"E84"),sQuery(id+"F1.wireOp",EDGE,"E85"),sQuery(id+"F1.wireOp",EDGE,"E86"),sQuery(id+"F1.wireOp",EDGE,"E87"),sQuery(id+"F1.wireOp",EDGE,"E88"),sQuery(id+"F1.wireOp",EDGE,"E89"),sQuery(id+"F1.wireOp",EDGE,"E90"),sQuery(id+"F1.wireOp",EDGE,"E91"),sQuery(id+"F1.wireOp",EDGE,"E92"),sQuery(id+"F1.wireOp",EDGE,"E93"),sQuery(id+"F1.wireOp",EDGE,"E94"),sQuery(id+"F1.wireOp",EDGE,"E95"),sQuery(id+"F1.wireOp",EDGE,"E96"),sQuery(id+"F1.wireOp",EDGE,"E97"),sQuery(id+"F1.wireOp",EDGE,"E98"),sQuery(id+"F1.wireOp",EDGE,"E99"),sQuery(id+"F1.wireOp",EDGE,"E100"),sQuery(id+"F1.wireOp",EDGE,"E101"),sQuery(id+"F1.wireOp",EDGE,"E102"),sQuery(id+"F1.wireOp",EDGE,"E103"),sQuery(id+"F1.wireOp",EDGE,"E104"),sQuery(id+"F1.wireOp",EDGE,"E105"),sQuery(id+"F1.wireOp",EDGE,"E106"),sQuery(id+"F1.wireOp",EDGE,"E107"),sQuery(id+"F1.wireOp",EDGE,"E108"),sQuery(id+"F1.wireOp",EDGE,"E109"),sQuery(id+"F1.wireOp",EDGE,"E110"),sQuery(id+"F1.wireOp",EDGE,"E111"),sQuery(id+"F1.wireOp",EDGE,"E112"),sQuery(id+"F1.wireOp",EDGE,"E113"),sQuery(id+"F1.wireOp",EDGE,"E114"),sQuery(id+"F1.wireOp",EDGE,"E115"),sQuery(id+"F1.wireOp",EDGE,"E116"),sQuery(id+"F1.wireOp",EDGE,"E117"),sQuery(id+"F1.wireOp",EDGE,"E118"),sQuery(id+"F1.wireOp",EDGE,"E119"),sQuery(id+"F1.wireOp",EDGE,"E120"),sQuery(id+"F1.wireOp",EDGE,"E121"),sQuery(id+"F1.wireOp",EDGE,"E122"),sQuery(id+"F1.wireOp",EDGE,"E123"),sQuery(id+"F1.wireOp",EDGE,"E124"),sQuery(id+"F1.wireOp",EDGE,"E125"),sQuery(id+"F1.wireOp",EDGE,"E126"),sQuery(id+"F1.wireOp",EDGE,"E127"),sQuery(id+"F1.wireOp",EDGE,"E128"),sQuery(id+"F1.wireOp",EDGE,"E129"),sQuery(id+"F1.wireOp",EDGE,"E130"),sQuery(id+"F1.wireOp",EDGE,"E131"),sQuery(id+"F1.wireOp",EDGE,"E132"),sQuery(id+"F1.wireOp",EDGE,"E133"),sQuery(id+"F1.wireOp",EDGE,"E134"),sQuery(id+"F1.wireOp",EDGE,"E135"),sQuery(id+"F1.wireOp",EDGE,"E136"),sQuery(id+"F1.wireOp",EDGE,"E137"),sQuery(id+"F1.wireOp",EDGE,"E138"),sQuery(id+"F1.wireOp",EDGE,"E139"),sQuery(id+"F1.wireOp",EDGE,"E140"),sQuery(id+"F1.wireOp",EDGE,"E141"),sQuery(id+"F1.wireOp",EDGE,"E142"),sQuery(id+"F1.wireOp",EDGE,"E143"),sQuery(id+"F1.wireOp",EDGE,"E144"),sQuery(id+"F1.wireOp",EDGE,"E145"),sQuery(id+"F1.wireOp",EDGE,"E146"),sQuery(id+"F1.wireOp",EDGE,"E147"),sQuery(id+"F1.wireOp",EDGE,"E148"),sQuery(id+"F1.wireOp",EDGE,"E149"),sQuery(id+"F1.wireOp",EDGE,"E150"),sQuery(id+"F1.wireOp",EDGE,"E151"),sQuery(id+"F1.wireOp",EDGE,"E152"),sQuery(id+"F1.wireOp",EDGE,"E153"),sQuery(id+"F1.wireOp",EDGE,"E155"),sQuery(id+"F1.wireOp",EDGE,"E157"),sQuery(id+"F1.wireOp",EDGE,"E159"),sQuery(id+"F1.wireOp",EDGE,"E163"),sQuery(id+"F1.wireOp",EDGE,"E164"),sQuery(id+"F1.wireOp",EDGE,"E165"),sQuery(id+"F1.wireOp",EDGE,"E168"),sQuery(id+"F1.wireOp",EDGE,"E170"),sQuery(id+"F1.wireOp",EDGE,"E175"),sQuery(id+"F1.wireOp",EDGE,"E176"),sQuery(id+"F1.wireOp",EDGE,"E177"),sQuery(id+"F1.wireOp",EDGE,"E178")])],"isStart":true});
            cPlane(context, id + "F39", {"entities" : qUnion([Q0]), "cplaneType" : CPlaneType.OFFSET, "offset" : 70 * mm, "width" : 150 * mm, "height" : 150 * mm});
        }
        {
            var Q0;
            Q0=qCreatedBy(id+"F39.planeOp",FACE);
            cPlane(context, id + "F40", {"entities" : qUnion([Q0]), "cplaneType" : CPlaneType.OFFSET, "offset" : 40 * mm, "width" : 150 * mm, "height" : 150 * mm});
        }
        {
            var Q0;
            Q0=qCreatedBy(id+"F40.planeOp",FACE);
            cPlane(context, id + "F41", {"entities" : qUnion([Q0]), "cplaneType" : CPlaneType.OFFSET, "offset" : 40 * mm, "width" : 150 * mm, "height" : 150 * mm});
        }
        {
            var Q0;
            Q0=qCreatedBy(id+"F41.planeOp",FACE);
            cPlane(context, id + "F42", {"entities" : qUnion([Q0]), "cplaneType" : CPlaneType.OFFSET, "offset" : 40 * mm, "width" : 150 * mm, "height" : 150 * mm});
        }
        {
            var Q0;
            Q0=qCreatedBy(id+"F39.planeOp",FACE);
            var sketch = newSketch(context, id + "F43", { "sketchPlane" : qUnion([Q0])});
            skCircle(sketch, "E266.0", {"center": v(-19.95, -9.9) * mm, "radius": 4 * mm});
            skCircle(sketch, "E266.1", {"center": v(-94.95, -9.9) * mm, "radius": 4 * mm});
            skCircle(sketch, "E267", {"center": v(-94.95, -9.9) * mm, "radius": 5.5 * mm});
            skCircle(sketch, "E268", {"center": v(-19.95, -9.9) * mm, "radius": 5.5 * mm});
            skSolve(sketch);
        }
        {
            var Q0;
            Q0=qCreatedBy(id+"F40.planeOp",FACE);
            var sketch = newSketch(context, id + "F44", { "sketchPlane" : qUnion([Q0])});
            skCircle(sketch, "E269.0", {"center": v(-94.95, -9.9) * mm, "radius": 4 * mm});
            skCircle(sketch, "E269.1", {"center": v(-94.95, -9.9) * mm, "radius": 5.5 * mm});
            skCircle(sketch, "E269.2", {"center": v(-19.95, -9.9) * mm, "radius": 4 * mm});
            skCircle(sketch, "E269.3", {"center": v(-19.95, -9.9) * mm, "radius": 5.5 * mm});
            skSolve(sketch);
        }
        {
            var Q0;
            Q0=qCreatedBy(id+"F41.planeOp",FACE);
            var sketch = newSketch(context, id + "F45", { "sketchPlane" : qUnion([Q0])});
            skCircle(sketch, "E270.0", {"center": v(-94.95, -9.9) * mm, "radius": 4 * mm});
            skCircle(sketch, "E270.1", {"center": v(-94.95, -9.9) * mm, "radius": 5.5 * mm});
            skCircle(sketch, "E270.2", {"center": v(-19.95, -9.9) * mm, "radius": 4 * mm});
            skCircle(sketch, "E270.3", {"center": v(-19.95, -9.9) * mm, "radius": 5.5 * mm});
            skSolve(sketch);
        }
        {
            var Q0;
            Q0=qCreatedBy(id+"F42.planeOp",FACE);
            var sketch = newSketch(context, id + "F46", { "sketchPlane" : qUnion([Q0])});
            skCircle(sketch, "E271.0", {"center": v(-94.95, -9.9) * mm, "radius": 4 * mm});
            skCircle(sketch, "E271.1", {"center": v(-94.95, -9.9) * mm, "radius": 5.5 * mm});
            skCircle(sketch, "E271.2", {"center": v(-19.95, -9.9) * mm, "radius": 4 * mm});
            skCircle(sketch, "E271.3", {"center": v(-19.95, -9.9) * mm, "radius": 5.5 * mm});
            skSolve(sketch);
        }
        {
            var Q0;
            Q0=makeQuery(id+"F43.imprint","IMPRINT",FACE,{"disambiguationData":[TD([[makeQuery(id+"F43.imprint","IMPRINT",EDGE,{"derivedFrom":sQuery(id+"F43.wireOp",EDGE,"E266.1")}),-1.0]])]});
            var Q1;
            Q1=makeQuery(id+"F43.imprint","IMPRINT",FACE,{"disambiguationData":[TD([[makeQuery(id+"F43.imprint","IMPRINT",EDGE,{"derivedFrom":sQuery(id+"F43.wireOp",EDGE,"E266.0")}),-1.0]])]});
            var Q2;
            Q2=makeQuery(id+"F44.imprint","IMPRINT",FACE,{"disambiguationData":[TD([[makeQuery(id+"F44.imprint","IMPRINT",EDGE,{"derivedFrom":sQuery(id+"F44.wireOp",EDGE,"E269.2")}),-1.0]])]});
            var Q3;
            Q3=makeQuery(id+"F44.imprint","IMPRINT",FACE,{"disambiguationData":[TD([[makeQuery(id+"F44.imprint","IMPRINT",EDGE,{"derivedFrom":sQuery(id+"F44.wireOp",EDGE,"E269.0")}),-1.0]])]});
            var Q4;
            Q4=makeQuery(id+"F45.imprint","IMPRINT",FACE,{"disambiguationData":[TD([[makeQuery(id+"F45.imprint","IMPRINT",EDGE,{"derivedFrom":sQuery(id+"F45.wireOp",EDGE,"E270.0")}),-1.0]])]});
            var Q5;
            Q5=makeQuery(id+"F45.imprint","IMPRINT",FACE,{"disambiguationData":[TD([[makeQuery(id+"F45.imprint","IMPRINT",EDGE,{"derivedFrom":sQuery(id+"F45.wireOp",EDGE,"E270.2")}),-1.0]])]});
            var Q6;
            Q6=makeQuery(id+"F46.imprint","IMPRINT",FACE,{"disambiguationData":[TD([[makeQuery(id+"F46.imprint","IMPRINT",EDGE,{"derivedFrom":sQuery(id+"F46.wireOp",EDGE,"E271.2")}),-1.0]])]});
            var Q7;
            Q7=makeQuery(id+"F46.imprint","IMPRINT",FACE,{"disambiguationData":[TD([[makeQuery(id+"F46.imprint","IMPRINT",EDGE,{"derivedFrom":sQuery(id+"F46.wireOp",EDGE,"E271.0")}),-1.0]])]});
            extrude(context, id + "F47", {"entities" : qUnion([Q0, Q1, Q2, Q3, Q4, Q5, Q6, Q7]), "depth" : 8 * mm, "offsetDistance" : 25 * mm});
        }
    });
